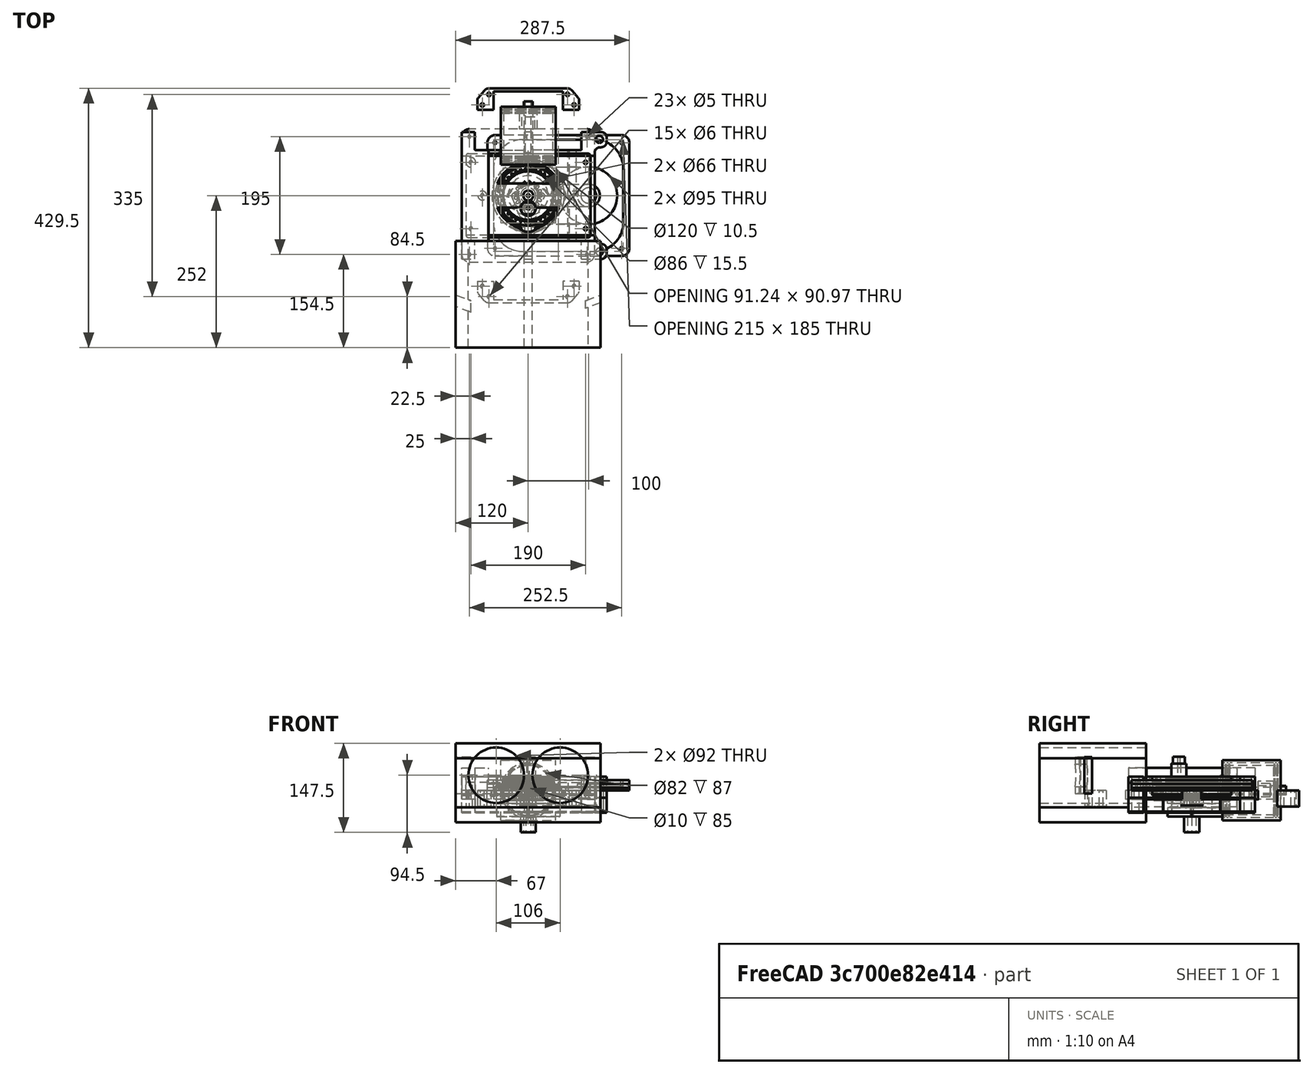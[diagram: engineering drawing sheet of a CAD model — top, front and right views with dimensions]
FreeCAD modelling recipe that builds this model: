
FCSTD DOCUMENT  (FreeCAD 1.0R38641 +678 (Git))
Label: assm4_XX_at_Tusi_rider
License: All rights reserved
objects: Sketcher::SketchObject×46, PartDesign::Body×30, PartDesign::Pad×28, PartDesign::CoordinateSystem×27, App::Link×25, PartDesign::Pocket×19, Mesh::Feature×12, PartDesign::FeatureBase×8, PartDesign::SubtractiveCylinder×5, App::DocumentObjectGroup×4, PartDesign::AdditiveCylinder×4, PartDesign::Boolean×2, Part::Extrusion×2, Part::FeaturePython×2, PartDesign::Hole×2, PartDesign::Fillet×2, App::FeaturePython×1, Spreadsheet::Sheet×1, Part::MultiFuse×1, PartDesign::Chamfer×1, +3 more types
note: 360 computed .brp shape members not serialized (recipe doc carries the construction recipe); baked Part::Feature solids carry a one-line shape summary decoded from their .brp

FEATURE [PartDesign::CoordinateSystem] LCS_Origin
  AttacherType = Attacher::AttachEngine3D
  AttachmentSupport = -> [X_Axis]
  MapMode = 2
FEATURE [App::DocumentObjectGroup] Constraints
FEATURE [App::FeaturePython] Variables  # WARN: FeaturePython — macro-defined, semantics opaque (R4)
  Crank_Angle = 360
  Type = App::PropertyContainer
FEATURE [App::DocumentObjectGroup] Configurations
FEATURE [Sketcher::SketchObject] Sketch002
  ArcFitTolerance = 0
  AttachmentSupport = -> [XY_Plane006]
  FullyConstrained = true
  MakeInternals = false
  MapMode = 5
  expr: Constraints[0] = <<Dim_table>>.crank_dia1
  expr: Constraints[20] = <<Dim_table>>.hex_size
  sketch-geometry (8):
    g0: Circle CenterX=0 CenterY=0 CenterZ=0 NormalX=0 NormalY=0 NormalZ=1 AngleXU=0 Radius=12.5
    g1: LineSegment StartX=4.04145 StartY=7 StartZ=0 EndX=-4.04145 EndY=7 EndZ=0
    g2: LineSegment StartX=-4.04145 StartY=7 StartZ=0 EndX=-8.0829 EndY=0 EndZ=0
    g3: LineSegment StartX=-8.0829 StartY=0 StartZ=0 EndX=-4.04145 EndY=-7 EndZ=0
    g4: LineSegment StartX=-4.04145 StartY=-7 StartZ=0 EndX=4.04145 EndY=-7 EndZ=0
    g5: LineSegment StartX=4.04145 StartY=-7 StartZ=0 EndX=8.0829 EndY=-9e-16 EndZ=0
    g6: LineSegment StartX=8.0829 StartY=-9e-16 StartZ=0 EndX=4.04145 EndY=7 EndZ=0
    g7: Circle [constr] CenterX=0 CenterY=0 CenterZ=0 NormalX=0 NormalY=0 NormalZ=1 AngleXU=0 Radius=8.0829
  constraints (18):
    c: Diameter(g0) = 25
    c: Coincident(g1,g2)
    c: Coincident(g2,g3)
    c: Coincident(g3,g4)
    c: Coincident(g4,g5)
    c: Coincident(g5,g6)
    c: Coincident(g6,g1)
    c: Equal(g1, g2-g6) x5
    c: PointOnObject(g1,g7)
    c: PointOnObject(g2,g7)
    c: PointOnObject(g3,g7)
    c: PointOnObject(g4,g7)
    c: PointOnObject(g5,g7)
    c: PointOnObject(g6,g7)
    c: Coincident(g7,g0)
    c: Horizontal(g1)
    c: DistanceY(g3,g1) = 14
    c: Coincident(g0,g-1)
FEATURE [PartDesign::Pad] Pad005
  Direction = (0,0,1)
  Length = 26
  Length2 = 10
  Profile = -> Sketch002
  ReferenceAxis = -> Sketch002 [N_Axis]
  Reversed = true
  Suppressed = false
  Type = 0
FEATURE [PartDesign::Body] Body005  label="Шейка коренная"
  AllowCompound = false
  Group = -> [Sketch002,Pad005]
  Origin = -> Origin006
  Placement = pos=(0,0,47) rot=(0,0,1;0rad)
  Tip = -> Pad005
FEATURE [PartDesign::FeatureBase] Clone004
  BaseFeature = -> Body005
  Suppressed = false
FEATURE [PartDesign::Body] Body054
  AllowCompound = false
  Group = -> [Clone004]
  Origin = -> Origin055
  Placement = pos=(0,0,-43.5) rot=(0,0,1;0rad)
  Tip = -> Clone004
FEATURE [Sketcher::SketchObject] Sketch003
  ArcFitTolerance = 0
  AttachmentSupport = -> [XY_Plane005]
  FullyConstrained = true
  MakeInternals = false
  MapMode = 5
  expr: Constraints[17] = <<Dim_table>>.fillet_r
  expr: Constraints[18] = <<Dim_table>>.fillet_r
  expr: Constraints[21] = <<Dim_table>>.inter_shaft_len - <<Dim_table>>.zazor
  expr: Constraints[23] = <<Dim_table>>.axle_hole_dia
  expr: Constraints[25] = 70
  expr: Constraints[26] = <<Dim_table>>.crank_dia2 * 1.5
  expr: Constraints[27] = <<Dim_table>>.crank_len
  sketch-geometry (14):
    g0: ArcOfCircle CenterX=0 CenterY=0 CenterZ=0 NormalX=0 NormalY=0 NormalZ=1 AngleXU=0 Radius=52.5 StartAngle=0.0396143 EndAngle=3.10198
    g1: ArcOfCircle CenterX=-1.2e-15 CenterY=-21.25 CenterZ=0 NormalX=0 NormalY=0 NormalZ=1 AngleXU=0 Radius=18.75 StartAngle=3.49066 EndAngle=5.93412
    g2: LineSegment [constr] StartX=-17.6192 StartY=-27.6629 StartZ=0 EndX=17.6192 EndY=-27.6629 EndZ=0
    g3: LineSegment StartX=-50.4604 StartY=0 StartZ=0 EndX=-29.0881 EndY=0 EndZ=0
    g4: LineSegment StartX=-27.2087 StartY=-1.31596 StartZ=0 EndX=-17.6192 EndY=-27.6629 EndZ=0
    g5: LineSegment StartX=17.6192 StartY=-27.6629 StartZ=0 EndX=27.2087 EndY=-1.31596 EndZ=0
    g6: LineSegment StartX=29.0881 StartY=-7e-16 StartZ=0 EndX=50.4604 EndY=-7e-16 EndZ=0
    g7: ArcOfCircle CenterX=-29.0881 CenterY=-2 CenterZ=0 NormalX=0 NormalY=0 NormalZ=1 AngleXU=0 Radius=2 StartAngle=0.349066 EndAngle=1.5708
    g8: ArcOfCircle CenterX=29.0881 CenterY=-2 CenterZ=0 NormalX=0 NormalY=0 NormalZ=1 AngleXU=0 Radius=2 StartAngle=1.5708 EndAngle=2.79253
    g9: ArcOfCircle CenterX=50.4604 CenterY=2 CenterZ=0 NormalX=0 NormalY=0 NormalZ=1 AngleXU=0 Radius=2 StartAngle=4.71239 EndAngle=6.3228
    g10: ArcOfCircle CenterX=-50.4604 CenterY=2 CenterZ=0 NormalX=0 NormalY=0 NormalZ=1 AngleXU=0 Radius=2 StartAngle=3.10198 EndAngle=4.71239
    g11: Circle [constr] CenterX=0 CenterY=0 CenterZ=0 NormalX=0 NormalY=0 NormalZ=1 AngleXU=0 Radius=49.75
    g12: Circle CenterX=0 CenterY=0 CenterZ=0 NormalX=0 NormalY=0 NormalZ=1 AngleXU=0 Radius=2.5
    g13: Circle [constr] CenterX=-1.2e-15 CenterY=-21.25 CenterZ=0 NormalX=0 NormalY=0 NormalZ=1 AngleXU=0 Radius=2.5
  constraints (31):
    c: Coincident(g2,g1)
    c: Coincident(g2,g1)
    c: Horizontal(g2)
    c: Horizontal(g3)
    c: Horizontal(g6)
    c: Tangent(g4,g1) = -1.5708
    c: Tangent(g5,g1) = -1.5708
    c: Tangent(g3,g7) = 1.5708
    c: Tangent(g4,g7) = 1.5708
    c: Tangent(g6,g8) = 1.5708
    c: Tangent(g5,g8) = 1.5708
    c: Tangent(g6,g9) = -1.5708
    c: Tangent(g0,g9) = -1.5708
    c: Tangent(g0,g10) = -1.5708
    c: Tangent(g3,g10) = -1.5708
    c: Symmetric(g7,g8,g-2)
    c: Symmetric(g10,g9,g-2)
    c: Radius(g10) = 2
    c: Radius(g7) = 2
    c: Coincident(g0,g-1)
    c: Coincident(g11,g0)
    c: Diameter(g11) = 99.5
    c: Coincident(g12,g11)
    c: Diameter(g12) = 5
    c: Diameter(g0) = 105
    c: Angle(g5) = 1.22173
    c: Diameter(g1) = 37.5
    c: DistanceY(g1,g12) = 21.25
    c: PointOnObject(g3,g-1)
    c: Coincident(g13,g1)
    c: Equal(g13,g12)
FEATURE [PartDesign::Pad] Pad004
  Direction = (0,0,1)
  Length = 15
  Length2 = 10
  Profile = -> Sketch003
  ReferenceAxis = -> Sketch003 [N_Axis]
  Suppressed = false
  Type = 0
FEATURE [PartDesign::Body] Body004  label="Щека"
  AllowCompound = false
  Group = -> [Sketch003,Pad004]
  Origin = -> Origin005
  Placement = pos=(0,0,12.5) rot=(0,0,1;0rad)
  Tip = -> Pad004
FEATURE [PartDesign::FeatureBase] Clone005
  BaseFeature = -> Body004
  Suppressed = false
FEATURE [PartDesign::Body] Body055
  AllowCompound = false
  Group = -> [Clone005]
  Origin = -> Origin056
  Placement = pos=(0,0,-43.5) rot=(0,0,1;0rad)
  Tip = -> Clone005
FEATURE [Sketcher::SketchObject] Sketch004
  ArcFitTolerance = 0
  AttachmentSupport = -> [XY_Plane004]
  FullyConstrained = true
  MakeInternals = false
  MapMode = 5
  expr: Constraints[0] = <<Dim_table>>.crank_dia2
  expr: Constraints[2] = <<Dim_table>>.crank_len
  expr: Constraints[4] = <<Dim_table>>.axle_hole_dia
  sketch-geometry (2):
    g0: Circle CenterX=0 CenterY=-21.25 CenterZ=0 NormalX=0 NormalY=0 NormalZ=1 AngleXU=0 Radius=12.5
    g1: Circle CenterX=0 CenterY=-21.25 CenterZ=0 NormalX=0 NormalY=0 NormalZ=1 AngleXU=0 Radius=2.5
  constraints (5):
    c: Diameter(g0) = 25
    c: PointOnObject(g0,g-2)
    c: DistanceY(g0,g-1) = 21.25
    c: Coincident(g1,g0)
    c: Diameter(g1) = 5
FEATURE [PartDesign::Pad] Pad003
  Direction = (0,0,1)
  Length = 79.5
  Length2 = 0
  Profile = -> Sketch004
  ReferenceAxis = -> Sketch004 [N_Axis]
  Suppressed = false
  Type = 0
FEATURE [Sketcher::SketchObject] Sketch005
  ArcFitTolerance = 0
  AttachmentSupport = -> [XY_Plane002]
  FullyConstrained = true
  MakeInternals = false
  MapMode = 5
  expr: Constraints[1] = <<Dim_table>>.crank_dia2 + <<Dim_table>>.zazor
  expr: Constraints[26] = 10
  expr: Constraints[27] = <<Dim_table>>.ecc_dia * 0.8
  expr: Constraints[28] = <<Dim_table>>.crank_dia2 * 2
  expr: Constraints[2] = <<Dim_table>>.ecc_dia + <<Dim_table>>.roller_dia
  expr: Constraints[3] = <<Dim_table>>.crank_len
  sketch-geometry (14):
    g0: Circle CenterX=0 CenterY=-21.25 CenterZ=0 NormalX=0 NormalY=0 NormalZ=1 AngleXU=0 Radius=41.5
    g1: Circle CenterX=0 CenterY=0 CenterZ=0 NormalX=0 NormalY=0 NormalZ=1 AngleXU=0 Radius=12.75
    g2: ArcOfCircle CenterX=0 CenterY=-21.25 CenterZ=0 NormalX=0 NormalY=0 NormalZ=1 AngleXU=0 Radius=32 StartAngle=3.32205 EndAngle=4.38515
    g3: ArcOfCircle CenterX=0 CenterY=-21.25 CenterZ=0 NormalX=0 NormalY=0 NormalZ=1 AngleXU=0 Radius=32 StartAngle=5.03963 EndAngle=6.10273
    g4: LineSegment StartX=-5 StartY=-27.5681 StartZ=0 EndX=-5 EndY=-47.7641 EndZ=0
    g5: LineSegment StartX=5 StartY=-27.5681 StartZ=0 EndX=5 EndY=-47.7641 EndZ=0
    g6: ArcOfCircle CenterX=0 CenterY=0 CenterZ=0 NormalX=0 NormalY=0 NormalZ=1 AngleXU=0 Radius=25 StartAngle=3.98424 EndAngle=4.39683
    g7: ArcOfCircle CenterX=0 CenterY=0 CenterZ=0 NormalX=0 NormalY=0 NormalZ=1 AngleXU=0 Radius=25 StartAngle=5.02794 EndAngle=5.44053
    g8: ArcOfCircle CenterX=-22.6265 CenterY=-25.3779 CenterZ=0 NormalX=0 NormalY=0 NormalZ=1 AngleXU=0 Radius=9 StartAngle=0.842651 EndAngle=3.32205
    g9: ArcOfCircle CenterX=22.6265 CenterY=-25.3779 CenterZ=0 NormalX=0 NormalY=0 NormalZ=1 AngleXU=0 Radius=9 StartAngle=6.10273 EndAngle=8.58213
    g10: ArcOfCircle CenterX=-9 CenterY=-47.7641 CenterZ=0 NormalX=0 NormalY=0 NormalZ=1 AngleXU=0 Radius=4 StartAngle=4.38515 EndAngle=6.28319
    g11: ArcOfCircle CenterX=9 CenterY=-47.7641 CenterZ=0 NormalX=0 NormalY=0 NormalZ=1 AngleXU=0 Radius=4 StartAngle=3.14159 EndAngle=5.03963
    g12: ArcOfCircle CenterX=-9 CenterY=-27.5681 CenterZ=0 NormalX=0 NormalY=0 NormalZ=1 AngleXU=0 Radius=4 StartAngle=0 EndAngle=1.25524
    g13: ArcOfCircle CenterX=9 CenterY=-27.5681 CenterZ=0 NormalX=0 NormalY=0 NormalZ=1 AngleXU=0 Radius=4 StartAngle=1.88635 EndAngle=3.14159
  constraints (32):
    c: PointOnObject(g0,g-2)
    c: Diameter(g1) = 25.5
    c: Diameter(g0) = 83
    c: Distance(g1,g0) = 21.25
    c: Coincident(g1,g-1)
    c: Coincident(g2,g0)
    c: Coincident(g3,g0)
    c: Equal(g2,g3)
    c: Vertical(g4)
    c: Coincident(g6,g1)
    c: Coincident(g7,g1)
    c: Tangent(g2,g8) = -1.5708
    c: Tangent(g6,g8) = 1.5708
    c: Tangent(g7,g9) = 1.5708
    c: Tangent(g3,g9) = -1.5708
    c: Tangent(g2,g10) = -1.5708
    c: Tangent(g4,g10) = 1.5708
    c: Tangent(g5,g11) = -1.5708
    c: Tangent(g3,g11) = -1.5708
    c: Tangent(g6,g12) = 1.5708
    c: Tangent(g4,g12) = 1.5708
    c: Tangent(g5,g13) = -1.5708
    c: Tangent(g7,g13) = 1.5708
    c: Symmetric(g12,g13,g-2)
    c: Symmetric(g10,g11,g-2)
    c: Symmetric(g8,g9,g-2)
    c: DistanceX(g4,g5) = 10
    c: Diameter(g2) = 64
    c: Diameter(g6) = 50
    c: Radius(g10) = 4
    c: Equal(g10,g12)
    c: Radius(g8) = 9
FEATURE [PartDesign::CoordinateSystem] Eccentr
  AttacherType = Attacher::AttachEngine3D
  AttachmentOffset = pos=(0,0,0) rot=(0,0,1;1.5708rad)
  AttachmentSupport = -> [Sketch005]
  MapMode = 11
  Placement = pos=(0,0,0) rot=(0,0,1;3.14159rad)
FEATURE [PartDesign::Pad] Pad001
  Direction = (0,0,1)
  Length = 16.5
  Length2 = 0
  Profile = -> Sketch005
  ReferenceAxis = -> Sketch005 [N_Axis]
  Reversed = true
  Suppressed = false
  Type = 0
  expr: Length = <<Dim_table>>.ecc_hei
FEATURE [Sketcher::SketchObject] Sketch007
  ArcFitTolerance = 0
  AttachmentSupport = -> [XY_Plane003]
  FullyConstrained = true
  MakeInternals = false
  MapMode = 5
  expr: Constraints[15] = <<Dim_table>>.ecc_dia * 1.3
  expr: Constraints[17] = <<Dim_table>>.ecc_dia * 0.8
  expr: Constraints[1] = <<Dim_table>>.ecc_dia + 2 * <<Dim_table>>.roller_dia
  sketch-geometry (15):
    g0: Circle CenterX=0 CenterY=0 CenterZ=0 NormalX=0 NormalY=0 NormalZ=1 AngleXU=0 Radius=43
    g1: ArcOfCircle CenterX=0 CenterY=0 CenterZ=0 NormalX=0 NormalY=0 NormalZ=1 AngleXU=0 Radius=52 StartAngle=1.86916 EndAngle=3.14159
    g2: ArcOfCircle CenterX=0 CenterY=0 CenterZ=0 NormalX=0 NormalY=0 NormalZ=1 AngleXU=0 Radius=52 StartAngle=0 EndAngle=1.27243
    g3: LineSegment StartX=-11.8314 StartY=53.6134 StartZ=0 EndX=-10 EndY=64 EndZ=0
    g4: LineSegment StartX=-10 StartY=64 StartZ=0 EndX=10 EndY=64 EndZ=0
    g5: LineSegment StartX=10 StartY=64 StartZ=0 EndX=11.8314 EndY=53.6134 EndZ=0
    g6: ArcOfCircle CenterX=-16.7555 CenterY=54.4817 CenterZ=0 NormalX=0 NormalY=0 NormalZ=1 AngleXU=0 Radius=5 StartAngle=5.01075 EndAngle=6.10865
    g7: ArcOfCircle CenterX=16.7555 CenterY=54.4817 CenterZ=0 NormalX=0 NormalY=0 NormalZ=1 AngleXU=0 Radius=5 StartAngle=3.31613 EndAngle=4.41403
    g8: ArcOfCircle CenterX=-2.7e-15 CenterY=2.94305e-05 CenterZ=0 NormalX=0 NormalY=0 NormalZ=1 AngleXU=0 Radius=52 StartAngle=3.14159 EndAngle=4.41403
    g9: ArcOfCircle CenterX=-16.7555 CenterY=-54.4817 CenterZ=0 NormalX=0 NormalY=0 NormalZ=1 AngleXU=0 Radius=5 StartAngle=0.174533 EndAngle=1.27243
    g10: LineSegment StartX=-11.8314 StartY=-53.6134 StartZ=0 EndX=-10 EndY=-64 EndZ=0
    g11: LineSegment StartX=-10 StartY=-64 StartZ=0 EndX=10 EndY=-64 EndZ=0
    g12: LineSegment StartX=10 StartY=-64 StartZ=0 EndX=11.8314 EndY=-53.6134 EndZ=0
    g13: ArcOfCircle CenterX=16.7555 CenterY=-54.4817 CenterZ=0 NormalX=0 NormalY=0 NormalZ=1 AngleXU=0 Radius=5 StartAngle=1.86916 EndAngle=2.96706
    g14: ArcOfCircle CenterX=-2.7e-15 CenterY=2.94305e-05 CenterZ=0 NormalX=0 NormalY=0 NormalZ=1 AngleXU=0 Radius=52 StartAngle=5.01075 EndAngle=6.28318
  constraints (36):
    c: Coincident(g0,g-1)
    c: Diameter(g0) = 86
    c: Coincident(g1,g0)
    c: Coincident(g2,g0)
    c: Equal(g1,g2)
    c: Coincident(g3,g4)
    c: Coincident(g4,g5)
    c: Tangent(g1,g6) = 1.5708
    c: Tangent(g3,g6) = -1.5708
    c: Tangent(g5,g7) = -1.5708
    c: Tangent(g2,g7) = 1.5708
    c: Symmetric(g6,g7,g-2)
    c: Symmetric(g3,g4,g-2)
    c: PointOnObject(g1,g-1)
    c: PointOnObject(g2,g-1)
    c: Diameter(g1) = 104
    c: Distance(g4,g4) = 20
    c: DistanceY(g0,g4) = 64
    c: Radius(g6) = 5
    c: Angle(g3,g-2) = 0.174533
    c: Equal(g8,g14)
    c: Coincident(g10,g11)
    c: Coincident(g11,g12)
    c: Tangent(g8,g9) = 1.5708
    c: Tangent(g10,g9) = 1.5708
    c: Tangent(g12,g13) = 1.5708
    c: Tangent(g14,g13) = 1.5708
    c: Equal(g8,g1)
    c: Equal(g13,g7)
    c: Symmetric(g9,g13,g-2)
    c: Symmetric(g11,g4,g-1)
    c: Symmetric(g10,g11,g-2)
    c: Parallel(g12,g3)
    c: Coincident(g8,g1)
    c: Coincident(g14,g2)
    c: Coincident(g8,g14)
FEATURE [PartDesign::Pad] Pad002
  Direction = (0,0,1)
  Length = 15.5
  Length2 = 10
  Midplane = true
  Profile = -> Sketch007
  ReferenceAxis = -> Sketch007 [N_Axis]
  Suppressed = false
  Type = 0
  expr: Length = <<Dim_table>>.ecc_hei - 1
FEATURE [PartDesign::CoordinateSystem] Shtok
  AttacherType = Attacher::AttachEngine3D
  AttachmentSupport = -> [Pad002]
  MapMode = 45
  Placement = pos=(-7.2e-15,2.69855e-05,-3e-16) rot=(0,0,1;0rad)
FEATURE [Sketcher::SketchObject] Main
  ArcFitTolerance = 0
  AttachmentSupport = -> [LCS_Origin]
  FullyConstrained = false
  MakeInternals = false
  MapMode = 5
  expr: Constraints[17] = <<Dim_table>>.piston_dia
  expr: Constraints[18] = <<Dim_table>>.piston_hei
  expr: Constraints[19] = <<Dim_table>>.ecc_dia
  expr: Constraints[1] = <<Variables>>.Crank_Angle
  expr: Constraints[26] = <<Dim_table>>.rod_len
  expr: Constraints[2] = <<Dim_table>>.crank_len
  expr: Constraints[48] = <<Dim_table>>.crank_len
  expr: Constraints[53] = <<Dim_table>>.crank_len
  expr: Constraints[5] = <<Dim_table>>.crank_dia1
  expr: Constraints[67] = <<Variables>>.Crank_Angle
  expr: Constraints[6] = <<Dim_table>>.crank_dia2
  sketch-geometry (33):
    g0: LineSegment StartX=0 StartY=0 StartZ=0 EndX=-2.74918e-11 EndY=21.25 EndZ=0
    g1: Circle [constr] CenterX=0 CenterY=0 CenterZ=0 NormalX=0 NormalY=0 NormalZ=1 AngleXU=0 Radius=12.5
    g2: Circle CenterX=-2.74918e-11 CenterY=21.25 CenterZ=0 NormalX=0 NormalY=0 NormalZ=1 AngleXU=0 Radius=12.5
    g3: LineSegment StartX=-36 StartY=221.5 StartZ=0 EndX=36 EndY=221.5 EndZ=0
    g4: LineSegment StartX=36 StartY=221.5 StartZ=0 EndX=36 EndY=182.5 EndZ=0
    g5: LineSegment StartX=36 StartY=182.5 StartZ=0 EndX=-36 EndY=182.5 EndZ=0
    g6: LineSegment StartX=-36 StartY=182.5 StartZ=0 EndX=-36 EndY=221.5 EndZ=0
    g7: LineSegment [constr] StartX=-36 StartY=182.5 StartZ=0 EndX=36 EndY=221.5 EndZ=0
    g8: Circle CenterX=6.3065e-12 CenterY=42.5 CenterZ=0 NormalX=0 NormalY=0 NormalZ=1 AngleXU=0 Radius=40
    g9: LineSegment StartX=120.841 StartY=-28.1981 StartZ=0 EndX=84.8405 EndY=-90.5519 EndZ=0
    g10: LineSegment StartX=84.8405 StartY=-90.5519 StartZ=0 EndX=118.616 EndY=-110.052 EndZ=0
    g11: LineSegment StartX=118.616 StartY=-110.052 StartZ=0 EndX=154.616 EndY=-47.6981 EndZ=0
    g12: LineSegment StartX=154.616 StartY=-47.6981 StartZ=0 EndX=120.841 EndY=-28.1981 EndZ=0
    g13: LineSegment StartX=6.3065e-12 StartY=182.5 StartZ=0 EndX=6.3065e-12 EndY=42.5 EndZ=0
    g14: LineSegment StartX=-36 StartY=-136.5 StartZ=0 EndX=36 EndY=-136.5 EndZ=0
    g15: LineSegment StartX=36 StartY=-136.5 StartZ=0 EndX=36 EndY=-97.5 EndZ=0
    g16: LineSegment StartX=36 StartY=-97.5 StartZ=0 EndX=-36 EndY=-97.5 EndZ=0
    g17: LineSegment StartX=-36 StartY=-97.5 StartZ=0 EndX=-36 EndY=-136.5 EndZ=0
    g18: LineSegment [constr] StartX=6.3065e-12 StartY=-97.5 StartZ=0 EndX=6.3065e-12 EndY=42.5 EndZ=0
    g19: LineSegment StartX=155.422 StartY=131.302 StartZ=0 EndX=191.422 EndY=68.9481 EndZ=0
    g20: LineSegment StartX=191.422 StartY=68.9481 StartZ=0 EndX=157.647 EndY=49.4481 EndZ=0
    g21: LineSegment StartX=157.647 StartY=49.4481 StartZ=0 EndX=121.647 EndY=111.802 EndZ=0
    g22: LineSegment StartX=121.647 StartY=111.802 StartZ=0 EndX=155.422 EndY=131.302 EndZ=0
    g23: LineSegment StartX=-2.74918e-11 StartY=21.25 StartZ=0 EndX=18.403 EndY=10.625 EndZ=0
    g24: LineSegment StartX=-2.74918e-11 StartY=21.25 StartZ=0 EndX=7.4e-15 EndY=-3.6e-15 EndZ=0
    g25: LineSegment StartX=-2.74918e-11 StartY=21.25 StartZ=0 EndX=6.3065e-12 EndY=42.5 EndZ=0
    g26: LineSegment [constr] StartX=-238.615 StartY=-137.765 StartZ=0 EndX=319.415 EndY=184.414 EndZ=0
    g27: LineSegment [constr] StartX=-222.3 StartY=128.345 StartZ=0 EndX=247.423 EndY=-142.85 EndZ=0
    g28: LineSegment StartX=-2.74918e-11 StartY=21.25 StartZ=0 EndX=-18.403 EndY=10.625 EndZ=0
    g29: Circle CenterX=-18.403 CenterY=10.625 CenterZ=0 NormalX=0 NormalY=0 NormalZ=1 AngleXU=0 Radius=40
    g30: Circle CenterX=18.403 CenterY=10.625 CenterZ=0 NormalX=0 NormalY=0 NormalZ=1 AngleXU=0 Radius=40
    g31: LineSegment StartX=18.403 StartY=10.625 StartZ=0 EndX=139.647 EndY=80.625 EndZ=0
    g32: LineSegment StartX=-18.403 StartY=10.625 StartZ=0 EndX=102.841 EndY=-59.375 EndZ=0
  constraints (87):
    c: Coincident(g0,g-1)
    c: Angle(g0,g-2) = 6.28319
    c: Distance(g0) = 21.25
    c: Coincident(g1,g0)
    c: Coincident(g2,g0)
    c: Diameter(g1) = 25
    c: Diameter(g2) = 25
    c: Coincident(g3,g4)
    c: Coincident(g4,g5)
    c: Coincident(g5,g6)
    c: Coincident(g6,g3)
    c: Horizontal(g3)
    c: Horizontal(g5)
    c: Vertical(g4)
    c: Vertical(g6)
    c: Coincident(g7,g5)
    c: Coincident(g7,g3)
    c: Distance(g3) = 72
    c: Distance(g4) = 39
    c: Diameter(g8) = 80
    c: Coincident(g9,g10)
    c: Coincident(g10,g11)
    c: Coincident(g11,g12)
    c: Coincident(g12,g9)
    c: Vertical(g13)
    c: Symmetric(g5,g4,g13)
    c: Distance(g13,g13) = 140
    c: Equal(g4,g12)
    c: Equal(g3,g11)
    c: Coincident(g14,g15)
    c: Coincident(g15,g16)
    c: Coincident(g16,g17)
    c: Coincident(g17,g14)
    c: Horizontal(g14)
    c: Horizontal(g16)
    c: Vertical(g15)
    c: Vertical(g17)
    c: Vertical(g18)
    c: Symmetric(g16,g15,g18)
    c: Equal(g16,g11)
    c: Equal(g15,g12)
    c: Coincident(g19,g20)
    c: Coincident(g20,g21)
    c: Coincident(g21,g22)
    c: Coincident(g22,g19)
    c: Equal(g22,g12)
    c: Equal(g21,g11)
    c: Coincident(g23,g0)
    c: Distance(g23,g23) = 21.25
    c: Coincident(g24,g0)
    c: Coincident(g25,g0)
    c: Equal(g25,g24)
    c: Angle(g23,g25) = 2.0944
    c: Distance(g24,g24) = 21.25
    c: PointOnObject(g24,g27)
    c: PointOnObject(g0,g27)
    c: PointOnObject(g0,g26)
    c: Parallel(g9,g11)
    c: Parallel(g12,g10)
    c: Angle(g9,g12) = 1.5708
    c: Angle(g21,g22) = 1.5708
    c: Parallel(g22,g20)
    c: Parallel(g19,g21)
    c: Equal(g13,g18)
    c: Angle(g-2,g26) = 2.0944
    c: Angle(g-2,g27) = 1.0472
    c: Coincident(g13,g25)
    c: Angle(g-2,g25) = 6.28319
    c: Coincident(g28,g0)
    c: Equal(g23,g28)
    c: Angle(g28,g23) = 2.0944
    c: Coincident(g8,g13)
    c: Equal(g8,g30)
    c: Equal(g30,g29)
    c: Coincident(g30,g23)
    c: Coincident(g29,g28)
    c: Coincident(g31,g23)
    c: Coincident(g32,g28)
    c: Symmetric(g9,g9,g32)
    c: Symmetric(g21,g20,g31)
    c: Angle(g21,g31) = 1.5708
    c: Angle(g9,g32) = 1.5708
    c: PointOnObject(g32,g27)
    c: PointOnObject(g31,g26)
    c: Coincident(g18,g8)
    c: Equal(g18,g32)
    c: Equal(g32,g31)
FEATURE [Sketcher::SketchObject] Sketch021
  ArcFitTolerance = 0
  AttachmentSupport = -> [XY_Plane062]
  FullyConstrained = false
  MakeInternals = false
  MapMode = 5
  sketch-geometry (30):
    g0: LineSegment [constr] StartX=-110 StartY=225 StartZ=0 EndX=110 EndY=225 EndZ=0
    g1: LineSegment [constr] StartX=110 StartY=225 StartZ=0 EndX=110 EndY=-225 EndZ=0
    g2: LineSegment [constr] StartX=110 StartY=-225 StartZ=0 EndX=-110 EndY=-225 EndZ=0
    g3: LineSegment [constr] StartX=-110 StartY=-225 StartZ=0 EndX=-110 EndY=225 EndZ=0
    g4: LineSegment [constr] StartX=-110 StartY=225 StartZ=0 EndX=-110 EndY=105 EndZ=0
    g5: LineSegment [constr] StartX=-110 StartY=105 StartZ=0 EndX=110 EndY=105 EndZ=0
    g6: LineSegment [constr] StartX=110 StartY=105 StartZ=0 EndX=110 EndY=225 EndZ=0
    g7: LineSegment [constr] StartX=-110 StartY=-225 StartZ=0 EndX=-110 EndY=-105 EndZ=0
    g8: LineSegment StartX=-110 StartY=-105 StartZ=0 EndX=110 EndY=-105 EndZ=0
    g9: LineSegment [constr] StartX=110 StartY=-105 StartZ=0 EndX=110 EndY=-225 EndZ=0
    g10: LineSegment [constr] StartX=-110 StartY=-105 StartZ=0 EndX=-110 EndY=105 EndZ=0
    g11: LineSegment StartX=110 StartY=105 StartZ=0 EndX=-110 EndY=105 EndZ=0
    g12: Circle CenterX=0 CenterY=0 CenterZ=0 NormalX=0 NormalY=0 NormalZ=1 AngleXU=0 Radius=33
    g13: LineSegment StartX=-110 StartY=105 StartZ=0 EndX=-110 EndY=0 EndZ=0
    g14: LineSegment [constr] StartX=110 StartY=-105 StartZ=0 EndX=110 EndY=105 EndZ=0
    g15: LineSegment StartX=110 StartY=105 StartZ=0 EndX=120.902 EndY=105 EndZ=0
    g16: LineSegment StartX=130 StartY=95.9016 StartZ=0 EndX=130 EndY=89.0984 EndZ=0
    g17: LineSegment StartX=120.902 StartY=80 StartZ=0 EndX=119.098 EndY=80 EndZ=0
    g18: ArcOfCircle CenterX=120.902 CenterY=95.9016 CenterZ=0 NormalX=0 NormalY=0 NormalZ=1 AngleXU=0 Radius=9.09838 StartAngle=0 EndAngle=1.5708
    g19: ArcOfCircle CenterX=120.902 CenterY=89.0984 CenterZ=0 NormalX=0 NormalY=0 NormalZ=1 AngleXU=0 Radius=9.09838 StartAngle=4.71239 EndAngle=6.28319
    g20: LineSegment StartX=110 StartY=70.9016 StartZ=0 EndX=110 EndY=0 EndZ=0
    g21: ArcOfCircle CenterX=119.098 CenterY=70.9016 CenterZ=0 NormalX=0 NormalY=0 NormalZ=1 AngleXU=0 Radius=9.09838 StartAngle=1.5708 EndAngle=3.14159
    g22: LineSegment StartX=110 StartY=-105 StartZ=0 EndX=120.902 EndY=-105 EndZ=0
    g23: LineSegment StartX=130 StartY=-95.9016 StartZ=0 EndX=130 EndY=-89.0984 EndZ=0
    g24: LineSegment StartX=120.902 StartY=-80 StartZ=0 EndX=119.098 EndY=-80 EndZ=0
    g25: ArcOfCircle CenterX=120.902 CenterY=-95.9016 CenterZ=0 NormalX=0 NormalY=0 NormalZ=1 AngleXU=0 Radius=9.09838 StartAngle=4.71239 EndAngle=6.28319
    g26: ArcOfCircle CenterX=120.902 CenterY=-89.0984 CenterZ=0 NormalX=0 NormalY=0 NormalZ=1 AngleXU=0 Radius=9.09838 StartAngle=0 EndAngle=1.5708
    g27: LineSegment StartX=110 StartY=-70.9016 StartZ=0 EndX=110 EndY=0 EndZ=0
    g28: ArcOfCircle CenterX=119.098 CenterY=-70.9016 CenterZ=0 NormalX=0 NormalY=0 NormalZ=1 AngleXU=0 Radius=9.09838 StartAngle=3.14159 EndAngle=4.71239
    g29: LineSegment StartX=-110 StartY=-105 StartZ=0 EndX=-110 EndY=0 EndZ=0
  constraints (61):
    c: Coincident(g0,g1)
    c: Coincident(g1,g2)
    c: Coincident(g2,g3)
    c: Coincident(g3,g0)
    c: Horizontal(g2)
    c: Vertical(g1)
    c: Symmetric(g0,g0,g-2)
    c: Symmetric(g0,g2,g-1)
    c: Coincident(g0,g4)
    c: PointOnObject(g4,g3)
    c: Coincident(g4,g5)
    c: PointOnObject(g5,g1)
    c: Horizontal(g5)
    c: Coincident(g6,g0)
    c: Coincident(g2,g7)
    c: PointOnObject(g7,g3)
    c: Horizontal(g8)
    c: Coincident(g9,g2)
    c: Equal(g9,g6)
    c: DistanceX(g2,g2) = 220
    c: DistanceY(g3,g3) = 450
    c: DistanceY(g9,g9) = 120
    c: Coincident(g10,g4)
    c: Coincident(g11,g10)
    c: Diameter(g12) = 66
    c: PointOnObject(g13,g-1)
    c: Vertical(g13)
    c: Vertical(g10)
    c: Vertical(g6)
    c: Coincident(g8,g9)
    c: Coincident(g8,g7)
    c: Coincident(g11,g5)
    c: Symmetric(g8,g11,g-1)
    c: Horizontal(g15)
    c: Horizontal(g17)
    c: Vertical(g16)
    c: Tangent(g15,g18) = 1.5708
    c: Tangent(g16,g18) = 1.5708
    c: Tangent(g16,g19) = 1.5708
    c: Tangent(g17,g19) = 1.5708
    c: Equal(g19,g18)
    c: Vertical(g20)
    c: Tangent(g17,g21) = -1.5708
    c: Tangent(g20,g21) = -1.5708
    c: Equal(g19,g21)
    c: Vertical(g14)
    c: Horizontal(g22)
    c: Horizontal(g24)
    c: Vertical(g23)
    c: Tangent(g22,g25) = -1.5708
    c: Tangent(g23,g25) = -1.5708
    c: Tangent(g23,g26) = -1.5708
    c: Tangent(g24,g26) = -1.5708
    c: Equal(g26,g25)
    c: Vertical(g27)
    c: Tangent(g24,g28) = 1.5708
    c: Tangent(g27,g28) = 1.5708
    c: Equal(g26,g28)
    c: Coincident(g13,g11)
    c: Coincident(g29,g8)
    c: Coincident(g29,g13)
FEATURE [Sketcher::SketchObject] Sketch022
  ArcFitTolerance = 0
  AttachmentSupport = -> [XY_Plane062]
  FullyConstrained = true
  MakeInternals = false
  MapMode = 5
  sketch-geometry (5):
    g0: LineSegment StartX=-110 StartY=-105 StartZ=0 EndX=-65.5 EndY=-105 EndZ=0
    g1: LineSegment StartX=-65.5 StartY=-105 StartZ=0 EndX=-65.5 EndY=105 EndZ=0
    g2: LineSegment StartX=-65.5 StartY=105 StartZ=0 EndX=-110 EndY=105 EndZ=0
    g3: LineSegment StartX=-110 StartY=105 StartZ=0 EndX=-110 EndY=-105 EndZ=0
    g4: LineSegment [constr] StartX=65.5 StartY=52.9337 StartZ=0 EndX=65.5 EndY=105 EndZ=0
  constraints (14):
    c: Coincident(g0,g1)
    c: Coincident(g1,g2)
    c: Coincident(g2,g3)
    c: Coincident(g3,g0)
    c: Horizontal(g0)
    c: Horizontal(g2)
    c: Vertical(g3)
    c: Vertical(g4)
    c: DistanceX(g1,g4) = 131
    c: Symmetric(g1,g4,g-2)
    c: DistanceY(g1,g1) = 210
    c: DistanceX(g0,g0) = 44.5
    c: Symmetric(g0,g1,g-1)
    c: Block(g4)
FEATURE [PartDesign::Pad] Pad012
  Direction = (0,0,1)
  Length = 35
  Length2 = 12.5
  Profile = -> Sketch021
  ReferenceAxis = -> Sketch021 [N_Axis]
  Reversed = true
  Suppressed = false
  Type = 4
FEATURE [PartDesign::Pad] Pad013
  BaseFeature = -> Pad012
  Direction = (0,0,1)
  Length = 37.5
  Length2 = -12.5
  Profile = -> Sketch022
  ReferenceAxis = -> Sketch022 [N_Axis]
  Suppressed = false
  Type = 4
FEATURE [Sketcher::SketchObject] Sketch_1
  ArcFitTolerance = 0
  FullyConstrained = false
  MakeInternals = false
  sketch-geometry (8):
    g0: Circle [constr] CenterX=0 CenterY=0 CenterZ=0 NormalX=0 NormalY=0 NormalZ=1 AngleXU=0 Radius=65.5
    g1: ArcOfCircle [constr] CenterX=0 CenterY=0 CenterZ=0 NormalX=0 NormalY=0 NormalZ=1 AngleXU=0 Radius=65.5 StartAngle=1.5708 EndAngle=4.71239
    g2: LineSegment StartX=145.598 StartY=65.5 StartZ=0 EndX=0 EndY=65.5 EndZ=0
    g3: LineSegment StartX=145.598 StartY=-65.5 StartZ=0 EndX=0 EndY=-65.5 EndZ=0
    g4: LineSegment StartX=145.598 StartY=65.5 StartZ=0 EndX=145.598 EndY=-65.5 EndZ=0
    g5: LineSegment StartX=-153.016 StartY=65.5 StartZ=0 EndX=0 EndY=65.5 EndZ=0
    g6: LineSegment StartX=-1.2e-14 StartY=-65.5 StartZ=0 EndX=-153.016 EndY=-65.5 EndZ=0
    g7: LineSegment StartX=-153.016 StartY=-65.5 StartZ=0 EndX=-153.016 EndY=65.5 EndZ=0
  constraints (18):
    c: Coincident(g0,g-1)
    c: Diameter(g0) = 131
    c: Coincident(g1,g0)
    c: PointOnObject(g1,g0)
    c: Horizontal(g2)
    c: Horizontal(g3)
    c: Tangent(g3,g1) = 1.5708
    c: Tangent(g1,g2) = -1.5708
    c: Coincident(g4,g2)
    c: Coincident(g4,g3)
    c: Vertical(g4)
    c: Coincident(g6,g7)
    c: Coincident(g7,g5)
    c: Horizontal(g5)
    c: Horizontal(g6)
    c: Vertical(g7)
    c: Coincident(g5,g2)
    c: Coincident(g6,g3)
FEATURE [PartDesign::Pocket] Pocket005
  BaseFeature = -> Pad013
  Direction = (0,0,-1)
  Length = 6.5
  Length2 = 13
  Profile = -> Sketch_1
  ReferenceAxis = -> Sketch_1 [N_Axis]
  Suppressed = false
  Type = 4
FEATURE [PartDesign::CoordinateSystem] Block_ribb
  AttacherType = Attacher::AttachEngine3D
  AttachmentSupport = -> [Pocket005]
  MapMode = 2
FEATURE [Sketcher::SketchObject] Sketch_2
  ArcFitTolerance = 0
  FullyConstrained = false
  MakeInternals = false
  sketch-geometry (44):
    g0: LineSegment StartX=-0.25 StartY=33.6074 StartZ=0 EndX=-0.25 EndY=47.5 EndZ=0
    g1: LineSegment StartX=-0.25 StartY=47.5 StartZ=0 EndX=126.736 EndY=47.5 EndZ=0
    g2: LineSegment StartX=126.736 StartY=47.5 StartZ=0 EndX=126.736 EndY=47 EndZ=0
    g3: LineSegment StartX=126.736 StartY=47 StartZ=0 EndX=0.25 EndY=47 EndZ=0
    g4: LineSegment StartX=0.25 StartY=47 StartZ=0 EndX=0.25 EndY=33.6074 EndZ=0
    g5: LineSegment StartX=0.25 StartY=33.6074 StartZ=0 EndX=-0.25 EndY=33.6074 EndZ=0
    g6: ArcOfCircle CenterX=86.75 CenterY=76.5 CenterZ=0 NormalX=0 NormalY=0 NormalZ=1 AngleXU=0 Radius=1.5 StartAngle=4.71239 EndAngle=6.28319
    g7: ArcOfCircle CenterX=8.25 CenterY=76.5 CenterZ=0 NormalX=0 NormalY=0 NormalZ=1 AngleXU=0 Radius=1.5 StartAngle=3.14159 EndAngle=4.71239
    g8: LineSegment StartX=86.75 StartY=75 StartZ=0 EndX=8.25 EndY=75 EndZ=0
    g9: LineSegment StartX=88.25 StartY=105 StartZ=0 EndX=6.75 EndY=105 EndZ=0
    g10: LineSegment StartX=6.75 StartY=105 StartZ=0 EndX=6.75 EndY=76.5 EndZ=0
    g11: LineSegment StartX=88.25 StartY=105 StartZ=0 EndX=88.25 EndY=76.5 EndZ=0
    g12: GeomPoint [constr] X=47.5 Y=105 Z=0
    g13: Circle CenterX=-118 CenterY=93 CenterZ=0 NormalX=0 NormalY=0 NormalZ=1 AngleXU=0 Radius=6
    g14: Circle CenterX=118 CenterY=93 CenterZ=0 NormalX=0 NormalY=0 NormalZ=1 AngleXU=0 Radius=6
    g15: LineSegment StartX=-0.067348 StartY=-33.6074 StartZ=0 EndX=-0.067348 EndY=-47.5 EndZ=0
    g16: LineSegment StartX=-0.067348 StartY=-47.5 StartZ=0 EndX=126.736 EndY=-47.5 EndZ=0
    g17: LineSegment StartX=126.736 StartY=-47.5 StartZ=0 EndX=126.736 EndY=-47 EndZ=0
    g18: LineSegment StartX=126.736 StartY=-47 StartZ=0 EndX=0.25 EndY=-47 EndZ=0
    g19: LineSegment StartX=0.25 StartY=-47 StartZ=0 EndX=0.25 EndY=-33.6074 EndZ=0
    g20: LineSegment StartX=0.25 StartY=-33.6074 StartZ=0 EndX=-0.067348 EndY=-33.6074 EndZ=0
    g21: ArcOfCircle CenterX=-86.75 CenterY=76.5 CenterZ=0 NormalX=0 NormalY=0 NormalZ=1 AngleXU=0 Radius=1.5 StartAngle=3.14159 EndAngle=4.71239
    g22: ArcOfCircle CenterX=-8.25 CenterY=76.5 CenterZ=0 NormalX=0 NormalY=0 NormalZ=1 AngleXU=0 Radius=1.5 StartAngle=4.71239 EndAngle=6.28319
    g23: LineSegment StartX=-86.75 StartY=75 StartZ=0 EndX=-8.25 EndY=75 EndZ=0
    g24: LineSegment StartX=-88.25 StartY=105 StartZ=0 EndX=-6.75 EndY=105 EndZ=0
    g25: LineSegment StartX=-6.75 StartY=105 StartZ=0 EndX=-6.75 EndY=76.5 EndZ=0
    g26: LineSegment StartX=-88.25 StartY=105 StartZ=0 EndX=-88.25 EndY=76.5 EndZ=0
    g27: GeomPoint [constr] X=-47.5 Y=105 Z=0
    g28: ArcOfCircle CenterX=86.75 CenterY=-76.5 CenterZ=0 NormalX=0 NormalY=0 NormalZ=1 AngleXU=0 Radius=1.5 StartAngle=0 EndAngle=1.5708
    g29: ArcOfCircle CenterX=8.25 CenterY=-76.5 CenterZ=0 NormalX=0 NormalY=0 NormalZ=1 AngleXU=0 Radius=1.5 StartAngle=1.5708 EndAngle=3.14159
    g30: LineSegment StartX=86.75 StartY=-75 StartZ=0 EndX=8.25 EndY=-75 EndZ=0
    g31: LineSegment StartX=88.25 StartY=-105 StartZ=0 EndX=6.75 EndY=-105 EndZ=0
    g32: LineSegment StartX=6.75 StartY=-105 StartZ=0 EndX=6.75 EndY=-76.5 EndZ=0
    g33: LineSegment StartX=88.25 StartY=-105 StartZ=0 EndX=88.25 EndY=-76.5 EndZ=0
    g34: GeomPoint [constr] X=47.5 Y=-105 Z=0
    g35: Circle CenterX=-118 CenterY=-93 CenterZ=0 NormalX=0 NormalY=0 NormalZ=1 AngleXU=0 Radius=6
    g36: Circle CenterX=118 CenterY=-93 CenterZ=0 NormalX=0 NormalY=0 NormalZ=1 AngleXU=0 Radius=6
    g37: ArcOfCircle CenterX=-86.75 CenterY=-76.5 CenterZ=0 NormalX=0 NormalY=0 NormalZ=1 AngleXU=0 Radius=1.5 StartAngle=1.5708 EndAngle=3.14159
    g38: ArcOfCircle CenterX=-8.25 CenterY=-76.5 CenterZ=0 NormalX=0 NormalY=0 NormalZ=1 AngleXU=0 Radius=1.5 StartAngle=0 EndAngle=1.5708
    g39: LineSegment StartX=-86.75 StartY=-75 StartZ=0 EndX=-8.25 EndY=-75 EndZ=0
    g40: LineSegment StartX=-88.25 StartY=-105 StartZ=0 EndX=-6.75 EndY=-105 EndZ=0
    g41: LineSegment StartX=-6.75 StartY=-105 StartZ=0 EndX=-6.75 EndY=-76.5 EndZ=0
    g42: LineSegment StartX=-88.25 StartY=-105 StartZ=0 EndX=-88.25 EndY=-76.5 EndZ=0
    g43: GeomPoint [constr] X=-47.5 Y=-105 Z=0
  constraints (95):
    c: Vertical(g0)
    c: Coincident(g0,g1)
    c: Horizontal(g1)
    c: Coincident(g1,g2)
    c: Coincident(g2,g3)
    c: Horizontal(g3)
    c: Coincident(g3,g4)
    c: Vertical(g4)
    c: Coincident(g4,g5)
    c: Coincident(g5,g0)
    c: Vertical(g2)
    c: DistanceY(g2,g2) = 0.5
    c: DistanceX(g5,g5) = 0.5
    c: Tangent(g6,g8) = 1.5708
    c: Tangent(g8,g7) = 1.5708
    c: Equal(g6,g7)
    c: Horizontal(g8)
    c: Horizontal(g9)
    c: Vertical(g11)
    c: Vertical(g10)
    c: Tangent(g6,g11) = 1.5708
    c: Tangent(g7,g10) = -1.5708
    c: Coincident(g11,g9)
    c: Coincident(g9,g10)
    c: Symmetric(g9,g9,g12)
    c: Radius(g7) = 1.5
    c: Distance(g7,g9) = 30
    c: Diameter(g13) = 12
    c: Symmetric(g0,g4,g-2)
    c: DistanceY(g-1,g13) = 93
    c: DistanceX(g13,g-1) = 118
    c: DistanceY(g-1,g9) = 105
    c: DistanceX(g9,g9) = 81.5
    c: DistanceX(g-1,g9) = 6.75
    c: Diameter(g14) = 12
    c: Vertical(g15)
    c: Coincident(g15,g16)
    c: Horizontal(g16)
    c: Coincident(g16,g17)
    c: Coincident(g17,g18)
    c: Horizontal(g18)
    c: Coincident(g18,g19)
    c: Vertical(g19)
    c: Coincident(g19,g20)
    c: Coincident(g20,g15)
    c: Vertical(g17)
    c: Tangent(g21,g23) = -1.5708
    c: Tangent(g23,g22) = -1.5708
    c: Equal(g21,g22)
    c: Horizontal(g23)
    c: Horizontal(g24)
    c: Vertical(g26)
    c: Vertical(g25)
    c: Tangent(g21,g26) = -1.5708
    c: Tangent(g22,g25) = 1.5708
    c: Coincident(g26,g24)
    c: Coincident(g24,g25)
    c: Symmetric(g24,g24,g27)
    c: Radius(g22) = 1.5
    c: Distance(g22,g24) = 30
    c: Tangent(g28,g30) = -1.5708
    c: Tangent(g30,g29) = -1.5708
    c: Equal(g28,g29)
    c: Horizontal(g30)
    c: Horizontal(g31)
    c: Vertical(g33)
    c: Vertical(g32)
    c: Tangent(g28,g33) = -1.5708
    c: Tangent(g29,g32) = 1.5708
    c: Coincident(g33,g31)
    c: Coincident(g31,g32)
    c: Symmetric(g31,g31,g34)
    c: Radius(g29) = 1.5
    c: Distance(g29,g31) = 30
    c: Diameter(g35) = 12
    c: Diameter(g36) = 12
    c: Tangent(g37,g39) = 1.5708
    c: Tangent(g39,g38) = 1.5708
    c: Equal(g37,g38)
    c: Horizontal(g39)
    c: Horizontal(g40)
    c: Vertical(g42)
    c: Vertical(g41)
    c: Tangent(g37,g42) = 1.5708
    c: Tangent(g38,g41) = -1.5708
    c: Coincident(g42,g40)
    c: Coincident(g40,g41)
    c: Symmetric(g40,g40,g43)
    c: Radius(g38) = 1.5
    c: Distance(g38,g40) = 30
    c: Symmetric(g19,g4,g-1)
    c: Horizontal(g20)
    c: Symmetric(g17,g2,g-1)
    c: DistanceY(g17,g17) = 0.5
    c: DistanceY(g16,g1) = 95
FEATURE [PartDesign::Pocket] Pocket006
  BaseFeature = -> Pocket005
  Direction = (0,0,-1)
  Length = 50
  Length2 = 50
  Profile = -> Sketch_2
  ReferenceAxis = -> Sketch_2 [N_Axis]
  Suppressed = false
  Type = 4
FEATURE [Sketcher::SketchObject] Sketch028
  ArcFitTolerance = 0
  FullyConstrained = true
  MakeInternals = false
  MapMode = 5
  Placement = pos=(0,-75,0) rot=(1,0,0;1.5708rad)
  sketch-geometry (1):
    g0: Circle CenterX=74 CenterY=-21.75 CenterZ=0 NormalX=0 NormalY=0 NormalZ=1 AngleXU=0 Radius=6
  constraints (3):
    c: Diameter(g0) = 12
    c: DistanceY(g0,g-1) = 21.75
    c: DistanceX(g-1,g0) = 74
FEATURE [PartDesign::Pocket] Pocket011
  BaseFeature = -> Pocket006
  Direction = (0,1,-2e-16)
  Length = 5
  Length2 = 5
  Profile = -> Sketch028
  ReferenceAxis = -> Sketch028 [N_Axis]
  Suppressed = false
  Type = 1
FEATURE [PartDesign::Body] Body061  label="перегородка"
  AllowCompound = false
  Group = -> [Sketch022,Sketch021,Pad012,Pad013,Sketch_1,Pocket005,Block_ribb,Sketch_2,Pocket006,Sketch028,Pocket011]
  Origin = -> Origin062
  Tip = -> Pocket011
FEATURE [PartDesign::Pad] Pad017
  Direction = (0,0,1)
  Length = 37
  Length2 = 22.5
  Profile = -> Sketch021
  ReferenceAxis = -> Sketch021 [N_Axis]
  Reversed = true
  Suppressed = false
  Type = 4
FEATURE [PartDesign::Pocket] Pocket017
  BaseFeature = -> Pad017
  Direction = (0,0,-1)
  Length = 8.5
  Length2 = 13
  Profile = -> Sketch_1
  ReferenceAxis = -> Sketch_1 [N_Axis]
  Suppressed = false
  Type = 4
FEATURE [PartDesign::CoordinateSystem] Block_ribb001
  AttacherType = Attacher::AttachEngine3D
  AttachmentSupport = -> [Pocket017]
  MapMode = 2
FEATURE [PartDesign::Pocket] Pocket018
  BaseFeature = -> Pocket017
  Direction = (0,0,-1)
  Length = 50
  Length2 = 50
  Profile = -> Sketch_2
  ReferenceAxis = -> Sketch_2 [N_Axis]
  Suppressed = false
  Type = 4
FEATURE [PartDesign::Pocket] Pocket019
  BaseFeature = -> Pocket018
  Direction = (0,1,-2e-16)
  Length = 5
  Length2 = 5
  Profile = -> Sketch028
  ReferenceAxis = -> Sketch028 [N_Axis]
  Suppressed = false
  Type = 1
FEATURE [Sketcher::SketchObject] Sketch034
  ArcFitTolerance = 0
  AttachmentSupport = -> [XY_Plane062]
  FullyConstrained = false
  MakeInternals = false
  MapMode = 5
  sketch-geometry (4):
    g0: LineSegment StartX=-154.224 StartY=65.5 StartZ=0 EndX=161.628 EndY=65.5 EndZ=0
    g1: LineSegment StartX=161.628 StartY=65.5 StartZ=0 EndX=161.628 EndY=-65.5 EndZ=0
    g2: LineSegment StartX=161.628 StartY=-65.5 StartZ=0 EndX=-154.224 EndY=-65.5 EndZ=0
    g3: LineSegment StartX=-154.224 StartY=-65.5 StartZ=0 EndX=-154.224 EndY=65.5 EndZ=0
  constraints (9):
    c: Coincident(g0,g1)
    c: Coincident(g1,g2)
    c: Coincident(g2,g3)
    c: Coincident(g3,g0)
    c: Horizontal(g0)
    c: Horizontal(g2)
    c: Vertical(g3)
    c: Symmetric(g1,g0,g-1)
    c: DistanceY(g1,g1) = 131
FEATURE [PartDesign::Pocket] Pocket020
  BaseFeature = -> Pocket019
  Direction = (0,0,-1)
  Length = 25
  Length2 = -10.5
  Profile = -> Sketch034
  ReferenceAxis = -> Sketch034 [N_Axis]
  Reversed = true
  Suppressed = false
  Type = 4
FEATURE [PartDesign::Body] Body063  label="Перегородка_передняя"
  AllowCompound = false
  Group = -> [Pad017,Pocket017,Block_ribb001,Pocket018,Pocket019,Sketch034,Pocket020]
  Origin = -> Origin064
  Tip = -> Pocket020
FEATURE [PartDesign::CoordinateSystem] Block_ribb002
  AttacherType = Attacher::AttachEngine3D
  MapMode = 2
FEATURE [PartDesign::Pad] Pad018
  Direction = (0,0,1)
  Length = 12.5
  Length2 = 12.5
  Profile = -> Sketch021
  ReferenceAxis = -> Sketch021 [N_Axis]
  Reversed = true
  Suppressed = false
  Type = 4
FEATURE [Sketcher::SketchObject] Sketch035
  ArcFitTolerance = 0
  FullyConstrained = false
  MakeInternals = false
  MapMode = 5
  sketch-geometry (9):
    g0: LineSegment [constr] StartX=-110 StartY=-105 StartZ=0 EndX=-65.5 EndY=-105 EndZ=0
    g1: LineSegment [constr] StartX=-65.5 StartY=-105 StartZ=0 EndX=-65.5 EndY=105 EndZ=0
    g2: LineSegment [constr] StartX=-65.5 StartY=105 StartZ=0 EndX=-110 EndY=105 EndZ=0
    g3: LineSegment [constr] StartX=-110 StartY=105 StartZ=0 EndX=-110 EndY=-105 EndZ=0
    g4: LineSegment [constr] StartX=65.5 StartY=52.7372 StartZ=0 EndX=65.5 EndY=105 EndZ=0
    g5: LineSegment StartX=-110 StartY=-105 StartZ=0 EndX=65.5 EndY=-105 EndZ=0
    g6: LineSegment StartX=65.5 StartY=-105 StartZ=0 EndX=65.5 EndY=105 EndZ=0
    g7: LineSegment StartX=65.5 StartY=105 StartZ=0 EndX=-110 EndY=105 EndZ=0
    g8: LineSegment StartX=-110 StartY=105 StartZ=0 EndX=-110 EndY=-105 EndZ=0
  constraints (23):
    c: Coincident(g0,g1)
    c: Coincident(g1,g2)
    c: Coincident(g2,g3)
    c: Coincident(g3,g0)
    c: Horizontal(g0)
    c: Horizontal(g2)
    c: Vertical(g3)
    c: Vertical(g4)
    c: DistanceX(g1,g4) = 131
    c: Symmetric(g1,g4,g-2)
    c: DistanceY(g1,g1) = 210
    c: DistanceX(g0,g0) = 44.5
    c: Symmetric(g0,g1,g-1)
    c: Coincident(g5,g6)
    c: Coincident(g6,g7)
    c: Coincident(g7,g8)
    c: Coincident(g8,g5)
    c: Horizontal(g5)
    c: Horizontal(g7)
    c: Vertical(g6)
    c: Vertical(g8)
    c: Coincident(g5,g0)
    c: Coincident(g6,g4)
FEATURE [Sketcher::SketchObject] Sketch_004
  ArcFitTolerance = 0
  FullyConstrained = false
  MakeInternals = false
  sketch-geometry (32):
    g0: ArcOfCircle CenterX=86.75 CenterY=76.5 CenterZ=0 NormalX=0 NormalY=0 NormalZ=1 AngleXU=0 Radius=1.5 StartAngle=4.71239 EndAngle=6.28319
    g1: ArcOfCircle CenterX=8.25 CenterY=76.5 CenterZ=0 NormalX=0 NormalY=0 NormalZ=1 AngleXU=0 Radius=1.5 StartAngle=3.14159 EndAngle=4.71239
    g2: LineSegment StartX=86.75 StartY=75 StartZ=0 EndX=8.25 EndY=75 EndZ=0
    g3: LineSegment StartX=88.25 StartY=105 StartZ=0 EndX=6.75 EndY=105 EndZ=0
    g4: LineSegment StartX=6.75 StartY=105 StartZ=0 EndX=6.75 EndY=76.5 EndZ=0
    g5: LineSegment StartX=88.25 StartY=105 StartZ=0 EndX=88.25 EndY=76.5 EndZ=0
    g6: GeomPoint [constr] X=47.5 Y=105 Z=0
    g7: Circle CenterX=-118 CenterY=93 CenterZ=0 NormalX=0 NormalY=0 NormalZ=1 AngleXU=0 Radius=6
    g8: Circle CenterX=118 CenterY=93 CenterZ=0 NormalX=0 NormalY=0 NormalZ=1 AngleXU=0 Radius=6
    g9: ArcOfCircle CenterX=-86.75 CenterY=76.5 CenterZ=0 NormalX=0 NormalY=0 NormalZ=1 AngleXU=0 Radius=1.5 StartAngle=3.14159 EndAngle=4.71239
    g10: ArcOfCircle CenterX=-8.25 CenterY=76.5 CenterZ=0 NormalX=0 NormalY=0 NormalZ=1 AngleXU=0 Radius=1.5 StartAngle=4.71239 EndAngle=6.28319
    g11: LineSegment StartX=-86.75 StartY=75 StartZ=0 EndX=-8.25 EndY=75 EndZ=0
    g12: LineSegment StartX=-88.25 StartY=105 StartZ=0 EndX=-6.75 EndY=105 EndZ=0
    g13: LineSegment StartX=-6.75 StartY=105 StartZ=0 EndX=-6.75 EndY=76.5 EndZ=0
    g14: LineSegment StartX=-88.25 StartY=105 StartZ=0 EndX=-88.25 EndY=76.5 EndZ=0
    g15: GeomPoint [constr] X=-47.5 Y=105 Z=0
    g16: ArcOfCircle CenterX=86.75 CenterY=-76.5 CenterZ=0 NormalX=0 NormalY=0 NormalZ=1 AngleXU=0 Radius=1.5 StartAngle=0 EndAngle=1.5708
    g17: ArcOfCircle CenterX=8.25 CenterY=-76.5 CenterZ=0 NormalX=0 NormalY=0 NormalZ=1 AngleXU=0 Radius=1.5 StartAngle=1.5708 EndAngle=3.14159
    g18: LineSegment StartX=86.75 StartY=-75 StartZ=0 EndX=8.25 EndY=-75 EndZ=0
    g19: LineSegment StartX=88.25 StartY=-105 StartZ=0 EndX=6.75 EndY=-105 EndZ=0
    g20: LineSegment StartX=6.75 StartY=-105 StartZ=0 EndX=6.75 EndY=-76.5 EndZ=0
    g21: LineSegment StartX=88.25 StartY=-105 StartZ=0 EndX=88.25 EndY=-76.5 EndZ=0
    g22: GeomPoint [constr] X=47.5 Y=-105 Z=0
    g23: Circle CenterX=-118 CenterY=-93 CenterZ=0 NormalX=0 NormalY=0 NormalZ=1 AngleXU=0 Radius=6
    g24: Circle CenterX=118 CenterY=-93 CenterZ=0 NormalX=0 NormalY=0 NormalZ=1 AngleXU=0 Radius=6
    g25: ArcOfCircle CenterX=-86.75 CenterY=-76.5 CenterZ=0 NormalX=0 NormalY=0 NormalZ=1 AngleXU=0 Radius=1.5 StartAngle=1.5708 EndAngle=3.14159
    g26: ArcOfCircle CenterX=-8.25 CenterY=-76.5 CenterZ=0 NormalX=0 NormalY=0 NormalZ=1 AngleXU=0 Radius=1.5 StartAngle=0 EndAngle=1.5708
    g27: LineSegment StartX=-86.75 StartY=-75 StartZ=0 EndX=-8.25 EndY=-75 EndZ=0
    g28: LineSegment StartX=-88.25 StartY=-105 StartZ=0 EndX=-6.75 EndY=-105 EndZ=0
    g29: LineSegment StartX=-6.75 StartY=-105 StartZ=0 EndX=-6.75 EndY=-76.5 EndZ=0
    g30: LineSegment StartX=-88.25 StartY=-105 StartZ=0 EndX=-88.25 EndY=-76.5 EndZ=0
    g31: GeomPoint [constr] X=-47.5 Y=-105 Z=0
  constraints (65):
    c: Tangent(g0,g2) = 1.5708
    c: Tangent(g2,g1) = 1.5708
    c: Equal(g0,g1)
    c: Horizontal(g2)
    c: Horizontal(g3)
    c: Vertical(g5)
    c: Vertical(g4)
    c: Tangent(g0,g5) = 1.5708
    c: Tangent(g1,g4) = -1.5708
    c: Coincident(g5,g3)
    c: Coincident(g3,g4)
    c: Symmetric(g3,g3,g6)
    c: Radius(g1) = 1.5
    c: Distance(g1,g3) = 30
    c: Diameter(g7) = 12
    c: DistanceY(g-1,g7) = 93
    c: DistanceX(g7,g-1) = 118
    c: DistanceY(g-1,g3) = 105
    c: DistanceX(g3,g3) = 81.5
    c: DistanceX(g-1,g3) = 6.75
    c: Diameter(g8) = 12
    c: Tangent(g9,g11) = -1.5708
    c: Tangent(g11,g10) = -1.5708
    c: Equal(g9,g10)
    c: Horizontal(g11)
    c: Horizontal(g12)
    c: Vertical(g14)
    c: Vertical(g13)
    c: Tangent(g9,g14) = -1.5708
    c: Tangent(g10,g13) = 1.5708
    c: Coincident(g14,g12)
    c: Coincident(g12,g13)
    c: Symmetric(g12,g12,g15)
    c: Radius(g10) = 1.5
    c: Distance(g10,g12) = 30
    c: Tangent(g16,g18) = -1.5708
    c: Tangent(g18,g17) = -1.5708
    c: Equal(g16,g17)
    c: Horizontal(g18)
    c: Horizontal(g19)
    c: Vertical(g21)
    c: Vertical(g20)
    c: Tangent(g16,g21) = -1.5708
    c: Tangent(g17,g20) = 1.5708
    c: Coincident(g21,g19)
    c: Coincident(g19,g20)
    c: Symmetric(g19,g19,g22)
    c: Radius(g17) = 1.5
    c: Distance(g17,g19) = 30
    c: Diameter(g23) = 12
    c: Diameter(g24) = 12
    c: Tangent(g25,g27) = 1.5708
    c: Tangent(g27,g26) = 1.5708
    c: Equal(g25,g26)
    c: Horizontal(g27)
    c: Horizontal(g28)
    c: Vertical(g30)
    c: Vertical(g29)
    c: Tangent(g25,g30) = 1.5708
    c: Tangent(g26,g29) = -1.5708
    c: Coincident(g30,g28)
    c: Coincident(g28,g29)
    c: Symmetric(g28,g28,g31)
    c: Radius(g26) = 1.5
    c: Distance(g26,g28) = 30
FEATURE [PartDesign::Pocket] Pocket021
  BaseFeature = -> Pad018
  Direction = (0,0,-1)
  Length = 20
  Length2 = 20
  Profile = -> Sketch_004
  ReferenceAxis = -> Sketch_004 [N_Axis]
  Suppressed = false
  Type = 4
FEATURE [PartDesign::Pocket] Pocket022
  BaseFeature = -> Pocket021
  Direction = (0,0,-1)
  Length = 20
  Length2 = 20
  Profile = -> Sketch035
  ReferenceAxis = -> Sketch035 [N_Axis]
  Suppressed = false
  Type = 4
FEATURE [PartDesign::Body] Body064  label="перегородка_ползуна"
  AllowCompound = false
  Group = -> [Sketch035,Pad018,Block_ribb002,Sketch_004,Pocket021,Pocket022]
  Origin = -> Origin065
  Tip = -> Pocket022
FEATURE [Sketcher::SketchObject] Sketch038
  ArcFitTolerance = 0
  FullyConstrained = true
  MakeInternals = false
  MapMode = 5
  sketch-geometry (26):
    g0: LineSegment [constr] StartX=-103 StartY=-65 StartZ=0 EndX=103 EndY=-65 EndZ=0
    g1: LineSegment StartX=103 StartY=-65 StartZ=0 EndX=103 EndY=65 EndZ=0
    g2: LineSegment [constr] StartX=103 StartY=65 StartZ=0 EndX=-103 EndY=65 EndZ=0
    g3: LineSegment StartX=-103 StartY=65 StartZ=0 EndX=-103 EndY=-65 EndZ=0
    g4: ArcOfCircle CenterX=0 CenterY=40 CenterZ=0 NormalX=0 NormalY=0 NormalZ=1 AngleXU=0 Radius=20.25 StartAngle=1.05267 EndAngle=2.08892
    g5: ArcOfCircle CenterX=0 CenterY=0 CenterZ=0 NormalX=0 NormalY=0 NormalZ=1 AngleXU=0 Radius=55 StartAngle=2.08892 EndAngle=4.19427
    g6: ArcOfCircle CenterX=0 CenterY=0 CenterZ=0 NormalX=0 NormalY=0 NormalZ=1 AngleXU=0 Radius=55 StartAngle=5.23051 EndAngle=7.33586
    g7: ArcOfCircle CenterX=0 CenterY=-40 CenterZ=0 NormalX=0 NormalY=0 NormalZ=1 AngleXU=0 Radius=20.25 StartAngle=4.19427 EndAngle=5.23051
    g8: LineSegment StartX=-27.2388 StartY=47.7813 StartZ=0 EndX=-10.0288 EndY=57.5922 EndZ=0
    g9: LineSegment StartX=10.0288 StartY=57.5922 StartZ=0 EndX=27.2388 EndY=47.7813 EndZ=0
    g10: LineSegment StartX=-27.2388 StartY=-47.7812 StartZ=0 EndX=-10.0288 EndY=-57.5922 EndZ=0
    g11: LineSegment StartX=10.0288 StartY=-57.5922 StartZ=0 EndX=27.2388 EndY=-47.7812 EndZ=0
    g12: LineSegment StartX=-99 StartY=69.5 StartZ=0 EndX=99 EndY=69.5 EndZ=0
    g13: LineSegment StartX=-103 StartY=65 StartZ=0 EndX=-103 EndY=65.5 EndZ=0
    g14: LineSegment StartX=103 StartY=65.5 StartZ=0 EndX=103 EndY=65 EndZ=0
    g15: ArcOfCircle CenterX=-99 CenterY=65.5 CenterZ=0 NormalX=0 NormalY=0 NormalZ=1 AngleXU=0 Radius=4 StartAngle=1.5708 EndAngle=3.14159
    g16: ArcOfCircle CenterX=99 CenterY=65.5 CenterZ=0 NormalX=0 NormalY=0 NormalZ=1 AngleXU=0 Radius=4 StartAngle=4e-16 EndAngle=1.5708
    g17: ArcOfCircle CenterX=-99 CenterY=-65.5 CenterZ=0 NormalX=0 NormalY=0 NormalZ=1 AngleXU=0 Radius=4 StartAngle=3.14159 EndAngle=4.71239
    g18: LineSegment StartX=-103 StartY=-65 StartZ=0 EndX=-103 EndY=-65.5 EndZ=0
    g19: LineSegment StartX=-99 StartY=-69.5 StartZ=0 EndX=99 EndY=-69.5 EndZ=0
    g20: ArcOfCircle CenterX=99 CenterY=-65.5 CenterZ=0 NormalX=0 NormalY=0 NormalZ=1 AngleXU=0 Radius=4 StartAngle=4.71239 EndAngle=6.28319
    g21: LineSegment StartX=103 StartY=-65.5 StartZ=0 EndX=103 EndY=-65 EndZ=0
    g22: Circle CenterX=-95 CenterY=55 CenterZ=0 NormalX=0 NormalY=0 NormalZ=1 AngleXU=0 Radius=3
    g23: Circle CenterX=95 CenterY=55 CenterZ=0 NormalX=0 NormalY=0 NormalZ=1 AngleXU=0 Radius=3
    g24: Circle CenterX=-95 CenterY=-55 CenterZ=0 NormalX=0 NormalY=0 NormalZ=1 AngleXU=0 Radius=3
    g25: Circle CenterX=95 CenterY=-55 CenterZ=0 NormalX=0 NormalY=0 NormalZ=1 AngleXU=0 Radius=3
  constraints (58):
    c: Coincident(g0,g1)
    c: Coincident(g1,g2)
    c: Coincident(g2,g3)
    c: Coincident(g3,g0)
    c: Horizontal(g0)
    c: Vertical(g1)
    c: Symmetric(g2,g1,g-2)
    c: Symmetric(g2,g0,g-1)
    c: DistanceX(g2,g2) = 206
    c: PointOnObject(g4,g-2)
    c: Diameter(g4) = 40.5
    c: Equal(g4,g7)
    c: Symmetric(g4,g7,g-1)
    c: Equal(g5,g6)
    c: Tangent(g5,g10) = -1.5708
    c: Tangent(g5,g8) = 1.5708
    c: Tangent(g4,g8) = 1.5708
    c: Tangent(g4,g9) = 1.5708
    c: Tangent(g7,g11) = -1.5708
    c: Tangent(g7,g10) = -1.5708
    c: Tangent(g6,g9) = 1.5708
    c: Tangent(g6,g11) = -1.5708
    c: Distance(g-1,g4) = 40
    c: DistanceY(g1,g1) = 130
    c: Radius(g6) = 55
    c: Coincident(g5,g-1)
    c: Coincident(g6,g5)
    c: Coincident(g13,g3)
    c: Coincident(g14,g1)
    c: Tangent(g13,g15) = 1.5708
    c: Tangent(g12,g15) = 1.5708
    c: Tangent(g12,g16) = 1.5708
    c: Tangent(g14,g16) = 1.5708
    c: Vertical(g13)
    c: Vertical(g14)
    c: Symmetric(g15,g16,g-2)
    c: DistanceY(g1,g12) = 4.5
    c: Radius(g16) = 4
    c: Tangent(g18,g17) = -1.5708
    c: Tangent(g19,g17) = -1.5708
    c: Tangent(g19,g20) = -1.5708
    c: Vertical(g18)
    c: Symmetric(g17,g20,g-2)
    c: Symmetric(g17,g15,g-1)
    c: Coincident(g18,g3)
    c: Coincident(g21,g1)
    c: Vertical(g21)
    c: Equal(g21,g18)
    c: Coincident(g20,g21)
    c: Equal(g22,g23)
    c: Equal(g23,g25)
    c: Equal(g25,g24)
    c: Diameter(g23) = 6
    c: Symmetric(g22,g23,g-2)
    c: Symmetric(g24,g25,g-2)
    c: Symmetric(g24,g22,g-1)
    c: DistanceY(g24,g22) = 110
    c: DistanceX(g24,g25) = 190
FEATURE [PartDesign::Pad] Pad020
  Direction = (0,0,1)
  Length = 22.5
  Length2 = 5.5
  Midplane = true
  Profile = -> Sketch038
  ReferenceAxis = -> Sketch038 [N_Axis]
  Suppressed = false
  Type = 4
FEATURE [PartDesign::CoordinateSystem] Shtok003
  AttacherType = Attacher::AttachEngine3D
  AttachmentSupport = -> [Sketch038]
  MapMode = 2
FEATURE [PartDesign::CoordinateSystem] Piston001
  AttacherType = Attacher::AttachEngine3D
  AttachmentSupport = -> [XZ_Plane071]
  MapMode = 2
  Placement = pos=(0,0,0) rot=(1,0,0;1.5708rad)
FEATURE [Sketcher::SketchObject] Sketch041
  ArcFitTolerance = 0
  AttachmentSupport = -> [XY_Plane069]
  FullyConstrained = true
  MakeInternals = false
  MapMode = 5
  sketch-geometry (6):
    g0: Circle [constr] CenterX=0 CenterY=85 CenterZ=0 NormalX=0 NormalY=0 NormalZ=1 AngleXU=0 Radius=11.5
    g1: LineSegment StartX=-45.5 StartY=147 StartZ=0 EndX=45.5 EndY=147 EndZ=0
    g2: LineSegment StartX=-45.5 StartY=147 StartZ=0 EndX=-45.5 EndY=51 EndZ=0
    g3: LineSegment StartX=0 StartY=51 StartZ=0 EndX=-45.5 EndY=51 EndZ=0
    g4: LineSegment StartX=45.5 StartY=147 StartZ=0 EndX=45.5 EndY=51 EndZ=0
    g5: LineSegment StartX=0 StartY=51 StartZ=0 EndX=45.5 EndY=51 EndZ=0
  constraints (15):
    c: Coincident(g2,g1)
    c: Vertical(g2)
    c: Symmetric(g1,g1,g-2)
    c: DistanceX(g1,g1) = 91
    c: PointOnObject(g3,g-2)
    c: Vertical(g4)
    c: Block(g0)
    c: Coincident(g1,g4)
    c: DistanceY(g0,g1) = 62
    c: DistanceY(g3,g0) = 34
    c: Horizontal(g3)
    c: Coincident(g2,g3)
    c: Coincident(g5,g3)
    c: Coincident(g5,g4)
    c: Horizontal(g5)
FEATURE [PartDesign::Pad] Pad021
  Direction = (0,0,1)
  Length = 100
  Length2 = 10
  Midplane = true
  Profile = -> Sketch041
  ReferenceAxis = -> Sketch041 [N_Axis]
  Suppressed = false
  Type = 0
FEATURE [PartDesign::Body] Body070  label="Поршень003"
  AllowCompound = false
  Group = -> [Sketch041,Pad021]
  Origin = -> Origin071
  Tip = -> Pad021
FEATURE [Sketcher::SketchObject] Sketch042
  ArcFitTolerance = 0
  AttachmentSupport = -> [XZ_Plane071]
  FullyConstrained = false
  MakeInternals = false
  MapMode = 5
  Placement = pos=(0,0,0) rot=(1,0,0;1.5708rad)
  sketch-geometry (2):
    g0: GeomPoint [constr] X=-87.5 Y=-1.47e-14 Z=0
    g1: Circle CenterX=0 CenterY=0 CenterZ=0 NormalX=0 NormalY=0 NormalZ=1 AngleXU=0 Radius=45.5
  constraints (2):
    c: Coincident(g1,g-1)
    c: Diameter(g1) = 91
FEATURE [PartDesign::Pad] Pad022
  Direction = (0,-1,2e-16)
  Length = 200
  Length2 = 10
  Placement = pos=(0,0,0) rot=(1,0,0;1.5708rad)
  Profile = -> Sketch042
  ReferenceAxis = -> Sketch042 [N_Axis]
  Reversed = true
  Suppressed = false
  Type = 0
FEATURE [PartDesign::Boolean] Boolean004
  BaseFeature = -> Pad022
  Group = -> [Body070]
  Suppressed = false
  Type = 2
  UsePlacement = false
FEATURE [Sketcher::SketchObject] Sketch043
  ArcFitTolerance = 0
  FullyConstrained = true
  MakeInternals = false
  MapMode = 5
  Placement = pos=(0,0,0) rot=(1,0,0;1.5708rad)
  sketch-geometry (2):
    g0: Circle CenterX=0 CenterY=0 CenterZ=0 NormalX=0 NormalY=0 NormalZ=1 AngleXU=0 Radius=41
    g1: Circle CenterX=0 CenterY=0 CenterZ=0 NormalX=0 NormalY=0 NormalZ=1 AngleXU=0 Radius=15
  constraints (4):
    c: Coincident(g0,g-1)
    c: Diameter(g0) = 82
    c: Coincident(g1,g0)
    c: Diameter(g1) = 30
FEATURE [PartDesign::Pocket] Pocket025
  BaseFeature = -> Boolean004
  Direction = (0,1,-2e-16)
  Length = 138
  Length2 = 5
  Profile = -> Sketch043
  ReferenceAxis = -> Sketch043 [N_Axis]
  Suppressed = false
  Type = 0
FEATURE [Sketcher::SketchObject] Sketch044
  ArcFitTolerance = 0
  AttachmentSupport = -> [XZ_Plane071]
  FullyConstrained = false
  MakeInternals = false
  MapMode = 5
  Placement = pos=(0,0,0) rot=(1,0,0;1.5708rad)
  sketch-geometry (3):
    g0: GeomPoint [constr] X=-87.5 Y=-1.47e-14 Z=0
    g1: Circle CenterX=0 CenterY=0 CenterZ=0 NormalX=0 NormalY=0 NormalZ=1 AngleXU=0 Radius=43
    g2: Circle CenterX=0 CenterY=0 CenterZ=0 NormalX=0 NormalY=0 NormalZ=1 AngleXU=0 Radius=47.5
  constraints (4):
    c: Coincident(g1,g-1)
    c: Coincident(g2,g1)
    c: Diameter(g1) = 86
    c: Diameter(g2) = 95
FEATURE [PartDesign::Pocket] Pocket026  label="Pocket002-ring002"
  BaseFeature = -> Pocket025
  Direction = (0,1,-2e-16)
  Length = 143
  Length2 = -141
  Profile = -> Sketch044
  ReferenceAxis = -> Sketch044 [N_Axis]
  Suppressed = false
  Type = 4
FEATURE [PartDesign::Pocket] Pocket027  label="Pocket003-ring003"
  BaseFeature = -> Pocket026
  Direction = (0,1,-2e-16)
  Length = 138
  Length2 = -136
  Profile = -> Sketch044
  ReferenceAxis = -> Sketch044 [N_Axis]
  Suppressed = false
  Type = 4
FEATURE [PartDesign::Pocket] Pocket028  label="Pocket004-komp-ring001"
  BaseFeature = -> Pocket027
  Direction = (0,1,-2e-16)
  Length = 55
  Length2 = -58
  Profile = -> Sketch044
  ReferenceAxis = -> Sketch044 [N_Axis]
  Suppressed = false
  Type = 4
FEATURE [Sketcher::SketchObject] Sketch045
  ArcFitTolerance = 0
  AttachmentSupport = -> [XY_Plane072]
  FullyConstrained = true
  MakeInternals = false
  MapMode = 5
  sketch-geometry (11):
    g0: LineSegment [constr] StartX=-120 StartY=252 StartZ=0 EndX=120 EndY=252 EndZ=0
    g1: LineSegment [constr] StartX=120 StartY=252 StartZ=0 EndX=120 EndY=-252 EndZ=0
    g2: LineSegment StartX=120 StartY=-252 StartZ=0 EndX=-120 EndY=-252 EndZ=0
    g3: LineSegment [constr] StartX=-120 StartY=-252 StartZ=0 EndX=-120 EndY=252 EndZ=0
    g4: LineSegment [constr] StartX=-120 StartY=252 StartZ=0 EndX=-120 EndY=75.5 EndZ=0
    g5: LineSegment [constr] StartX=-120 StartY=75.5 StartZ=0 EndX=120 EndY=75.5 EndZ=0
    g6: LineSegment [constr] StartX=120 StartY=75.5 StartZ=0 EndX=120 EndY=252 EndZ=0
    g7: LineSegment StartX=-120 StartY=-252 StartZ=0 EndX=-120 EndY=-75.5 EndZ=0
    g8: LineSegment StartX=-120 StartY=-75.5 StartZ=0 EndX=120 EndY=-75.5 EndZ=0
    g9: LineSegment [constr] StartX=120 StartY=-75.5 StartZ=0 EndX=120 EndY=-252 EndZ=0
    g10: LineSegment StartX=120 StartY=-75.5 StartZ=0 EndX=120 EndY=-252 EndZ=0
  constraints (28):
    c: Coincident(g0,g1)
    c: Coincident(g1,g2)
    c: Coincident(g2,g3)
    c: Coincident(g3,g0)
    c: Horizontal(g2)
    c: Vertical(g1)
    c: Symmetric(g0,g0,g-2)
    c: Symmetric(g0,g2,g-1)
    c: Coincident(g0,g4)
    c: PointOnObject(g4,g3)
    c: Coincident(g4,g5)
    c: PointOnObject(g5,g1)
    c: Horizontal(g5)
    c: Coincident(g5,g6)
    c: Coincident(g6,g0)
    c: Coincident(g2,g7)
    c: PointOnObject(g7,g3)
    c: Coincident(g7,g8)
    c: PointOnObject(g8,g1)
    c: Horizontal(g8)
    c: Coincident(g8,g9)
    c: Coincident(g9,g2)
    c: Equal(g9,g6)
    c: DistanceX(g2,g2) = 240
    c: Coincident(g10,g8)
    c: Coincident(g10,g2)
    c: DistanceY(g2,g-1) = 252
    c: DistanceY(g7,g7) = 176.5
FEATURE [PartDesign::Pad] Pad024
  Direction = (0,0,1)
  Length = 28
  Length2 = 78
  Midplane = true
  Profile = -> Sketch045
  ReferenceAxis = -> Sketch045 [N_Axis]
  Suppressed = false
  Type = 4
FEATURE [PartDesign::Body] Body073
  AllowCompound = false
  Group = -> [Sketch045,Pad024]
  Origin = -> Origin074
  Placement = pos=(0,0,25) rot=(0,0,1;0rad)
  Tip = -> Pad024
FEATURE [PartDesign::CoordinateSystem] Cylynder001
  AttacherType = Attacher::AttachEngine3D
  AttachmentSupport = -> [Body073]
  MapMode = 2
  Placement = pos=(0,0,25) rot=(0,0,1;0rad)
FEATURE [Sketcher::SketchObject] Sketch046
  ArcFitTolerance = 0
  AttachmentSupport = -> [XZ_Plane072]
  FullyConstrained = false
  MakeInternals = false
  MapMode = 5
  Placement = pos=(0,0,0) rot=(1,0,0;1.5708rad)
  sketch-geometry (12):
    g0: ArcOfCircle [constr] CenterX=-53 CenterY=1.3e-15 CenterZ=0 NormalX=0 NormalY=0 NormalZ=1 AngleXU=0 Radius=46 StartAngle=1.5708 EndAngle=4.71239
    g1: ArcOfCircle [constr] CenterX=0 CenterY=0 CenterZ=0 NormalX=0 NormalY=0 NormalZ=1 AngleXU=0 Radius=46 StartAngle=4.71239 EndAngle=7.85398
    g2: LineSegment [constr] StartX=-53 StartY=-46 StartZ=0 EndX=-7.1e-15 EndY=-46 EndZ=0
    g3: LineSegment [constr] StartX=1.41e-14 StartY=46 StartZ=0 EndX=-53 EndY=46 EndZ=0
    g4: LineSegment StartX=-222.305 StartY=100 StartZ=0 EndX=222.305 EndY=100 EndZ=0
    g5: LineSegment StartX=222.305 StartY=100 StartZ=0 EndX=222.305 EndY=-100 EndZ=0
    g6: LineSegment StartX=222.305 StartY=-100 StartZ=0 EndX=-222.305 EndY=-100 EndZ=0
    g7: LineSegment StartX=-222.305 StartY=-100 StartZ=0 EndX=-222.305 EndY=100 EndZ=0
    g8: Circle CenterX=-53 CenterY=1.3e-15 CenterZ=0 NormalX=0 NormalY=0 NormalZ=1 AngleXU=0 Radius=46
    g9: Circle [constr] CenterX=0 CenterY=0 CenterZ=0 NormalX=0 NormalY=0 NormalZ=1 AngleXU=0 Radius=46
    g10: Circle CenterX=53 CenterY=0 CenterZ=0 NormalX=0 NormalY=0 NormalZ=1 AngleXU=0 Radius=46
    g11: LineSegment [constr] StartX=1.41e-14 StartY=46 StartZ=0 EndX=53 EndY=46 EndZ=0
  constraints (28):
    c: Tangent(g0,g2) = -1.5708
    c: Tangent(g2,g1) = -1.5708
    c: Tangent(g1,g3) = -1.5708
    c: Tangent(g3,g0) = -1.5708
    c: Equal(g0,g1)
    c: Horizontal(g2)
    c: DistanceY(g0,g0) = 92
    c: Coincident(g4,g5)
    c: Coincident(g5,g6)
    c: Coincident(g6,g7)
    c: Coincident(g7,g4)
    c: Horizontal(g6)
    c: Vertical(g7)
    c: DistanceY(g5,g5) = 200
    c: Symmetric(g5,g4,g-1)
    c: Symmetric(g4,g4,g-2)
    c: Coincident(g8,g0)
    c: Coincident(g9,g1)
    c: Equal(g8,g0)
    c: Equal(g9,g1)
    c: Coincident(g9,g-1)
    c: PointOnObject(g10,g-1)
    c: Equal(g9,g10)
    c: Coincident(g11,g1)
    c: PointOnObject(g11,g10)
    c: Horizontal(g11)
    c: Equal(g3,g11)
    c: DistanceX(g8,g10) = 106
FEATURE [PartDesign::Pad] Pad023
  Direction = (0,-1,2e-16)
  Length = 300
  Length2 = 10
  Placement = pos=(0,0,0) rot=(1,0,0;1.5708rad)
  Profile = -> Sketch046
  ReferenceAxis = -> Sketch046 [N_Axis]
  Suppressed = false
  Type = 0
FEATURE [PartDesign::Boolean] Boolean005
  BaseFeature = -> Pad023
  Group = -> [Body073]
  Suppressed = false
  Type = 2
  UsePlacement = false
FEATURE [Sketcher::SketchObject] Sketch047
  ArcFitTolerance = 0
  AttachmentSupport = -> [XY_Plane071]
  FullyConstrained = true
  MakeInternals = false
  MapMode = 5
  sketch-geometry (2):
    g0: Circle CenterX=-137 CenterY=-90 CenterZ=0 NormalX=0 NormalY=0 NormalZ=1 AngleXU=0 Radius=30.5
    g1: Circle CenterX=137 CenterY=-90 CenterZ=0 NormalX=0 NormalY=0 NormalZ=1 AngleXU=0 Radius=30.5
  constraints (5):
    c: Diameter(g0) = 61
    c: Symmetric(g0,g1,g-2)
    c: DistanceY(g0,g-1) = 90
    c: DistanceX(g0,g1) = 274
    c: Equal(g1,g0)
FEATURE [Sketcher::SketchObject] Sketch048
  ArcFitTolerance = 0
  AttachmentSupport = -> [XY_Plane071]
  FullyConstrained = false
  MakeInternals = false
  MapMode = 5
  sketch-geometry (17):
    g0: LineSegment [constr] StartX=72.5228 StartY=-25.9373 StartZ=0 EndX=72.5228 EndY=-109 EndZ=0
    g1: LineSegment [constr] StartX=72.5228 StartY=-109 StartZ=0 EndX=-72.5228 EndY=-109 EndZ=0
    g2: LineSegment [constr] StartX=-72.5228 StartY=-109 StartZ=0 EndX=-72.5228 EndY=-25.9373 EndZ=0
    g3: LineSegment StartX=-72.5228 StartY=-25.9373 StartZ=0 EndX=-160.839 EndY=-25.9373 EndZ=0
    g4: LineSegment StartX=-160.839 StartY=-25.9373 StartZ=0 EndX=-160.839 EndY=-150.037 EndZ=0
    g5: LineSegment StartX=-160.839 StartY=-150.037 StartZ=0 EndX=-95 EndY=-174 EndZ=0
    g6: LineSegment StartX=-95 StartY=-174 StartZ=0 EndX=-95 EndY=-193.155 EndZ=0
    g7: LineSegment StartX=-95 StartY=-193.155 StartZ=0 EndX=-179.18 EndY=-162.516 EndZ=0
    g8: LineSegment StartX=-179.18 StartY=-162.516 StartZ=0 EndX=-179.18 EndY=-8.0171 EndZ=0
    g9: LineSegment StartX=-179.18 StartY=-8.0171 StartZ=0 EndX=179.18 EndY=-8.0171 EndZ=0
    g10: LineSegment StartX=179.18 StartY=-8.0171 StartZ=0 EndX=179.18 EndY=-156.131 EndZ=0
    g11: LineSegment StartX=179.18 StartY=-156.131 StartZ=0 EndX=95 EndY=-186.77 EndZ=0
    g12: LineSegment StartX=95 StartY=-186.77 StartZ=0 EndX=95 EndY=-174 EndZ=0
    g13: LineSegment StartX=95 StartY=-174 StartZ=0 EndX=160.839 EndY=-150.037 EndZ=0
    g14: LineSegment StartX=160.839 StartY=-150.037 StartZ=0 EndX=160.839 EndY=-25.9373 EndZ=0
    g15: LineSegment StartX=160.839 StartY=-25.9373 StartZ=0 EndX=72.5228 EndY=-25.9373 EndZ=0
    g16: LineSegment StartX=-72.5228 StartY=-25.9373 StartZ=0 EndX=72.5228 EndY=-25.9373 EndZ=0
  constraints (43):
    c: Coincident(g0,g1)
    c: Coincident(g1,g2)
    c: Vertical(g0)
    c: Vertical(g2)
    c: DistanceY(g0,g-1) = 109
    c: Symmetric(g1,g0,g-2)
    c: Coincident(g2,g3)
    c: Horizontal(g3)
    c: Coincident(g3,g4)
    c: Vertical(g4)
    c: Coincident(g4,g5)
    c: Coincident(g5,g6)
    c: Vertical(g6)
    c: Coincident(g6,g7)
    c: Coincident(g7,g8)
    c: Vertical(g8)
    c: Coincident(g8,g9)
    c: Coincident(g9,g10)
    c: Vertical(g10)
    c: Coincident(g10,g11)
    c: Coincident(g11,g12)
    c: Vertical(g12)
    c: Coincident(g12,g13)
    c: Coincident(g13,g14)
    c: Vertical(g14)
    c: Coincident(g14,g15)
    c: Coincident(g15,g0)
    c: Horizontal(g15)
    c: Symmetric(g8,g9,g-2)
    c: Equal(g3,g15)
    c: Parallel(g5,g7)
    c: Parallel(g13,g11)
    c: Distance(g12,g11) = 12
    c: Angle(g5) = -0.349066
    c: Angle(g13) = 0.349066
    c: Symmetric(g5,g12,g-2)
    c: DistanceX(g5,g12) = 190
    c: DistanceY(g5,g-1) = 174
    c: Block(g9)
    c: Distance(g5,g7) = 18
    c: Coincident(g16,g3)
    c: Coincident(g16,g15)
    c: Horizontal(g16)
FEATURE [PartDesign::Pocket] Pocket029
  BaseFeature = -> Boolean005
  Direction = (0,0,-1)
  Length = 60
  Length2 = 5
  Midplane = true
  Profile = -> Sketch048
  ReferenceAxis = -> Sketch048 [N_Axis]
  Suppressed = false
  Type = 0
FEATURE [Sketcher::SketchObject] Sketch049
  ArcFitTolerance = 0
  FullyConstrained = true
  MakeInternals = false
  MapMode = 5
  Placement = pos=(0,0,0) rot=(1,0,0;1.5708rad)
  sketch-geometry (1):
    g0: Circle CenterX=0 CenterY=0 CenterZ=0 NormalX=0 NormalY=0 NormalZ=1 AngleXU=0 Radius=30
  constraints (2):
    c: Coincident(g0,g-1)
    c: Diameter(g0) = 60
FEATURE [PartDesign::Pocket] Pocket030  label="Pocket023-conrod-polzun001"
  BaseFeature = -> Pocket028
  Direction = (0,1,-2e-16)
  Length = 110
  Length2 = 5
  Profile = -> Sketch049
  ReferenceAxis = -> Sketch049 [N_Axis]
  Suppressed = false
  Type = 0
FEATURE [PartDesign::Pocket] Pocket031  label="Pocket002-ring3"
  BaseFeature = -> Pocket030
  Direction = (0,1,-2e-16)
  Length = 63
  Length2 = -61
  Profile = -> Sketch044
  ReferenceAxis = -> Sketch044 [N_Axis]
  Suppressed = false
  Type = 4
FEATURE [Sketcher::SketchObject] Sketch050
  ArcFitTolerance = 0
  AttachmentSupport = -> [YZ_Plane072]
  FullyConstrained = false
  MakeInternals = false
  MapMode = 5
  Placement = pos=(0,0,0) rot=(0.57735,0.57735,0.57735;2.0944rad)
  sketch-geometry (4):
    g0: LineSegment StartX=-184.527 StartY=91.8627 StartZ=0 EndX=-217.963 EndY=0 EndZ=0
    g1: LineSegment StartX=-217.963 StartY=0 StartZ=0 EndX=-202 EndY=0 EndZ=0
    g2: LineSegment StartX=-202 StartY=0 StartZ=0 EndX=-168.565 EndY=91.8627 EndZ=0
    g3: LineSegment StartX=-168.565 StartY=91.8627 StartZ=0 EndX=-184.527 EndY=91.8627 EndZ=0
  constraints (11):
    c: Coincident(g0,g1)
    c: Horizontal(g1)
    c: Coincident(g1,g2)
    c: Coincident(g2,g3)
    c: Coincident(g3,g0)
    c: Horizontal(g3)
    c: Equal(g1,g3)
    c: Angle(g2) = 1.22173
    c: Distance(g1,g0) = 15
    c: PointOnObject(g1,g-1)
    c: DistanceX(g1,g-1) = 202
FEATURE [PartDesign::Body] Body072  label="Цилиндр"
  AllowCompound = false
  Group = -> [Sketch046,Pad023,Boolean005,Cylynder001,Sketch047,Sketch048,Pocket029,Sketch050]
  Origin = -> Origin073
  Placement = pos=(0,0,25) rot=(0,0,1;0rad)
  Tip = -> Pocket029
FEATURE [PartDesign::CoordinateSystem] Pin
  AttacherType = Attacher::AttachEngine3D
  AttachmentSupport = -> [XY_Plane001]
  MapMode = 5
FEATURE [Sketcher::SketchObject] Sketch052
  ArcFitTolerance = 0
  FullyConstrained = true
  MakeInternals = false
  MapMode = 5
  Placement = pos=(0,0,0) rot=(1,0,0;1.5708rad)
  sketch-geometry (1):
    g0: Circle CenterX=0 CenterY=0 CenterZ=0 NormalX=0 NormalY=0 NormalZ=1 AngleXU=0 Radius=11
  constraints (2):
    c: Coincident(g0,g-1)
    c: Diameter(g0) = 22
FEATURE [PartDesign::Pocket] Pocket032
  BaseFeature = -> Pocket031
  Direction = (0,1,-2e-16)
  Length = 130
  Length2 = 5
  Profile = -> Sketch052
  ReferenceAxis = -> Sketch052 [N_Axis]
  Suppressed = false
  Type = 4
FEATURE [PartDesign::Body] Body071  label="Поршень_2T_92mm"
  AllowCompound = false
  Group = -> [Sketch042,Pad022,Boolean004,Sketch043,Pocket025,Sketch044,Pocket026,Pocket027,Pocket028,Piston001,Sketch049,Pocket030,Pocket031,Sketch052,Pocket032]
  Origin = -> Origin072
  Tip = -> Pocket032
FEATURE [Sketcher::SketchObject] Sketch053
  ArcFitTolerance = 0
  AttachmentOffset = pos=(0,0,-66) rot=(0,0,1;0rad)
  AttachmentSupport = -> [XZ_Plane001]
  FullyConstrained = true
  MakeInternals = false
  MapMode = 5
  Placement = pos=(0,66,-1.47e-14) rot=(1,0,0;1.5708rad)
  sketch-geometry (2):
    g0: Circle CenterX=0 CenterY=0 CenterZ=0 NormalX=0 NormalY=0 NormalZ=1 AngleXU=0 Radius=7.5
    g1: Circle CenterX=0 CenterY=0 CenterZ=0 NormalX=0 NormalY=0 NormalZ=1 AngleXU=0 Radius=5
  constraints (4):
    c: Coincident(g0,g-1)
    c: Coincident(g1,g0)
    c: Diameter(g0) = 15
    c: Diameter(g1) = 10
FEATURE [PartDesign::Pad] Pad
  Direction = (0,-1,2e-16)
  Length = 90
  Length2 = 1
  Placement = pos=(0,0,0) rot=(1,0,0;1.5708rad)
  Profile = -> Sketch053
  ReferenceAxis = -> Sketch053 [N_Axis]
  Reversed = true
  Suppressed = false
  Type = 0
FEATURE [Sketcher::SketchObject] Sketch055
  ArcFitTolerance = 0
  AttachmentOffset = pos=(0,0,-66) rot=(0,0,1;0rad)
  AttachmentSupport = -> [XZ_Plane001]
  FullyConstrained = true
  MakeInternals = false
  MapMode = 5
  Placement = pos=(0,66,-1.47e-14) rot=(1,0,0;1.5708rad)
  sketch-geometry (2):
    g0: Circle CenterX=0 CenterY=0 CenterZ=0 NormalX=0 NormalY=0 NormalZ=1 AngleXU=0 Radius=5
    g1: Circle CenterX=0 CenterY=0 CenterZ=0 NormalX=0 NormalY=0 NormalZ=1 AngleXU=0 Radius=2
  constraints (4):
    c: Diameter(g0) = 10
    c: Coincident(g1,g0)
    c: Coincident(g0,g-1)
    c: Diameter(g1) = 4
FEATURE [PartDesign::Pad] Pad026
  BaseFeature = -> Pad
  Direction = (0,-1,2e-16)
  Length = 5
  Length2 = 17
  Placement = pos=(0,0,0) rot=(1,0,0;1.5708rad)
  Profile = -> Sketch055
  ReferenceAxis = -> Sketch055 [N_Axis]
  Reversed = true
  Suppressed = false
  Type = 4
FEATURE [Sketcher::SketchObject] Sketch058
  ArcFitTolerance = 0
  AttachmentSupport = -> [XY_Plane077]
  FullyConstrained = false
  MakeInternals = false
  MapMode = 5
  sketch-geometry (32):
    g0: LineSegment [constr] StartX=-103 StartY=-65 StartZ=0 EndX=103 EndY=-65 EndZ=0
    g1: LineSegment [constr] StartX=103 StartY=-65 StartZ=0 EndX=103 EndY=65 EndZ=0
    g2: LineSegment [constr] StartX=103 StartY=65 StartZ=0 EndX=-103 EndY=65 EndZ=0
    g3: LineSegment [constr] StartX=-103 StartY=65 StartZ=0 EndX=-103 EndY=-65 EndZ=0
    g4: LineSegment [constr] StartX=-99 StartY=69.5 StartZ=0 EndX=99 EndY=69.5 EndZ=0
    g5: LineSegment [constr] StartX=-103 StartY=65 StartZ=0 EndX=-103 EndY=65.5 EndZ=0
    g6: LineSegment [constr] StartX=103 StartY=65.5 StartZ=0 EndX=103 EndY=65 EndZ=0
    g7: ArcOfCircle [constr] CenterX=-99 CenterY=65.5 CenterZ=0 NormalX=0 NormalY=0 NormalZ=1 AngleXU=0 Radius=4 StartAngle=1.5708 EndAngle=3.14159
    g8: ArcOfCircle [constr] CenterX=99 CenterY=65.5 CenterZ=0 NormalX=0 NormalY=0 NormalZ=1 AngleXU=0 Radius=4 StartAngle=-9e-16 EndAngle=1.5708
    g9: ArcOfCircle [constr] CenterX=-99 CenterY=-65.5 CenterZ=0 NormalX=0 NormalY=0 NormalZ=1 AngleXU=0 Radius=4 StartAngle=3.14159 EndAngle=4.71239
    g10: LineSegment [constr] StartX=-103 StartY=-65 StartZ=0 EndX=-103 EndY=-65.5 EndZ=0
    g11: LineSegment [constr] StartX=-99 StartY=-69.5 StartZ=0 EndX=99 EndY=-69.5 EndZ=0
    g12: ArcOfCircle [constr] CenterX=99 CenterY=-65.5 CenterZ=0 NormalX=0 NormalY=0 NormalZ=1 AngleXU=0 Radius=4 StartAngle=4.71239 EndAngle=6.28319
    g13: LineSegment [constr] StartX=103 StartY=-65.5 StartZ=0 EndX=103 EndY=-65 EndZ=0
    g14: Circle CenterX=-95 CenterY=55 CenterZ=0 NormalX=0 NormalY=0 NormalZ=1 AngleXU=0 Radius=3
    g15: Circle [constr] CenterX=95 CenterY=55 CenterZ=0 NormalX=0 NormalY=0 NormalZ=1 AngleXU=0 Radius=3
    g16: Circle [constr] CenterX=-95 CenterY=-55 CenterZ=0 NormalX=0 NormalY=0 NormalZ=1 AngleXU=0 Radius=3
    g17: Circle [constr] CenterX=95 CenterY=-55 CenterZ=0 NormalX=0 NormalY=0 NormalZ=1 AngleXU=0 Radius=3
    g18: Circle [constr] CenterX=0 CenterY=0 CenterZ=0 NormalX=0 NormalY=0 NormalZ=1 AngleXU=0 Radius=32.25
    g19: LineSegment [constr] StartX=-103 StartY=-65 StartZ=0 EndX=-91.9993 EndY=-65 EndZ=0
    g20: LineSegment [constr] StartX=-91.9993 StartY=-65 StartZ=0 EndX=-91.9993 EndY=-49.9993 EndZ=0
    g21: LineSegment [constr] StartX=-91.9993 StartY=-49.9993 StartZ=0 EndX=-103 EndY=-49.9993 EndZ=0
    g22: LineSegment [constr] StartX=-103 StartY=-49.9993 StartZ=0 EndX=-103 EndY=-65 EndZ=0
    g23: LineSegment [constr] StartX=103 StartY=-65 StartZ=0 EndX=91.9993 EndY=-65 EndZ=0
    g24: LineSegment [constr] StartX=91.9993 StartY=-65 StartZ=0 EndX=91.9993 EndY=-49.9993 EndZ=0
    g25: LineSegment [constr] StartX=91.9993 StartY=-49.9993 StartZ=0 EndX=103 EndY=-49.9993 EndZ=0
    g26: LineSegment [constr] StartX=103 StartY=-49.9993 StartZ=0 EndX=103 EndY=-65 EndZ=0
    g27: LineSegment [constr] StartX=103 StartY=65 StartZ=0 EndX=91.9993 EndY=65 EndZ=0
    g28: LineSegment [constr] StartX=91.9993 StartY=65 StartZ=0 EndX=91.9993 EndY=49.9993 EndZ=0
    g29: LineSegment [constr] StartX=91.9993 StartY=49.9993 StartZ=0 EndX=103 EndY=49.9993 EndZ=0
    g30: LineSegment [constr] StartX=103 StartY=49.9993 StartZ=0 EndX=103 EndY=65 EndZ=0
    g31: Circle CenterX=-95 CenterY=55 CenterZ=0 NormalX=0 NormalY=0 NormalZ=1 AngleXU=0 Radius=8
  constraints (75):
    c: Coincident(g0,g1)
    c: Coincident(g1,g2)
    c: Coincident(g2,g3)
    c: Coincident(g3,g0)
    c: Horizontal(g0)
    c: Vertical(g1)
    c: Symmetric(g2,g1,g-2)
    c: Symmetric(g2,g0,g-1)
    c: DistanceX(g2,g2) = 206
    c: DistanceY(g1,g1) = 130
    c: Coincident(g5,g3)
    c: Coincident(g6,g1)
    c: Tangent(g5,g7) = 1.5708
    c: Tangent(g4,g7) = 1.5708
    c: Tangent(g4,g8) = 1.5708
    c: Tangent(g6,g8) = 1.5708
    c: Vertical(g5)
    c: Vertical(g6)
    c: Symmetric(g7,g8,g-2)
    c: DistanceY(g1,g4) = 4.5
    c: Radius(g8) = 4
    c: Tangent(g10,g9) = -1.5708
    c: Tangent(g11,g9) = -1.5708
    c: Tangent(g11,g12) = -1.5708
    c: Vertical(g10)
    c: Symmetric(g9,g12,g-2)
    c: Symmetric(g9,g7,g-1)
    c: Coincident(g10,g3)
    c: Coincident(g13,g1)
    c: Vertical(g13)
    c: Equal(g13,g10)
    c: Coincident(g12,g13)
    c: Equal(g14,g15)
    c: Equal(g15,g17)
    c: Equal(g17,g16)
    c: Diameter(g15) = 6
    c: Symmetric(g14,g15,g-2)
    c: Symmetric(g16,g17,g-2)
    c: Symmetric(g16,g14,g-1)
    c: DistanceY(g16,g14) = 110
    c: DistanceX(g16,g17) = 190
    c: Coincident(g18,g-1)
    c: Diameter(g18) = 64.5
    c: Coincident(g19,g20)
    c: Coincident(g20,g21)
    c: Coincident(g21,g22)
    c: Coincident(g22,g19)
    c: Horizontal(g19)
    c: Horizontal(g21)
    c: Vertical(g20)
    c: Vertical(g22)
    c: Coincident(g19,g0)
    c: Coincident(g23,g24)
    c: Coincident(g24,g25)
    c: Coincident(g25,g26)
    c: Coincident(g26,g23)
    c: Horizontal(g23)
    c: Horizontal(g25)
    c: Vertical(g24)
    c: Vertical(g26)
    c: Coincident(g23,g0)
    c: Coincident(g27,g28)
    c: Coincident(g28,g29)
    c: Coincident(g29,g30)
    c: Coincident(g30,g27)
    c: Horizontal(g27)
    c: Horizontal(g29)
    c: Vertical(g28)
    c: Vertical(g30)
    c: Coincident(g27,g1)
    c: Equal(g25,g29)
    c: Equal(g28,g24)
    c: Equal(g24,g20)
    c: Coincident(g31,g14)
    c: Tangent(g31,g3)
FEATURE [PartDesign::Pad] Pad029
  Direction = (0,0,1)
  Length = 25
  Length2 = 28.5
  Midplane = true
  Profile = -> Sketch058
  ReferenceAxis = -> Sketch058 [N_Axis]
  Suppressed = false
  Type = 4
FEATURE [PartDesign::CoordinateSystem] Shtok005
  AttacherType = Attacher::AttachEngine3D
  AttachmentSupport = -> [Sketch058]
  MapMode = 2
FEATURE [PartDesign::Body] Body077  label="проставка_корпуса"
  AllowCompound = false
  Group = -> [Sketch058,Pad029,Shtok005]
  Origin = -> Origin078
  Tip = -> Pad029
FEATURE [Sketcher::SketchObject] Sketch060
  ArcFitTolerance = 0
  FullyConstrained = true
  MakeInternals = false
  Placement = pos=(0,0,0) rot=(1,0,0;3.14159rad)
  expr: Constraints[11] = <<Dim_table>>.crank_dia1 + <<Dim_table>>.zazor
  expr: Constraints[14] = <<Dim_table>>.crank_dia2
  expr: Constraints[15] = <<Dim_table>>.inter_shaft_len / 2
  expr: Constraints[6] = <<Dim_table>>.inter_shaft_len
  expr: Constraints[7] = <<Dim_table>>.crank_dia1 * 1.5
  sketch-geometry (7):
    g0: ArcOfCircle CenterX=0 CenterY=0 CenterZ=0 NormalX=0 NormalY=0 NormalZ=1 AngleXU=0 Radius=18.75 StartAngle=1.5708 EndAngle=4.71239
    g1: ArcOfCircle CenterX=100 CenterY=-1.6e-15 CenterZ=0 NormalX=0 NormalY=0 NormalZ=1 AngleXU=0 Radius=18.75 StartAngle=4.71239 EndAngle=7.85398
    g2: LineSegment StartX=-3.4e-15 StartY=-18.75 StartZ=0 EndX=100 EndY=-18.75 EndZ=0
    g3: LineSegment StartX=100 StartY=18.75 StartZ=0 EndX=1.42e-14 EndY=18.75 EndZ=0
    g4: Circle CenterX=0 CenterY=0 CenterZ=0 NormalX=0 NormalY=0 NormalZ=1 AngleXU=0 Radius=12.75
    g5: Circle CenterX=100 CenterY=-1.6e-15 CenterZ=0 NormalX=0 NormalY=0 NormalZ=1 AngleXU=0 Radius=12.75
    g6: Circle CenterX=50 CenterY=0 CenterZ=0 NormalX=0 NormalY=0 NormalZ=1 AngleXU=0 Radius=12.5
  constraints (16):
    c: Tangent(g0,g2) = -1.5708
    c: Tangent(g2,g1) = -1.5708
    c: Tangent(g1,g3) = -1.5708
    c: Tangent(g3,g0) = -1.5708
    c: Equal(g0,g1)
    c: Horizontal(g2)
    c: DistanceX(g0,g1) = 100
    c: Diameter(g0) = 37.5
    c: Coincident(g4,g0)
    c: Coincident(g5,g1)
    c: Equal(g4,g5)
    c: Diameter(g4) = 25.5
    c: Coincident(g0,g-1)
    c: PointOnObject(g6,g-1)
    c: Diameter(g6) = 25
    c: DistanceX(g0,g6) = 50
FEATURE [Sketcher::SketchObject] Sketch061
  ArcFitTolerance = 0
  AttachmentSupport = -> [Pad020]
  FullyConstrained = false
  MakeInternals = false
  MapMode = 5
  Placement = pos=(0,0,22.5) rot=(0,0,1;0rad)
  sketch-geometry (5):
    g0: Circle CenterX=0 CenterY=0 CenterZ=0 NormalX=0 NormalY=0 NormalZ=1 AngleXU=0 Radius=8.25
    g1: LineSegment StartX=-79.3827 StartY=20 StartZ=0 EndX=79.3827 EndY=20 EndZ=0
    g2: LineSegment StartX=79.3827 StartY=20 StartZ=0 EndX=79.3827 EndY=-20 EndZ=0
    g3: LineSegment StartX=79.3827 StartY=-20 StartZ=0 EndX=-79.3827 EndY=-20 EndZ=0
    g4: LineSegment StartX=-79.3827 StartY=-20 StartZ=0 EndX=-79.3827 EndY=20 EndZ=0
  constraints (12):
    c: Coincident(g0,g-1)
    c: Diameter(g0) = 16.5
    c: Coincident(g1,g2)
    c: Coincident(g2,g3)
    c: Coincident(g3,g4)
    c: Coincident(g4,g1)
    c: Horizontal(g1)
    c: Horizontal(g3)
    c: Vertical(g2)
    c: Vertical(g4)
    c: Symmetric(g3,g1,g0)
    c: DistanceY(g2,g2) = 40
FEATURE [PartDesign::Pad] Pad032
  BaseFeature = -> Pad020
  Direction = (0,0,1)
  Length = 16
  Length2 = 10
  Profile = -> Sketch061
  ReferenceAxis = -> Sketch061 [N_Axis]
  Reversed = true
  Suppressed = false
  Type = 0
FEATURE [PartDesign::Body] Body066  label="направляющая_орто_ползуна"
  AllowCompound = false
  Group = -> [Sketch038,Pad020,Shtok003,Sketch061,Pad032]
  Origin = -> Origin067
  Tip = -> Pad032
FEATURE [Spreadsheet::Sheet] Spreadsheet  label="Dim_table"
  cells = A1(crank_dia1)=25; B1='crank_dia1; A2(crank_dia2)=25; B2='crank_dia2; A3(crank_dia3)=16; B3='crank_dia3; A4(crank_len)==85 / 4; B4='crank_len; A5(crank_gear_ecc)=10; B5='crank_gear_ecc; A6(ecc_dia)=80; B6='ecc_dia; A7(ecc_hei)=16.5; B7='ecc_hei; A8(inter_shaft_len)=100; B8='inter_shaft_len; A9(piston_dia)=72; B9='piston_dia; A10(piston_hei)=39; B10='piston_hei; A11(piston_pin_dia)=12; B11='piston_pin_dia; A12(rod_len)=140; B12='rod_len; A13(zazor)=0.5; B13='zazor; A14(delta)=0.05; B14='delta; A15(hex_size)=14; B15='hex_size; A16(fillet_r)=2; B16='fillet_r; A17(axle_hole_dia)=5; B17='axle_hole_dia; A18(roller_dia)=3; B18='roller_dia
FEATURE [Sketcher::SketchObject] Sketch064
  ArcFitTolerance = 0
  FullyConstrained = true
  MakeInternals = false
  Placement = pos=(0,0,0) rot=(1,0,0;3.14159rad)
  expr: Constraints[1] = <<Dim_table>>.inter_shaft_len * 1.2
  sketch-geometry (1):
    g0: Circle CenterX=0 CenterY=0 CenterZ=0 NormalX=0 NormalY=0 NormalZ=1 AngleXU=0 Radius=60
  constraints (2):
    c: Coincident(g0,g-1)
    c: Diameter(g0) = 120
FEATURE [Sketcher::SketchObject] Sketch066
  ArcFitTolerance = 0
  FullyConstrained = false
  MakeInternals = false
  MapMode = 5
  sketch-geometry (40):
    g0: Circle CenterX=-65 CenterY=167.5 CenterZ=0 NormalX=0 NormalY=0 NormalZ=1 AngleXU=0 Radius=3
    g1: Circle CenterX=-76 CenterY=150 CenterZ=0 NormalX=0 NormalY=0 NormalZ=1 AngleXU=0 Radius=3
    g2: ArcOfCircle CenterX=-80 CenterY=159.195 CenterZ=0 NormalX=0 NormalY=0 NormalZ=1 AngleXU=0 Radius=4 StartAngle=2.43396 EndAngle=3.14159
    g3: ArcOfCircle CenterX=-65 CenterY=167.5 CenterZ=0 NormalX=0 NormalY=0 NormalZ=1 AngleXU=0 Radius=10 StartAngle=1.5708 EndAngle=2.43396
    g4: LineSegment StartX=-65 StartY=177.5 StartZ=0 EndX=65 EndY=177.5 EndZ=0
    g5: LineSegment StartX=-57.25 StartY=172.5 StartZ=0 EndX=57.25 EndY=172.5 EndZ=0
    g6: Circle CenterX=-76 CenterY=0 CenterZ=0 NormalX=0 NormalY=0 NormalZ=1 AngleXU=0 Radius=3
    g7: LineSegment StartX=-84 StartY=141.772 StartZ=0 EndX=-57.25 EndY=141.772 EndZ=0
    g8: LineSegment StartX=-57.25 StartY=141.772 StartZ=0 EndX=-57.25 EndY=172.5 EndZ=0
    g9: Circle CenterX=-76 CenterY=0 CenterZ=0 NormalX=0 NormalY=0 NormalZ=1 AngleXU=0 Radius=7.35704
    g10: LineSegment StartX=-72.599 StartY=174 StartZ=0 EndX=-83.0396 EndY=161.795 EndZ=0
    g11: LineSegment StartX=-84 StartY=141.772 StartZ=0 EndX=-84 EndY=159.195 EndZ=0
    g12: Circle CenterX=65 CenterY=167.5 CenterZ=0 NormalX=0 NormalY=0 NormalZ=1 AngleXU=0 Radius=3
    g13: Circle CenterX=76 CenterY=150 CenterZ=0 NormalX=0 NormalY=0 NormalZ=1 AngleXU=0 Radius=3
    g14: ArcOfCircle CenterX=80 CenterY=159.195 CenterZ=0 NormalX=0 NormalY=0 NormalZ=1 AngleXU=0 Radius=4 StartAngle=-1.634e-13 EndAngle=0.707637
    g15: ArcOfCircle CenterX=65 CenterY=167.5 CenterZ=0 NormalX=0 NormalY=0 NormalZ=1 AngleXU=0 Radius=10 StartAngle=0.707637 EndAngle=1.5708
    g16: LineSegment StartX=84 StartY=141.772 StartZ=0 EndX=57.25 EndY=141.772 EndZ=0
    g17: LineSegment StartX=57.25 StartY=141.772 StartZ=0 EndX=57.25 EndY=172.5 EndZ=0
    g18: LineSegment StartX=72.599 StartY=174 StartZ=0 EndX=83.0396 EndY=161.795 EndZ=0
    g19: LineSegment StartX=84 StartY=141.772 StartZ=0 EndX=84 EndY=159.195 EndZ=0
    g20: Circle CenterX=76 CenterY=0 CenterZ=0 NormalX=0 NormalY=0 NormalZ=1 AngleXU=0 Radius=3
    g21: Circle CenterX=76 CenterY=0 CenterZ=0 NormalX=0 NormalY=0 NormalZ=1 AngleXU=0 Radius=7.35704
    g22: Circle CenterX=-65 CenterY=-167.5 CenterZ=0 NormalX=0 NormalY=0 NormalZ=1 AngleXU=0 Radius=3
    g23: Circle CenterX=-76 CenterY=-150 CenterZ=0 NormalX=0 NormalY=0 NormalZ=1 AngleXU=0 Radius=3
    g24: ArcOfCircle CenterX=-80 CenterY=-159.195 CenterZ=0 NormalX=0 NormalY=0 NormalZ=1 AngleXU=0 Radius=4 StartAngle=3.14159 EndAngle=3.84923
    g25: ArcOfCircle CenterX=-65 CenterY=-167.5 CenterZ=0 NormalX=0 NormalY=0 NormalZ=1 AngleXU=0 Radius=10 StartAngle=3.84923 EndAngle=4.71239
    g26: LineSegment StartX=-65 StartY=-177.5 StartZ=0 EndX=65 EndY=-177.5 EndZ=0
    g27: LineSegment StartX=-57.25 StartY=-172.5 StartZ=0 EndX=57.25 EndY=-172.5 EndZ=0
    g28: LineSegment StartX=-84 StartY=-141.772 StartZ=0 EndX=-57.25 EndY=-141.772 EndZ=0
    g29: LineSegment StartX=-57.25 StartY=-141.772 StartZ=0 EndX=-57.25 EndY=-172.5 EndZ=0
    g30: LineSegment StartX=-72.599 StartY=-174 StartZ=0 EndX=-83.0396 EndY=-161.795 EndZ=0
    g31: LineSegment StartX=-84 StartY=-141.772 StartZ=0 EndX=-84 EndY=-159.195 EndZ=0
    g32: Circle CenterX=65 CenterY=-167.5 CenterZ=0 NormalX=0 NormalY=0 NormalZ=1 AngleXU=0 Radius=3
    g33: Circle CenterX=76 CenterY=-150 CenterZ=0 NormalX=0 NormalY=0 NormalZ=1 AngleXU=0 Radius=3
    g34: ArcOfCircle CenterX=80 CenterY=-159.195 CenterZ=0 NormalX=0 NormalY=0 NormalZ=1 AngleXU=0 Radius=4 StartAngle=5.57555 EndAngle=6.28319
    g35: ArcOfCircle CenterX=65 CenterY=-167.5 CenterZ=0 NormalX=0 NormalY=0 NormalZ=1 AngleXU=0 Radius=10 StartAngle=4.71239 EndAngle=5.57555
    g36: LineSegment StartX=84 StartY=-141.772 StartZ=0 EndX=57.25 EndY=-141.772 EndZ=0
    g37: LineSegment StartX=57.25 StartY=-141.772 StartZ=0 EndX=57.25 EndY=-172.5 EndZ=0
    g38: LineSegment StartX=72.599 StartY=-174 StartZ=0 EndX=83.0396 EndY=-161.795 EndZ=0
    g39: LineSegment StartX=84 StartY=-141.772 StartZ=0 EndX=84 EndY=-159.195 EndZ=0
  constraints (44):
    c: Coincident(g0,g-6)
    c: Coincident(g1,g-7)
    c: Equal(g-7,g1)
    c: Equal(g-6,g0)
    c: Coincident(g2,g-10)
    c: Coincident(g2,g-11)
    c: Coincident(g3,g-5)
    c: Coincident(g4,g3)
    c: Coincident(g5,g-9)
    c: Coincident(g6,g-12)
    c: Equal(g-12,g6)
    c: Horizontal(g7)
    c: Coincident(g8,g7)
    c: Coincident(g8,g5)
    c: Coincident(g9,g6)
    c: Coincident(g5,g-9)
    c: Coincident(g4,g-3)
    c: Tangent(g3,g-4) = -1.5708
    c: Coincident(g10,g3)
    c: Tangent(g2,g10) = -1.5708
    c: Coincident(g11,g7)
    c: Tangent(g11,g2) = 1.5708
    c: PointOnObject(g7,g-8)
    c: Horizontal(g16)
    c: Coincident(g17,g16)
    c: Coincident(g18,g15)
    c: Tangent(g14,g18) = 1.5708
    c: Coincident(g19,g16)
    c: Tangent(g19,g14) = -1.5708
    c: Coincident(g21,g20)
    c: Coincident(g26,g25)
    c: Horizontal(g28)
    c: Coincident(g29,g28)
    c: Coincident(g29,g27)
    c: Coincident(g30,g25)
    c: Tangent(g24,g30) = 1.5708
    c: Coincident(g31,g28)
    c: Tangent(g31,g24) = -1.5708
    c: Horizontal(g36)
    c: Coincident(g37,g36)
    c: Coincident(g38,g35)
    c: Tangent(g34,g38) = -1.5708
    c: Coincident(g39,g36)
    c: Tangent(g39,g34) = 1.5708
FEATURE [Part::Extrusion] Extrude  label="проставка ползуна_001"
  Base = -> Sketch066
  Dir = (0,0,1)
  DirMode = 2
  FaceMakerClass = Part::FaceMakerBullseye
  FaceMakerMode = 3
  LengthFwd = 26.75
  LengthRev = 0
  Reversed = true
  Solid = true
  Symmetric = false
FEATURE [Sketcher::SketchObject] Sketch067
  ArcFitTolerance = 0
  AttachmentSupport = -> [XY_Plane085]
  FullyConstrained = true
  MakeInternals = false
  MapMode = 5
  expr: Constraints[14] = <<Dim_table>>.inter_shaft_len * 2.15
  expr: Constraints[15] = <<Dim_table>>.ecc_dia * 1.2
  expr: Constraints[16] = <<Dim_table>>.inter_shaft_len * 1.85
  expr: Constraints[22] = <<Dim_table>>.inter_shaft_len / 2
  expr: Constraints[37] = <<Dim_table>>.inter_shaft_len * 2.35
  expr: Constraints[38] = <<Dim_table>>.crank_dia2
  expr: Constraints[39] = <<Dim_table>>.inter_shaft_len * 2
  expr: Constraints[45] = <<Dim_table>>.inter_shaft_len / 2
  expr: Constraints[53] = <<Dim_table>>.axle_hole_dia
  expr: Constraints[56] = <<Dim_table>>.inter_shaft_len
  expr: Constraints[58] = <<Dim_table>>.crank_dia2 + <<Dim_table>>.zazor
  sketch-geometry (27):
    g0: LineSegment [constr] StartX=-9.5 StartY=-92.5 StartZ=0 EndX=109.5 EndY=-92.5 EndZ=0
    g1: LineSegment [constr] StartX=157.5 StartY=-44.5 StartZ=0 EndX=157.5 EndY=44.5 EndZ=0
    g2: LineSegment [constr] StartX=109.5 StartY=92.5 StartZ=0 EndX=-9.5 EndY=92.5 EndZ=0
    g3: LineSegment [constr] StartX=-57.5 StartY=44.5 StartZ=0 EndX=-57.5 EndY=-44.5 EndZ=0
    g4: ArcOfCircle [constr] CenterX=-9.5 CenterY=44.5 CenterZ=0 NormalX=0 NormalY=0 NormalZ=1 AngleXU=0 Radius=48 StartAngle=1.5708 EndAngle=3.14159
    g5: ArcOfCircle [constr] CenterX=109.5 CenterY=44.5 CenterZ=0 NormalX=0 NormalY=0 NormalZ=1 AngleXU=0 Radius=48 StartAngle=0 EndAngle=1.5708
    g6: ArcOfCircle [constr] CenterX=-9.5 CenterY=-44.5 CenterZ=0 NormalX=0 NormalY=0 NormalZ=1 AngleXU=0 Radius=48 StartAngle=3.14159 EndAngle=4.71239
    g7: ArcOfCircle [constr] CenterX=109.5 CenterY=-44.5 CenterZ=0 NormalX=0 NormalY=0 NormalZ=1 AngleXU=0 Radius=48 StartAngle=4.71239 EndAngle=6.28319
    g8: LineSegment [constr] StartX=-57.5 StartY=-44.5 StartZ=0 EndX=157.5 EndY=44.5 EndZ=0
    g9: GeomPoint [constr] X=50 Y=0 Z=0
    g10: ArcOfCircle CenterX=-55 CenterY=87.5 CenterZ=0 NormalX=0 NormalY=0 NormalZ=1 AngleXU=0 Radius=12.5 StartAngle=1.5708 EndAngle=3.14159
    g11: LineSegment StartX=155 StartY=100 StartZ=0 EndX=-55 EndY=100 EndZ=0
    g12: ArcOfCircle CenterX=155 CenterY=87.5 CenterZ=0 NormalX=0 NormalY=0 NormalZ=1 AngleXU=0 Radius=12.5 StartAngle=7.02e-14 EndAngle=1.5708
    g13: LineSegment StartX=167.5 StartY=-87.5 StartZ=0 EndX=167.5 EndY=87.5 EndZ=0
    g14: ArcOfCircle CenterX=155 CenterY=-87.5 CenterZ=0 NormalX=0 NormalY=0 NormalZ=1 AngleXU=0 Radius=12.5 StartAngle=4.71239 EndAngle=6.28319
    g15: LineSegment StartX=-55 StartY=-100 StartZ=0 EndX=155 EndY=-100 EndZ=0
    g16: ArcOfCircle CenterX=-55 CenterY=-87.5 CenterZ=0 NormalX=0 NormalY=0 NormalZ=1 AngleXU=0 Radius=12.5 StartAngle=3.14159 EndAngle=4.71239
    g17: LineSegment StartX=-67.5 StartY=87.5 StartZ=0 EndX=-67.5 EndY=-87.5 EndZ=0
    g18: LineSegment [constr] StartX=-55 StartY=100 StartZ=0 EndX=155 EndY=-100 EndZ=0
    g19: GeomPoint [constr] X=50 Y=0 Z=0
    g20: Circle CenterX=-55 CenterY=87.5 CenterZ=0 NormalX=0 NormalY=0 NormalZ=1 AngleXU=0 Radius=2.5
    g21: Circle CenterX=155 CenterY=87.5 CenterZ=0 NormalX=0 NormalY=0 NormalZ=1 AngleXU=0 Radius=2.5
    g22: Circle CenterX=-55 CenterY=-87.5 CenterZ=0 NormalX=0 NormalY=0 NormalZ=1 AngleXU=0 Radius=2.5
    g23: Circle CenterX=155 CenterY=-87.5 CenterZ=0 NormalX=0 NormalY=0 NormalZ=1 AngleXU=0 Radius=2.5
    g24: Circle CenterX=0 CenterY=0 CenterZ=0 NormalX=0 NormalY=0 NormalZ=1 AngleXU=0 Radius=12.75
    g25: Circle CenterX=100 CenterY=0 CenterZ=0 NormalX=0 NormalY=0 NormalZ=1 AngleXU=0 Radius=12.75
    g26: Circle CenterX=50 CenterY=0 CenterZ=0 NormalX=0 NormalY=0 NormalZ=1 AngleXU=0 Radius=12.75
  constraints (61):
    c: Horizontal(g0)
    c: Horizontal(g2)
    c: Vertical(g1)
    c: Vertical(g3)
    c: Tangent(g2,g4) = -1.5708
    c: Tangent(g3,g4) = -1.5708
    c: Tangent(g2,g5) = -1.5708
    c: Tangent(g1,g5) = -1.5708
    c: Tangent(g3,g6) = -1.5708
    c: Tangent(g0,g6) = -1.5708
    c: Tangent(g0,g7) = -1.5708
    c: Tangent(g1,g7) = -1.5708
    c: Equal(g4,g5)
    c: Equal(g5,g7)
    c: DistanceX(g3,g1) = 215
    c: Diameter(g4) = 96
    c: DistanceY(g0,g2) = 185
    c: Symmetric(g2,g0,g-1)
    c: Coincident(g8,g3)
    c: Coincident(g8,g1)
    c: PointOnObject(g9,g-1)
    c: PointOnObject(g9,g8)
    c: DistanceX(g-1,g9) = 50
    c: Horizontal(g15)
    c: Horizontal(g11)
    c: Vertical(g13)
    c: Vertical(g17)
    c: Tangent(g11,g10) = -1.5708
    c: Tangent(g17,g10) = -1.5708
    c: Tangent(g11,g12) = -1.5708
    c: Tangent(g13,g12) = -1.5708
    c: Tangent(g17,g16) = -1.5708
    c: Tangent(g15,g16) = -1.5708
    c: Tangent(g15,g14) = -1.5708
    c: Tangent(g13,g14) = -1.5708
    c: Equal(g10,g12)
    c: Equal(g12,g14)
    c: DistanceX(g17,g13) = 235
    c: Diameter(g10) = 25
    c: DistanceY(g15,g11) = 200
    c: Symmetric(g10,g16,g-1)
    c: Coincident(g18,g10)
    c: Coincident(g18,g14)
    c: PointOnObject(g19,g-1)
    c: PointOnObject(g19,g18)
    c: DistanceX(g-1,g19) = 50
    c: Coincident(g20,g10)
    c: Coincident(g21,g12)
    c: Coincident(g22,g16)
    c: Coincident(g23,g14)
    c: Equal(g22,g23)
    c: Equal(g23,g21)
    c: Equal(g21,g20)
    c: Diameter(g20) = 5
    c: Coincident(g24,g-1)
    c: PointOnObject(g25,g-1)
    c: DistanceX(g24,g25) = 100
    c: Equal(g25,g24)
    c: Diameter(g24) = 25.5
    c: Coincident(g26,g9)
    c: Equal(g24,g26)
FEATURE [PartDesign::CoordinateSystem] LCS_Origin006
  AttacherType = Attacher::AttachEngine3D
  AttachmentSupport = -> [X_Axis083]
  MapMode = 2
FEATURE [PartDesign::Pad] Pad036
  Direction = (0,0,1)
  Length = 4
  Length2 = 10
  Profile = -> Sketch067
  ReferenceAxis = -> Sketch067 [N_Axis]
  Suppressed = false
  Type = 0
FEATURE [Part::FeaturePython] InvoluteGear006  label="crank_gear_01-1"  # WARN: FeaturePython — macro-defined, semantics opaque (R4)
  AttacherType = Attacher::AttachEngine3D
  addendum_diameter = 47.5
  angular_backlash = 0
  axle_hole = true
  axle_holesize = 25.5
  backlash = 0
  clearance = 0.25
  double_helix = false
  head = 0
  head_fillet = 0
  height = 10
  helix_angle = 0
  module = 2.5
  num_teeth = 17
  numpoints = 20
  offset_hole = true
  offset_holeoffset = 20
  offset_holesize = 1
  pitch_diameter = 42.5
  pressure_angle = 20
  properties_from_tool = false
  reversed_backlash = false
  root_diameter = 36.25
  root_fillet = 0
  shift = 0
  simple = false
  transverse_pitch = 7.85398
  traverse_module = 2.5
  undercut = false
  version = 1.3.0
  expr: angular_backlash = backlash / pitch_diameter * 360 ° / pi
  expr: axle_holesize = <<Dim_table>>.crank_dia2 + <<Dim_table>>.zazor
FEATURE [Part::FeaturePython] InternalInvoluteGear001  label="crank_int_gear_01-1"  # WARN: FeaturePython — macro-defined, semantics opaque (R4)
  AttacherType = Attacher::AttachEngine3D
  addendum_diameter = 82
  angular_backlash = 0
  backlash = 0
  clearance = 0.25
  double_helix = false
  head = -0.4
  head_fillet = 0
  height = 10
  helix_angle = 0
  module = 2.5
  num_teeth = 34
  numpoints = 20
  outside_diameter = 100
  pitch_diameter = 85
  pressure_angle = 20
  properties_from_tool = false
  reversed_backlash = false
  root_diameter = 91.25
  root_fillet = 0
  shift = 0
  simple = false
  thickness = 7.5
  transverse_pitch = 7.85398
  version = 1.3.0
  expr: angular_backlash = backlash / pitch_diameter * 360 ° / pi
FEATURE [PartDesign::FeatureBase] BaseFeature
  BaseFeature = -> InvoluteGear006
  Suppressed = false
FEATURE [PartDesign::FeatureBase] BaseFeature001
  BaseFeature = -> InternalInvoluteGear001
  Suppressed = false
FEATURE [PartDesign::CoordinateSystem] Local_CS004
  AttacherType = Attacher::AttachEngine3D
  AttachmentSupport = -> [BaseFeature001]
  MapMode = 2
FEATURE [PartDesign::Body] Body088  label="crank_int_gear_01"
  AllowCompound = false
  BaseFeature = -> InternalInvoluteGear001
  Group = -> [BaseFeature001,Local_CS004]
  Origin = -> Origin091
  Tip = -> BaseFeature001
FEATURE [PartDesign::CoordinateSystem] Local_CS005
  AttacherType = Attacher::AttachEngine3D
  AttachmentOffset = pos=(0,0,0) rot=(0,0,1;0.279253rad)
  AttachmentSupport = -> [BaseFeature]
  MapMode = 2
  Placement = pos=(0,0,0) rot=(0,0,1;0.279253rad)
FEATURE [PartDesign::CoordinateSystem] LCS_6  label="crank"
  AttacherType = Attacher::AttachEngine3D
  AttachmentOffset = pos=(0,0,-21.25) rot=(0,0,1;0rad)
  AttachmentSupport = -> [Main]
  MapMode = 7
  Placement = pos=(7.4e-15,2.49e-14,4.7e-15) rot=(0,0.707107,0.707107;3.14159rad)
  expr: .AttachmentOffset.Base.z = -<<Dim_table>>.crank_len
FEATURE [PartDesign::CoordinateSystem] crank2_axle  label="ecc"
  AttacherType = Attacher::AttachEngine3D
  AttachmentSupport = -> [Main]
  MapMode = 7
  Placement = pos=(-2.74918e-11,21.25,0) rot=(1,0,0;1.5708rad)
  expr: .Placement.Base.x = <<Dim_table>>.inter_shaft_len
FEATURE [PartDesign::CoordinateSystem] Shtok_rama  label="shtok1"
  AttacherType = Attacher::AttachEngine3D
  AttachmentOffset = pos=(0,0,-140) rot=(0,0,1;0rad)
  AttachmentSupport = -> [Main]
  MapMode = 7
  Placement = pos=(6.3065e-12,42.5,3.11e-14) rot=(0,0.707107,0.707107;3.14159rad)
  expr: .AttachmentOffset.Base.z = -<<Dim_table>>.rod_len
FEATURE [App::Link] _____________________________  label="Колевал (секция)001"
  AttachedBy = #Crank_shaft
  AttachedTo = Parent Assembly#LCS_Origin
  AttachmentOffset = pos=(0,0,-36.25) rot=(0,0,1;-7.85398rad)
  LinkPlacement = pos=(0,0,-7.75) rot=(0,0,1;3.14159rad)
  LinkedObject = -> Body057
  Placement = pos=(0,0,-7.75) rot=(0,0,1;3.14159rad)
  SolverId = Asm4EE
  expr: .AttachmentOffset.Rotation.Angle = -<<Variables>>.Crank_Angle - 90
  expr: Placement = LCS_Origin.Placement * AttachmentOffset * Crank_shaft.Placement ^ -1
FEATURE [Sketcher::SketchObject] Sketch070
  ArcFitTolerance = 0
  AttachmentSupport = -> [Pad003]
  FullyConstrained = true
  MakeInternals = false
  MapMode = 11
  Placement = pos=(0,-21.25,79.5) rot=(0,0,1;1.5708rad)
  expr: Constraints[12] = <<Dim_table>>.crank_dia2
  expr: Constraints[13] = <<Dim_table>>.axle_hole_dia
  expr: Constraints[14] = 0
  expr: Constraints[3] = <<Dim_table>>.crank_dia2 * 0.8
  sketch-geometry (5):
    g0: ArcOfCircle CenterX=0 CenterY=0 CenterZ=0 NormalX=0 NormalY=0 NormalZ=1 AngleXU=0 Radius=12.5 StartAngle=0.643501 EndAngle=2.49809
    g1: ArcOfCircle CenterX=0 CenterY=0 CenterZ=0 NormalX=0 NormalY=0 NormalZ=1 AngleXU=0 Radius=12.5 StartAngle=3.78509 EndAngle=5.63968
    g2: LineSegment StartX=10 StartY=7.5 StartZ=0 EndX=10 EndY=-7.5 EndZ=0
    g3: LineSegment StartX=-10 StartY=7.5 StartZ=0 EndX=-10 EndY=-7.5 EndZ=0
    g4: Circle CenterX=0 CenterY=0 CenterZ=0 NormalX=0 NormalY=0 NormalZ=1 AngleXU=0 Radius=2.5
  constraints (15):
    c: Coincident(g2,g0)
    c: Coincident(g2,g1)
    c: Vertical(g2)
    c: DistanceX(g0,g0) = 20
    c: Coincident(g3,g0)
    c: Coincident(g3,g1)
    c: Vertical(g3)
    c: Equal(g3,g2)
    c: Equal(g1,g0)
    c: Coincident(g1,g0)
    c: Coincident(g4,g0)
    c: PointOnObject(g0,g-2)
    c: Diameter(g0) = 25
    c: Diameter(g4) = 5
    c: DistanceY(g-1,g0) = 0
FEATURE [PartDesign::Pad] Pad038
  BaseFeature = -> Pad003
  Direction = (0,0,1)
  Length = 12
  Length2 = 10
  Profile = -> Sketch070
  ReferenceAxis = -> Sketch070 [N_Axis]
  Suppressed = false
  TaperAngle = -2
  Type = 0
FEATURE [PartDesign::Body] Body003  label="Шейка_шатунная"
  AllowCompound = false
  Group = -> [Sketch004,Pad003,Sketch070,Pad038]
  Origin = -> Origin004
  Placement = pos=(0,0,-25) rot=(0,0,1;0rad)
  Tip = -> Pad038
FEATURE [PartDesign::FeatureBase] Clone002
  BaseFeature = -> Body003
  Suppressed = false
FEATURE [PartDesign::Body] Body052
  AllowCompound = false
  Group = -> [Clone002]
  Origin = -> Origin053
  Placement = pos=(0,0,-35.5) rot=(0,0,1;0rad)
  Tip = -> Clone002
FEATURE [Part::MultiFuse] Fusion  label="Колевал (секция) Сбор"
  Placement = pos=(0,0,-65.5) rot=(0,0,1;0rad)
  Shapes = -> [Body052,Body054,Body055]
FEATURE [PartDesign::FeatureBase] Clone007
  BaseFeature = -> Fusion
  Suppressed = false
FEATURE [PartDesign::CoordinateSystem] Crank_shaft
  AttacherType = Attacher::AttachEngine3D
  AttachmentSupport = -> [Clone007]
  MapMode = 11
  Placement = pos=(0,0,-28.5) rot=(0,0,1;1.5708rad)
FEATURE [Sketcher::SketchObject] Sketch071
  ArcFitTolerance = 0
  FullyConstrained = true
  MakeInternals = false
  MapMode = 5
  expr: Constraints[0] = <<Dim_table>>.crank_dia2
  expr: Constraints[3] = <<Dim_table>>.axle_hole_dia
  sketch-geometry (2):
    g0: Circle CenterX=0 CenterY=0 CenterZ=0 NormalX=0 NormalY=0 NormalZ=1 AngleXU=0 Radius=12.5
    g1: Circle CenterX=0 CenterY=0 CenterZ=0 NormalX=0 NormalY=0 NormalZ=1 AngleXU=0 Radius=2.5
  constraints (4):
    c: Diameter(g0) = 25
    c: Coincident(g0,g-1)
    c: Coincident(g1,g0)
    c: Diameter(g1) = 5
FEATURE [PartDesign::Pad] Pad039
  Direction = (0,0,1)
  Length = 26
  Length2 = 10
  Profile = -> Sketch071
  ReferenceAxis = -> Sketch071 [N_Axis]
  Suppressed = false
  Type = 0
FEATURE [Sketcher::SketchObject] Sketch072
  ArcFitTolerance = 0
  AttachmentSupport = -> [XY_Plane094]
  FullyConstrained = true
  MakeInternals = false
  MapMode = 5
  expr: Constraints[17] = <<Dim_table>>.fillet_r
  expr: Constraints[18] = <<Dim_table>>.fillet_r
  expr: Constraints[23] = <<Dim_table>>.axle_hole_dia
  expr: Constraints[24] = 70
  expr: Constraints[25] = <<Dim_table>>.crank_dia2 * 1.5
  expr: Constraints[26] = <<Dim_table>>.crank_len
  sketch-geometry (14):
    g0: ArcOfCircle CenterX=0 CenterY=0 CenterZ=0 NormalX=0 NormalY=0 NormalZ=1 AngleXU=0 Radius=52.5 StartAngle=0.0396143 EndAngle=3.10198
    g1: ArcOfCircle CenterX=3e-16 CenterY=-21.25 CenterZ=0 NormalX=0 NormalY=0 NormalZ=1 AngleXU=0 Radius=18.75 StartAngle=3.49066 EndAngle=5.93412
    g2: LineSegment [constr] StartX=-17.6192 StartY=-27.6629 StartZ=0 EndX=17.6192 EndY=-27.6629 EndZ=0
    g3: LineSegment StartX=-50.4604 StartY=0 StartZ=0 EndX=-29.0881 EndY=0 EndZ=0
    g4: LineSegment StartX=-27.2087 StartY=-1.31596 StartZ=0 EndX=-17.6192 EndY=-27.6629 EndZ=0
    g5: LineSegment StartX=17.6192 StartY=-27.6629 StartZ=0 EndX=27.2087 EndY=-1.31596 EndZ=0
    g6: LineSegment StartX=29.0881 StartY=2.9e-15 StartZ=0 EndX=50.4604 EndY=2.9e-15 EndZ=0
    g7: ArcOfCircle CenterX=-29.0881 CenterY=-2 CenterZ=0 NormalX=0 NormalY=0 NormalZ=1 AngleXU=0 Radius=2 StartAngle=0.349066 EndAngle=1.5708
    g8: ArcOfCircle CenterX=29.0881 CenterY=-2 CenterZ=0 NormalX=0 NormalY=0 NormalZ=1 AngleXU=0 Radius=2 StartAngle=1.5708 EndAngle=2.79253
    g9: ArcOfCircle CenterX=50.4604 CenterY=2 CenterZ=0 NormalX=0 NormalY=0 NormalZ=1 AngleXU=0 Radius=2 StartAngle=4.71239 EndAngle=6.3228
    g10: ArcOfCircle CenterX=-50.4604 CenterY=2 CenterZ=0 NormalX=0 NormalY=0 NormalZ=1 AngleXU=0 Radius=2 StartAngle=3.10198 EndAngle=4.71239
    g11: Circle [constr] CenterX=0 CenterY=0 CenterZ=0 NormalX=0 NormalY=0 NormalZ=1 AngleXU=0 Radius=52.5
    g12: Circle CenterX=0 CenterY=0 CenterZ=0 NormalX=0 NormalY=0 NormalZ=1 AngleXU=0 Radius=2.5
    g13: Circle CenterX=3e-16 CenterY=-21.25 CenterZ=0 NormalX=0 NormalY=0 NormalZ=1 AngleXU=0 Radius=2.5
  constraints (31):
    c: Coincident(g2,g1)
    c: Coincident(g2,g1)
    c: Horizontal(g2)
    c: Horizontal(g3)
    c: Horizontal(g6)
    c: Tangent(g4,g1) = -1.5708
    c: Tangent(g5,g1) = -1.5708
    c: Tangent(g3,g7) = 1.5708
    c: Tangent(g4,g7) = 1.5708
    c: Tangent(g6,g8) = 1.5708
    c: Tangent(g5,g8) = 1.5708
    c: Tangent(g6,g9) = -1.5708
    c: Tangent(g0,g9) = -1.5708
    c: Tangent(g0,g10) = -1.5708
    c: Tangent(g3,g10) = -1.5708
    c: Symmetric(g7,g8,g-2)
    c: Symmetric(g10,g9,g-2)
    c: Radius(g10) = 2
    c: Radius(g7) = 2
    c: Coincident(g0,g-1)
    c: Coincident(g11,g0)
    c: Diameter(g11) = 105
    c: Coincident(g12,g11)
    c: Diameter(g12) = 5
    c: Angle(g5) = 1.22173
    c: Diameter(g1) = 37.5
    c: DistanceY(g1,g12) = 21.25
    c: PointOnObject(g3,g-1)
    c: Coincident(g13,g1)
    c: Equal(g13,g12)
    c: Equal(g0,g11)
FEATURE [PartDesign::Pad] Pad040
  BaseFeature = -> Pad039
  Direction = (0,0,1)
  Length = 15
  Length2 = 10
  Profile = -> Sketch072
  ReferenceAxis = -> Sketch072 [N_Axis]
  Reversed = true
  Suppressed = false
  Type = 0
FEATURE [PartDesign::Chamfer] Chamfer001
  Angle = 45
  Base = -> Pad040 [Edge14]
  BaseFeature = -> Pad040
  ChamferType = 0
  FlipDirection = false
  Size = 1.5
  Size2 = 1
  SupportTransform = false
  Suppressed = false
  UseAllEdges = false
FEATURE [PartDesign::Body] Body090  label="Шейка_и_щека_задняя"
  AllowCompound = false
  Group = -> [Sketch071,Pad039,Sketch072,Pad040,Chamfer001]
  Origin = -> Origin093
  Placement = pos=(0,0,-6.5) rot=(0,0,1;0rad)
  Tip = -> Chamfer001
FEATURE [Part::Cut] Cut  label="Шейка_и_щека_задняя001"
  Base = -> Body090
  Tool = -> Fusion
FEATURE [PartDesign::FeatureBase] Clone
  BaseFeature = -> Cut
  Suppressed = false
FEATURE [PartDesign::CoordinateSystem] LCS_2
  AttacherType = Attacher::AttachEngine3D
  AttachmentSupport = -> [Cut]
  MapMode = 11
  Placement = pos=(0,0,-21.5) rot=(0,0,1;1.5708rad)
FEATURE [App::Link] ____________________________________cl  label="Шейка_и_щека_задняя_cl001"
  AttachedBy = #LCS_2
  AttachedTo = Parent Assembly#LCS_Origin
  AttachmentOffset = pos=(0,0,36.25) rot=(0,0,1;-7.85398rad)
  LinkPlacement = pos=(0,0,57.75) rot=(0,0,1;3.14159rad)
  LinkedObject = -> Body091
  Placement = pos=(0,0,57.75) rot=(0,0,1;3.14159rad)
  SolverId = Asm4EE
  expr: .AttachmentOffset.Rotation.Angle = -<<Variables>>.Crank_Angle - 90
  expr: Placement = LCS_Origin.Placement * AttachmentOffset * LCS_2.Placement ^ -1
FEATURE [Sketcher::SketchObject] Sketch073
  ArcFitTolerance = 0
  AttachmentSupport = -> [XY_Plane085]
  FullyConstrained = true
  MakeInternals = false
  MapMode = 5
  expr: Constraints[6] = <<Dim_table>>.crank_dia2 + <<Dim_table>>.zazor
  expr: Constraints[7] = <<Dim_table>>.crank_dia2 * 1.5
  expr: Constraints[8] = <<Dim_table>>.inter_shaft_len
  sketch-geometry (4):
    g0: Circle CenterX=0 CenterY=0 CenterZ=0 NormalX=0 NormalY=0 NormalZ=1 AngleXU=0 Radius=12.75
    g1: Circle CenterX=0 CenterY=0 CenterZ=0 NormalX=0 NormalY=0 NormalZ=1 AngleXU=0 Radius=18.75
    g2: Circle CenterX=100 CenterY=0 CenterZ=0 NormalX=0 NormalY=0 NormalZ=1 AngleXU=0 Radius=12.75
    g3: Circle CenterX=100 CenterY=0 CenterZ=0 NormalX=0 NormalY=0 NormalZ=1 AngleXU=0 Radius=18.75
  constraints (9):
    c: Coincident(g0,g-1)
    c: Coincident(g1,g0)
    c: PointOnObject(g2,g-1)
    c: Coincident(g3,g2)
    c: Equal(g0,g2)
    c: Equal(g1,g3)
    c: Diameter(g0) = 25.5
    c: Diameter(g1) = 37.5
    c: DistanceX(g-1,g2) = 100
FEATURE [PartDesign::Pad] Pad041
  BaseFeature = -> Pad036
  Direction = (0,0,1)
  Length = 10
  Length2 = 10
  Profile = -> Sketch073
  ReferenceAxis = -> Sketch073 [N_Axis]
  Suppressed = false
  Type = 0
FEATURE [PartDesign::Body] ___________________________  label="корпус_верхний"
  AllowCompound = false
  Group = -> [LCS_Origin006,Sketch067,Pad036,Sketch073,Pad041]
  Origin = -> Origin084
  Tip = -> Pad041
FEATURE [Sketcher::SketchObject] Sketch074
  ArcFitTolerance = 0
  AttachmentSupport = -> [XY_Plane076]
  FullyConstrained = true
  MakeInternals = false
  MapMode = 5
  expr: Constraints[14] = <<Dim_table>>.ecc_dia * 1.2
  expr: Constraints[33] = <<Dim_table>>.crank_dia2
  expr: Constraints[34] = <<Dim_table>>.inter_shaft_len * 2.2
  expr: Constraints[46] = <<Dim_table>>.axle_hole_dia
  expr: Constraints[48] = 32
  expr: Constraints[53] = <<Dim_table>>.inter_shaft_len * 1.8
  sketch-geometry (25):
    g0: LineSegment [constr] StartX=-42 StartY=-90 StartZ=0 EndX=42 EndY=-90 EndZ=0
    g1: LineSegment [constr] StartX=90 StartY=-42 StartZ=0 EndX=90 EndY=42 EndZ=0
    g2: LineSegment [constr] StartX=42 StartY=90 StartZ=0 EndX=-42 EndY=90 EndZ=0
    g3: LineSegment [constr] StartX=-90 StartY=42 StartZ=0 EndX=-90 EndY=-42 EndZ=0
    g4: ArcOfCircle [constr] CenterX=-42 CenterY=42 CenterZ=0 NormalX=0 NormalY=0 NormalZ=1 AngleXU=0 Radius=48 StartAngle=1.5708 EndAngle=3.14159
    g5: ArcOfCircle [constr] CenterX=42 CenterY=42 CenterZ=0 NormalX=0 NormalY=0 NormalZ=1 AngleXU=0 Radius=48 StartAngle=1e-16 EndAngle=1.5708
    g6: ArcOfCircle [constr] CenterX=-42 CenterY=-42 CenterZ=0 NormalX=0 NormalY=0 NormalZ=1 AngleXU=0 Radius=48 StartAngle=3.14159 EndAngle=4.71239
    g7: ArcOfCircle [constr] CenterX=42 CenterY=-42 CenterZ=0 NormalX=0 NormalY=0 NormalZ=1 AngleXU=0 Radius=48 StartAngle=4.71239 EndAngle=6.28319
    g8: LineSegment [constr] StartX=-90 StartY=-42 StartZ=0 EndX=90 EndY=42 EndZ=0
    g9: GeomPoint [constr] X=0 Y=0 Z=0
    g10: ArcOfCircle CenterX=-97.5 CenterY=97.5 CenterZ=0 NormalX=0 NormalY=0 NormalZ=1 AngleXU=0 Radius=12.5 StartAngle=1.5708 EndAngle=3.14159
    g11: LineSegment StartX=97.5 StartY=110 StartZ=0 EndX=-97.5 EndY=110 EndZ=0
    g12: ArcOfCircle CenterX=97.5 CenterY=97.5 CenterZ=0 NormalX=0 NormalY=0 NormalZ=1 AngleXU=0 Radius=12.5 StartAngle=4.16e-13 EndAngle=1.5708
    g13: LineSegment StartX=110 StartY=-97.5 StartZ=0 EndX=110 EndY=97.5 EndZ=0
    g14: ArcOfCircle CenterX=97.5 CenterY=-97.5 CenterZ=0 NormalX=0 NormalY=0 NormalZ=1 AngleXU=0 Radius=12.5 StartAngle=4.71239 EndAngle=6.28319
    g15: LineSegment StartX=-97.5 StartY=-110 StartZ=0 EndX=97.5 EndY=-110 EndZ=0
    g16: ArcOfCircle CenterX=-97.5 CenterY=-97.5 CenterZ=0 NormalX=0 NormalY=0 NormalZ=1 AngleXU=0 Radius=12.5 StartAngle=3.14159 EndAngle=4.71239
    g17: LineSegment StartX=-110 StartY=97.5 StartZ=0 EndX=-110 EndY=-97.5 EndZ=0
    g18: LineSegment [constr] StartX=-97.5 StartY=110 StartZ=0 EndX=97.5 EndY=-110 EndZ=0
    g19: GeomPoint [constr] X=0 Y=0 Z=0
    g20: Circle CenterX=-97.5 CenterY=97.5 CenterZ=0 NormalX=0 NormalY=0 NormalZ=1 AngleXU=0 Radius=2.5
    g21: Circle CenterX=97.5 CenterY=97.5 CenterZ=0 NormalX=0 NormalY=0 NormalZ=1 AngleXU=0 Radius=2.5
    g22: Circle CenterX=-97.5 CenterY=-97.5 CenterZ=0 NormalX=0 NormalY=0 NormalZ=1 AngleXU=0 Radius=2.5
    g23: Circle CenterX=97.5 CenterY=-97.5 CenterZ=0 NormalX=0 NormalY=0 NormalZ=1 AngleXU=0 Radius=2.5
    g24: Circle CenterX=0 CenterY=0 CenterZ=0 NormalX=0 NormalY=0 NormalZ=1 AngleXU=0 Radius=16
  constraints (54):
    c: Horizontal(g0)
    c: Horizontal(g2)
    c: Vertical(g1)
    c: Vertical(g3)
    c: Tangent(g2,g4) = -1.5708
    c: Tangent(g3,g4) = -1.5708
    c: Tangent(g2,g5) = -1.5708
    c: Tangent(g1,g5) = -1.5708
    c: Tangent(g3,g6) = -1.5708
    c: Tangent(g0,g6) = -1.5708
    c: Tangent(g0,g7) = -1.5708
    c: Tangent(g1,g7) = -1.5708
    c: Equal(g4,g5)
    c: Equal(g5,g7)
    c: Diameter(g4) = 96
    c: Symmetric(g2,g0,g-1)
    c: Coincident(g8,g3)
    c: Coincident(g8,g1)
    c: PointOnObject(g9,g8)
    c: Horizontal(g15)
    c: Horizontal(g11)
    c: Vertical(g13)
    c: Vertical(g17)
    c: Tangent(g11,g10) = -1.5708
    c: Tangent(g17,g10) = -1.5708
    c: Tangent(g11,g12) = -1.5708
    c: Tangent(g13,g12) = -1.5708
    c: Tangent(g17,g16) = -1.5708
    c: Tangent(g15,g16) = -1.5708
    c: Tangent(g15,g14) = -1.5708
    c: Tangent(g13,g14) = -1.5708
    c: Equal(g10,g12)
    c: Equal(g12,g14)
    c: Diameter(g10) = 25
    c: DistanceY(g15,g11) = 220
    c: Symmetric(g10,g16,g-1)
    c: Coincident(g18,g10)
    c: Coincident(g18,g14)
    c: PointOnObject(g19,g18)
    c: Coincident(g20,g10)
    c: Coincident(g21,g12)
    c: Coincident(g22,g16)
    c: Coincident(g23,g14)
    c: Equal(g22,g23)
    c: Equal(g23,g21)
    c: Equal(g21,g20)
    c: Diameter(g20) = 5
    c: Coincident(g24,g9)
    c: Diameter(g24) = 32
    c: Coincident(g9,g19)
    c: Coincident(g-1,g9)
    c: Equal(g11,g13)
    c: Equal(g2,g1)
    c: DistanceX(g3,g1) = 180
FEATURE [PartDesign::CoordinateSystem] Shtok004
  AttacherType = Attacher::AttachEngine3D
  AttachmentSupport = -> [Sketch074]
  MapMode = 2
FEATURE [PartDesign::Pad] Pad042
  Direction = (0,0,1)
  Length = 15
  Length2 = 10
  Profile = -> Sketch074
  ReferenceAxis = -> Sketch074 [N_Axis]
  Reversed = true
  Suppressed = false
  Type = 0
FEATURE [PartDesign::Pad] Pad043
  BaseFeature = -> Pad042
  Direction = (0,-1e-16,-1)
  Length = 25
  Length2 = 10
  Profile = -> Sketch060
  ReferenceAxis = -> Sketch060 [N_Axis]
  Suppressed = false
  Type = 0
FEATURE [PartDesign::Pocket] Pocket036
  BaseFeature = -> Pad043
  Direction = (0,1e-16,1)
  Length = 10.5
  Length2 = 5
  Profile = -> Sketch064
  ReferenceAxis = -> Sketch064 [N_Axis]
  Reversed = true
  Suppressed = false
  Type = 0
FEATURE [PartDesign::Body] Body076  label="корпус_нижний"
  AllowCompound = false
  Group = -> [Shtok004,Sketch060,Sketch064,Sketch074,Pad042,Pad043,Pocket036]
  Origin = -> Origin077
  Tip = -> Pocket036
FEATURE [App::Link] _________________________  label="корпус_нижний001"
  AttachedBy = #Shtok004
  AttachedTo = Parent Assembly#LCS_Origin
  AttachmentOffset = pos=(0,0,-5.25) rot=(0,0,1;0rad)
  LinkPlacement = pos=(0,0,-5.25) rot=(0,0,1;0rad)
  LinkedObject = -> Body076
  Placement = pos=(0,0,-5.25) rot=(0,0,1;0rad)
  SolverId = Asm4EE
  expr: Placement = LCS_Origin.Placement * AttachmentOffset * Shtok004.Placement ^ -1
FEATURE [App::Link] ___________________________002  label="корпус_верхний001"
  AttachedBy = #LCS_Origin006
  AttachedTo = Parent Assembly#LCS_Origin
  AttachmentOffset = pos=(0,0,22) rot=(0,0,1;0rad)
  LinkPlacement = pos=(0,0,22) rot=(0,0,1;0rad)
  LinkedObject = -> ___________________________
  Placement = pos=(0,0,22) rot=(0,0,1;0rad)
  SolverId = Asm4EE
  expr: Placement = LCS_Origin.Placement * AttachmentOffset * LCS_Origin006.Placement ^ -1
FEATURE [Sketcher::SketchObject] Sketch075
  ArcFitTolerance = 0
  AttachmentSupport = -> [XY_Plane096]
  FullyConstrained = true
  MakeInternals = false
  MapMode = 5
  expr: Constraints[14] = <<Dim_table>>.inter_shaft_len * 2.15
  expr: Constraints[15] = <<Dim_table>>.ecc_dia * 1.2
  expr: Constraints[16] = <<Dim_table>>.inter_shaft_len * 1.85
  expr: Constraints[22] = <<Dim_table>>.inter_shaft_len / 2
  expr: Constraints[37] = <<Dim_table>>.inter_shaft_len * 2.35
  expr: Constraints[38] = <<Dim_table>>.crank_dia2
  expr: Constraints[39] = <<Dim_table>>.inter_shaft_len * 2
  expr: Constraints[45] = <<Dim_table>>.inter_shaft_len / 2
  expr: Constraints[53] = <<Dim_table>>.axle_hole_dia
  expr: Constraints[56] = <<Dim_table>>.inter_shaft_len
  expr: Constraints[58] = <<Dim_table>>.inter_shaft_len * 0.95
  sketch-geometry (26):
    g0: LineSegment [constr] StartX=-9.5 StartY=-92.5 StartZ=0 EndX=109.5 EndY=-92.5 EndZ=0
    g1: LineSegment [constr] StartX=157.5 StartY=-44.5 StartZ=0 EndX=157.5 EndY=44.5 EndZ=0
    g2: LineSegment [constr] StartX=109.5 StartY=92.5 StartZ=0 EndX=-9.5 EndY=92.5 EndZ=0
    g3: LineSegment [constr] StartX=-57.5 StartY=44.5 StartZ=0 EndX=-57.5 EndY=-44.5 EndZ=0
    g4: ArcOfCircle [constr] CenterX=-9.5 CenterY=44.5 CenterZ=0 NormalX=0 NormalY=0 NormalZ=1 AngleXU=0 Radius=48 StartAngle=1.5708 EndAngle=3.14159
    g5: ArcOfCircle [constr] CenterX=109.5 CenterY=44.5 CenterZ=0 NormalX=0 NormalY=0 NormalZ=1 AngleXU=0 Radius=48 StartAngle=0 EndAngle=1.5708
    g6: ArcOfCircle [constr] CenterX=-9.5 CenterY=-44.5 CenterZ=0 NormalX=0 NormalY=0 NormalZ=1 AngleXU=0 Radius=48 StartAngle=3.14159 EndAngle=4.71239
    g7: ArcOfCircle [constr] CenterX=109.5 CenterY=-44.5 CenterZ=0 NormalX=0 NormalY=0 NormalZ=1 AngleXU=0 Radius=48 StartAngle=4.71239 EndAngle=6.28319
    g8: LineSegment [constr] StartX=-57.5 StartY=-44.5 StartZ=0 EndX=157.5 EndY=44.5 EndZ=0
    g9: GeomPoint [constr] X=50 Y=0 Z=0
    g10: ArcOfCircle CenterX=-55 CenterY=87.5 CenterZ=0 NormalX=0 NormalY=0 NormalZ=1 AngleXU=0 Radius=12.5 StartAngle=1.5708 EndAngle=3.14159
    g11: LineSegment StartX=155 StartY=100 StartZ=0 EndX=-55 EndY=100 EndZ=0
    g12: ArcOfCircle CenterX=155 CenterY=87.5 CenterZ=0 NormalX=0 NormalY=0 NormalZ=1 AngleXU=0 Radius=12.5 StartAngle=7.01e-14 EndAngle=1.5708
    g13: LineSegment StartX=167.5 StartY=-87.5 StartZ=0 EndX=167.5 EndY=87.5 EndZ=0
    g14: ArcOfCircle CenterX=155 CenterY=-87.5 CenterZ=0 NormalX=0 NormalY=0 NormalZ=1 AngleXU=0 Radius=12.5 StartAngle=4.71239 EndAngle=6.28319
    g15: LineSegment StartX=-55 StartY=-100 StartZ=0 EndX=155 EndY=-100 EndZ=0
    g16: ArcOfCircle CenterX=-55 CenterY=-87.5 CenterZ=0 NormalX=0 NormalY=0 NormalZ=1 AngleXU=0 Radius=12.5 StartAngle=3.14159 EndAngle=4.71239
    g17: LineSegment StartX=-67.5 StartY=87.5 StartZ=0 EndX=-67.5 EndY=-87.5 EndZ=0
    g18: LineSegment [constr] StartX=-55 StartY=100 StartZ=0 EndX=155 EndY=-100 EndZ=0
    g19: GeomPoint [constr] X=50 Y=0 Z=0
    g20: Circle CenterX=-55 CenterY=87.5 CenterZ=0 NormalX=0 NormalY=0 NormalZ=1 AngleXU=0 Radius=2.5
    g21: Circle CenterX=155 CenterY=87.5 CenterZ=0 NormalX=0 NormalY=0 NormalZ=1 AngleXU=0 Radius=2.5
    g22: Circle CenterX=-55 CenterY=-87.5 CenterZ=0 NormalX=0 NormalY=0 NormalZ=1 AngleXU=0 Radius=2.5
    g23: Circle CenterX=155 CenterY=-87.5 CenterZ=0 NormalX=0 NormalY=0 NormalZ=1 AngleXU=0 Radius=2.5
    g24: Circle CenterX=0 CenterY=0 CenterZ=0 NormalX=0 NormalY=0 NormalZ=1 AngleXU=0 Radius=47.5
    g25: Circle CenterX=100 CenterY=0 CenterZ=0 NormalX=0 NormalY=0 NormalZ=1 AngleXU=0 Radius=47.5
  constraints (59):
    c: Horizontal(g0)
    c: Horizontal(g2)
    c: Vertical(g1)
    c: Vertical(g3)
    c: Tangent(g2,g4) = -1.5708
    c: Tangent(g3,g4) = -1.5708
    c: Tangent(g2,g5) = -1.5708
    c: Tangent(g1,g5) = -1.5708
    c: Tangent(g3,g6) = -1.5708
    c: Tangent(g0,g6) = -1.5708
    c: Tangent(g0,g7) = -1.5708
    c: Tangent(g1,g7) = -1.5708
    c: Equal(g4,g5)
    c: Equal(g5,g7)
    c: DistanceX(g3,g1) = 215
    c: Diameter(g4) = 96
    c: DistanceY(g0,g2) = 185
    c: Symmetric(g2,g0,g-1)
    c: Coincident(g8,g3)
    c: Coincident(g8,g1)
    c: PointOnObject(g9,g-1)
    c: PointOnObject(g9,g8)
    c: DistanceX(g-1,g9) = 50
    c: Horizontal(g15)
    c: Horizontal(g11)
    c: Vertical(g13)
    c: Vertical(g17)
    c: Tangent(g11,g10) = -1.5708
    c: Tangent(g17,g10) = -1.5708
    c: Tangent(g11,g12) = -1.5708
    c: Tangent(g13,g12) = -1.5708
    c: Tangent(g17,g16) = -1.5708
    c: Tangent(g15,g16) = -1.5708
    c: Tangent(g15,g14) = -1.5708
    c: Tangent(g13,g14) = -1.5708
    c: Equal(g10,g12)
    c: Equal(g12,g14)
    c: DistanceX(g17,g13) = 235
    c: Diameter(g10) = 25
    c: DistanceY(g15,g11) = 200
    c: Symmetric(g10,g16,g-1)
    c: Coincident(g18,g10)
    c: Coincident(g18,g14)
    c: PointOnObject(g19,g-1)
    c: PointOnObject(g19,g18)
    c: DistanceX(g-1,g19) = 50
    c: Coincident(g20,g10)
    c: Coincident(g21,g12)
    c: Coincident(g22,g16)
    c: Coincident(g23,g14)
    c: Equal(g22,g23)
    c: Equal(g23,g21)
    c: Equal(g21,g20)
    c: Diameter(g20) = 5
    c: Coincident(g24,g-1)
    c: PointOnObject(g25,g-1)
    c: DistanceX(g24,g25) = 100
    c: Equal(g25,g24)
    c: Diameter(g24) = 95
FEATURE [Sketcher::SketchObject] Sketch076
  ArcFitTolerance = 0
  AttachmentSupport = -> [XY_Plane096]
  FullyConstrained = true
  MakeInternals = false
  MapMode = 5
  expr: Constraints[14] = <<Dim_table>>.inter_shaft_len * 2.15
  expr: Constraints[15] = <<Dim_table>>.ecc_dia * 1.2
  expr: Constraints[16] = <<Dim_table>>.inter_shaft_len * 1.85
  expr: Constraints[22] = <<Dim_table>>.inter_shaft_len / 2
  expr: Constraints[37] = <<Dim_table>>.inter_shaft_len * 2.35
  expr: Constraints[38] = <<Dim_table>>.crank_dia2
  expr: Constraints[39] = <<Dim_table>>.inter_shaft_len * 2
  expr: Constraints[45] = <<Dim_table>>.inter_shaft_len / 2
  expr: Constraints[53] = <<Dim_table>>.axle_hole_dia
  sketch-geometry (24):
    g0: LineSegment StartX=-9.5 StartY=-92.5 StartZ=0 EndX=109.5 EndY=-92.5 EndZ=0
    g1: LineSegment StartX=157.5 StartY=-44.5 StartZ=0 EndX=157.5 EndY=44.5 EndZ=0
    g2: LineSegment StartX=109.5 StartY=92.5 StartZ=0 EndX=-9.5 EndY=92.5 EndZ=0
    g3: LineSegment StartX=-57.5 StartY=44.5 StartZ=0 EndX=-57.5 EndY=-44.5 EndZ=0
    g4: ArcOfCircle CenterX=-9.5 CenterY=44.5 CenterZ=0 NormalX=0 NormalY=0 NormalZ=1 AngleXU=0 Radius=48 StartAngle=1.5708 EndAngle=3.14159
    g5: ArcOfCircle CenterX=109.5 CenterY=44.5 CenterZ=0 NormalX=0 NormalY=0 NormalZ=1 AngleXU=0 Radius=48 StartAngle=0 EndAngle=1.5708
    g6: ArcOfCircle CenterX=-9.5 CenterY=-44.5 CenterZ=0 NormalX=0 NormalY=0 NormalZ=1 AngleXU=0 Radius=48 StartAngle=3.14159 EndAngle=4.71239
    g7: ArcOfCircle CenterX=109.5 CenterY=-44.5 CenterZ=0 NormalX=0 NormalY=0 NormalZ=1 AngleXU=0 Radius=48 StartAngle=4.71239 EndAngle=6.28319
    g8: LineSegment [constr] StartX=-57.5 StartY=-44.5 StartZ=0 EndX=157.5 EndY=44.5 EndZ=0
    g9: GeomPoint [constr] X=50 Y=0 Z=0
    g10: ArcOfCircle CenterX=-55 CenterY=87.5 CenterZ=0 NormalX=0 NormalY=0 NormalZ=1 AngleXU=0 Radius=12.5 StartAngle=1.5708 EndAngle=3.14159
    g11: LineSegment StartX=155 StartY=100 StartZ=0 EndX=-55 EndY=100 EndZ=0
    g12: ArcOfCircle CenterX=155 CenterY=87.5 CenterZ=0 NormalX=0 NormalY=0 NormalZ=1 AngleXU=0 Radius=12.5 StartAngle=7e-14 EndAngle=1.5708
    g13: LineSegment StartX=167.5 StartY=-87.5 StartZ=0 EndX=167.5 EndY=87.5 EndZ=0
    g14: ArcOfCircle CenterX=155 CenterY=-87.5 CenterZ=0 NormalX=0 NormalY=0 NormalZ=1 AngleXU=0 Radius=12.5 StartAngle=4.71239 EndAngle=6.28319
    g15: LineSegment StartX=-55 StartY=-100 StartZ=0 EndX=155 EndY=-100 EndZ=0
    g16: ArcOfCircle CenterX=-55 CenterY=-87.5 CenterZ=0 NormalX=0 NormalY=0 NormalZ=1 AngleXU=0 Radius=12.5 StartAngle=3.14159 EndAngle=4.71239
    g17: LineSegment StartX=-67.5 StartY=87.5 StartZ=0 EndX=-67.5 EndY=-87.5 EndZ=0
    g18: LineSegment [constr] StartX=-55 StartY=100 StartZ=0 EndX=155 EndY=-100 EndZ=0
    g19: GeomPoint [constr] X=50 Y=0 Z=0
    g20: Circle CenterX=-55 CenterY=87.5 CenterZ=0 NormalX=0 NormalY=0 NormalZ=1 AngleXU=0 Radius=2.5
    g21: Circle CenterX=155 CenterY=87.5 CenterZ=0 NormalX=0 NormalY=0 NormalZ=1 AngleXU=0 Radius=2.5
    g22: Circle CenterX=-55 CenterY=-87.5 CenterZ=0 NormalX=0 NormalY=0 NormalZ=1 AngleXU=0 Radius=2.5
    g23: Circle CenterX=155 CenterY=-87.5 CenterZ=0 NormalX=0 NormalY=0 NormalZ=1 AngleXU=0 Radius=2.5
  constraints (54):
    c: Horizontal(g0)
    c: Horizontal(g2)
    c: Vertical(g1)
    c: Vertical(g3)
    c: Tangent(g2,g4) = -1.5708
    c: Tangent(g3,g4) = -1.5708
    c: Tangent(g2,g5) = -1.5708
    c: Tangent(g1,g5) = -1.5708
    c: Tangent(g3,g6) = -1.5708
    c: Tangent(g0,g6) = -1.5708
    c: Tangent(g0,g7) = -1.5708
    c: Tangent(g1,g7) = -1.5708
    c: Equal(g4,g5)
    c: Equal(g5,g7)
    c: DistanceX(g3,g1) = 215
    c: Diameter(g4) = 96
    c: DistanceY(g0,g2) = 185
    c: Symmetric(g2,g0,g-1)
    c: Coincident(g8,g3)
    c: Coincident(g8,g1)
    c: PointOnObject(g9,g-1)
    c: PointOnObject(g9,g8)
    c: DistanceX(g-1,g9) = 50
    c: Horizontal(g15)
    c: Horizontal(g11)
    c: Vertical(g13)
    c: Vertical(g17)
    c: Tangent(g11,g10) = -1.5708
    c: Tangent(g17,g10) = -1.5708
    c: Tangent(g11,g12) = -1.5708
    c: Tangent(g13,g12) = -1.5708
    c: Tangent(g17,g16) = -1.5708
    c: Tangent(g15,g16) = -1.5708
    c: Tangent(g15,g14) = -1.5708
    c: Tangent(g13,g14) = -1.5708
    c: Equal(g10,g12)
    c: Equal(g12,g14)
    c: DistanceX(g17,g13) = 235
    c: Diameter(g10) = 25
    c: DistanceY(g15,g11) = 200
    c: Symmetric(g10,g16,g-1)
    c: Coincident(g18,g10)
    c: Coincident(g18,g14)
    c: PointOnObject(g19,g-1)
    c: PointOnObject(g19,g18)
    c: DistanceX(g-1,g19) = 50
    c: Coincident(g20,g10)
    c: Coincident(g21,g12)
    c: Coincident(g22,g16)
    c: Coincident(g23,g14)
    c: Equal(g22,g23)
    c: Equal(g23,g21)
    c: Equal(g21,g20)
    c: Diameter(g20) = 5
FEATURE [PartDesign::CoordinateSystem] LCS_Origin007
  AttacherType = Attacher::AttachEngine3D
  AttachmentSupport = -> [X_Axis094]
  MapMode = 2
FEATURE [PartDesign::Pad] Pad044
  Direction = (0,0,1)
  Length = 6
  Length2 = 10
  Profile = -> Sketch075
  ReferenceAxis = -> Sketch075 [N_Axis]
  Suppressed = false
  Type = 0
FEATURE [PartDesign::Pad] Pad045
  BaseFeature = -> Pad044
  Direction = (0,0,1)
  Length = 16.75
  Length2 = 10
  Profile = -> Sketch076
  ReferenceAxis = -> Sketch076 [N_Axis]
  Suppressed = false
  Type = 0
FEATURE [PartDesign::Body] Body_2  label="проставка_корпуса_с_шестернями"
  AllowCompound = false
  Group = -> [LCS_Origin007,Sketch075,Pad044,Sketch076,Pad045]
  Origin = -> Origin095
  Tip = -> Pad045
FEATURE [App::Link] _________________________________________________________  label="проставка_корпуса_с_шестернями001"
  AttachedBy = #LCS_Origin007
  AttachedTo = Parent Assembly#LCS_Origin
  AttachmentOffset = pos=(0,0,5.25) rot=(0,0,1;0rad)
  LinkPlacement = pos=(0,0,5.25) rot=(0,0,1;0rad)
  LinkedObject = -> Body_2
  Placement = pos=(0,0,5.25) rot=(0,0,1;0rad)
  SolverId = Asm4EE
  expr: Placement = LCS_Origin.Placement * AttachmentOffset * LCS_Origin007.Placement ^ -1
FEATURE [Sketcher::SketchObject] Sketch077
  ArcFitTolerance = 0
  AttachmentSupport = -> [XY_Plane096]
  FullyConstrained = true
  MakeInternals = false
  MapMode = 5
  expr: Constraints[14] = <<Dim_table>>.inter_shaft_len * 2.15
  expr: Constraints[15] = <<Dim_table>>.ecc_dia * 1.2
  expr: Constraints[16] = <<Dim_table>>.inter_shaft_len * 1.85
  expr: Constraints[22] = <<Dim_table>>.inter_shaft_len / 2
  expr: Constraints[37] = <<Dim_table>>.inter_shaft_len * 2.35
  expr: Constraints[38] = <<Dim_table>>.crank_dia2
  expr: Constraints[39] = <<Dim_table>>.inter_shaft_len * 2
  expr: Constraints[45] = <<Dim_table>>.inter_shaft_len / 2
  expr: Constraints[53] = <<Dim_table>>.axle_hole_dia
  sketch-geometry (36):
    g0: LineSegment [constr] StartX=-9.5 StartY=-92.5 StartZ=0 EndX=109.5 EndY=-92.5 EndZ=0
    g1: LineSegment StartX=157.5 StartY=-44.5 StartZ=0 EndX=157.5 EndY=44.5 EndZ=0
    g2: LineSegment [constr] StartX=109.5 StartY=92.5 StartZ=0 EndX=-9.5 EndY=92.5 EndZ=0
    g3: LineSegment StartX=-57.5 StartY=44.5 StartZ=0 EndX=-57.5 EndY=-44.5 EndZ=0
    g4: ArcOfCircle CenterX=-9.5 CenterY=44.5 CenterZ=0 NormalX=0 NormalY=0 NormalZ=1 AngleXU=0 Radius=48 StartAngle=1.5708 EndAngle=3.14159
    g5: ArcOfCircle CenterX=109.5 CenterY=44.5 CenterZ=0 NormalX=0 NormalY=0 NormalZ=1 AngleXU=0 Radius=48 StartAngle=0 EndAngle=1.5708
    g6: ArcOfCircle CenterX=-9.5 CenterY=-44.5 CenterZ=0 NormalX=0 NormalY=0 NormalZ=1 AngleXU=0 Radius=48 StartAngle=3.14159 EndAngle=4.71239
    g7: ArcOfCircle CenterX=109.5 CenterY=-44.5 CenterZ=0 NormalX=0 NormalY=0 NormalZ=1 AngleXU=0 Radius=48 StartAngle=4.71239 EndAngle=6.28319
    g8: LineSegment [constr] StartX=-57.5 StartY=-44.5 StartZ=0 EndX=157.5 EndY=44.5 EndZ=0
    g9: GeomPoint [constr] X=50 Y=0 Z=0
    g10: ArcOfCircle CenterX=-55 CenterY=87.5 CenterZ=0 NormalX=0 NormalY=0 NormalZ=1 AngleXU=0 Radius=12.5 StartAngle=1.5708 EndAngle=3.14159
    g11: LineSegment [constr] StartX=155 StartY=100 StartZ=0 EndX=-55 EndY=100 EndZ=0
    g12: ArcOfCircle CenterX=155 CenterY=87.5 CenterZ=0 NormalX=0 NormalY=0 NormalZ=1 AngleXU=0 Radius=12.5 StartAngle=1.549e-13 EndAngle=1.5708
    g13: LineSegment StartX=167.5 StartY=-87.5 StartZ=0 EndX=167.5 EndY=87.5 EndZ=0
    g14: ArcOfCircle CenterX=155 CenterY=-87.5 CenterZ=0 NormalX=0 NormalY=0 NormalZ=1 AngleXU=0 Radius=12.5 StartAngle=4.71239 EndAngle=6.28319
    g15: LineSegment [constr] StartX=-55 StartY=-100 StartZ=0 EndX=155 EndY=-100 EndZ=0
    g16: ArcOfCircle CenterX=-55 CenterY=-87.5 CenterZ=0 NormalX=0 NormalY=0 NormalZ=1 AngleXU=0 Radius=12.5 StartAngle=3.14159 EndAngle=4.71239
    g17: LineSegment StartX=-67.5 StartY=87.5 StartZ=0 EndX=-67.5 EndY=-87.5 EndZ=0
    g18: LineSegment [constr] StartX=-55 StartY=100 StartZ=0 EndX=155 EndY=-100 EndZ=0
    g19: GeomPoint [constr] X=50 Y=0 Z=0
    g20: Circle CenterX=-55 CenterY=87.5 CenterZ=0 NormalX=0 NormalY=0 NormalZ=1 AngleXU=0 Radius=2.5
    g21: Circle CenterX=155 CenterY=87.5 CenterZ=0 NormalX=0 NormalY=0 NormalZ=1 AngleXU=0 Radius=2.5
    g22: Circle CenterX=-55 CenterY=-87.5 CenterZ=0 NormalX=0 NormalY=0 NormalZ=1 AngleXU=0 Radius=2.5
    g23: Circle CenterX=155 CenterY=-87.5 CenterZ=0 NormalX=0 NormalY=0 NormalZ=1 AngleXU=0 Radius=2.5
    g24: LineSegment StartX=-9.5 StartY=-92.5 StartZ=0 EndX=-2 EndY=-92.5 EndZ=0
    g25: LineSegment StartX=-2 StartY=-92.5 StartZ=0 EndX=-2 EndY=-100 EndZ=0
    g26: LineSegment StartX=-2 StartY=-100 StartZ=0 EndX=-55 EndY=-100 EndZ=0
    g27: LineSegment StartX=102 StartY=-92.5 StartZ=0 EndX=102 EndY=-100 EndZ=0
    g28: LineSegment StartX=102 StartY=-100 StartZ=0 EndX=155 EndY=-100 EndZ=0
    g29: LineSegment StartX=102 StartY=-92.5 StartZ=0 EndX=109.5 EndY=-92.5 EndZ=0
    g30: LineSegment StartX=-9.5 StartY=92.5 StartZ=0 EndX=-2 EndY=92.5 EndZ=0
    g31: LineSegment StartX=-2 StartY=92.5 StartZ=0 EndX=-2 EndY=100 EndZ=0
    g32: LineSegment StartX=-2 StartY=100 StartZ=0 EndX=-55 EndY=100 EndZ=0
    g33: LineSegment StartX=109.5 StartY=92.5 StartZ=0 EndX=102 EndY=92.5 EndZ=0
    g34: LineSegment StartX=102 StartY=92.5 StartZ=0 EndX=102 EndY=100 EndZ=0
    g35: LineSegment StartX=102 StartY=100 StartZ=0 EndX=155 EndY=100 EndZ=0
  constraints (84):
    c: Horizontal(g0)
    c: Horizontal(g2)
    c: Vertical(g1)
    c: Vertical(g3)
    c: Tangent(g2,g4) = -1.5708
    c: Tangent(g3,g4) = -1.5708
    c: Tangent(g2,g5) = -1.5708
    c: Tangent(g1,g5) = -1.5708
    c: Tangent(g3,g6) = -1.5708
    c: Tangent(g0,g6) = -1.5708
    c: Tangent(g0,g7) = -1.5708
    c: Tangent(g1,g7) = -1.5708
    c: Equal(g4,g5)
    c: Equal(g5,g7)
    c: DistanceX(g3,g1) = 215
    c: Diameter(g4) = 96
    c: DistanceY(g0,g2) = 185
    c: Symmetric(g2,g0,g-1)
    c: Coincident(g8,g3)
    c: Coincident(g8,g1)
    c: PointOnObject(g9,g-1)
    c: PointOnObject(g9,g8)
    c: DistanceX(g-1,g9) = 50
    c: Horizontal(g15)
    c: Horizontal(g11)
    c: Vertical(g13)
    c: Vertical(g17)
    c: Tangent(g11,g10) = -1.5708
    c: Tangent(g17,g10) = -1.5708
    c: Tangent(g11,g12) = -1.5708
    c: Tangent(g13,g12) = -1.5708
    c: Tangent(g17,g16) = -1.5708
    c: Tangent(g15,g16) = -1.5708
    c: Tangent(g15,g14) = -1.5708
    c: Tangent(g13,g14) = -1.5708
    c: Equal(g10,g12)
    c: Equal(g12,g14)
    c: DistanceX(g17,g13) = 235
    c: Diameter(g10) = 25
    c: DistanceY(g15,g11) = 200
    c: Symmetric(g10,g16,g-1)
    c: Coincident(g18,g10)
    c: Coincident(g18,g14)
    c: PointOnObject(g19,g-1)
    c: PointOnObject(g19,g18)
    c: DistanceX(g-1,g19) = 50
    c: Coincident(g20,g10)
    c: Coincident(g21,g12)
    c: Coincident(g22,g16)
    c: Coincident(g23,g14)
    c: Equal(g22,g23)
    c: Equal(g23,g21)
    c: Equal(g21,g20)
    c: Diameter(g20) = 5
    c: Coincident(g24,g6)
    c: Coincident(g25,g24)
    c: Coincident(g26,g25)
    c: Coincident(g26,g16)
    c: Coincident(g28,g27)
    c: Coincident(g28,g14)
    c: Coincident(g29,g27)
    c: Coincident(g29,g7)
    c: Coincident(g30,g4)
    c: Coincident(g31,g30)
    c: Coincident(g32,g31)
    c: Coincident(g32,g10)
    c: Coincident(g33,g5)
    c: Coincident(g34,g33)
    c: Coincident(g35,g34)
    c: Coincident(g35,g12)
    c: Vertical(g31)
    c: Vertical(g34)
    c: Horizontal(g32)
    c: Horizontal(g35)
    c: Horizontal(g33)
    c: Horizontal(g30)
    c: Horizontal(g28)
    c: Horizontal(g26)
    c: Vertical(g25)
    c: Vertical(g27)
    c: Symmetric(g24,g33,g9)
    c: Symmetric(g30,g27,g9)
    c: Equal(g26,g28)
    c: Equal(g34,g33)
FEATURE [Part::Extrusion] Extrude001  label="проставка_корпуса_штока"
  Base = -> Sketch077
  Dir = (0,0,1)
  DirMode = 2
  FaceMakerClass = Part::FaceMakerBullseye
  FaceMakerMode = 3
  LengthFwd = 10.5
  LengthRev = 0
  Solid = true
  Symmetric = false
FEATURE [PartDesign::FeatureBase] BaseFeature003
  BaseFeature = -> Extrude001
  Suppressed = false
FEATURE [PartDesign::CoordinateSystem] LCS_3
  AttacherType = Attacher::AttachEngine3D
  AttachmentSupport = -> [BaseFeature003]
  MapMode = 2
FEATURE [PartDesign::Body] Body092  label="проставка_корпуса_штока1"
  AllowCompound = false
  BaseFeature = -> Extrude001
  Group = -> [BaseFeature003,LCS_3]
  Origin = -> Origin096
  Tip = -> BaseFeature003
FEATURE [App::Link] ____________________________________________1  label="проставка_корпуса_штока002"
  AttachedBy = #LCS_3
  AttachedTo = Parent Assembly#LCS_Origin
  AttachmentOffset = pos=(0,0,-5.25) rot=(0,0,1;0rad)
  LinkPlacement = pos=(0,0,-5.25) rot=(0,0,1;0rad)
  LinkedObject = -> Body092
  Placement = pos=(0,0,-5.25) rot=(0,0,1;0rad)
  SolverId = Asm4EE
  expr: Placement = LCS_Origin.Placement * AttachmentOffset * LCS_3.Placement ^ -1
FEATURE [Mesh::Feature] Mesh006  label="polzun"
FEATURE [Mesh::Feature] Mesh011  label="crank_pad_rear001"
FEATURE [Mesh::Feature] Mesh012  label="crank_pad_rear002"
FEATURE [Mesh::Feature] Mesh013  label="case_btm"
FEATURE [Mesh::Feature] Mesh014  label="case_top"
FEATURE [Mesh::Feature] Mesh016  label="case_shtok"
FEATURE [Mesh::Feature] Mesh017  label="ecc1"
FEATURE [Mesh::Feature] Mesh018  label="ecc2"
FEATURE [Mesh::Feature] Mesh019  label="case_gear1"
FEATURE [Mesh::Feature] Mesh  label="crank1"
FEATURE [Mesh::Feature] Mesh020  label="crank2"
FEATURE [Mesh::Feature] Mesh021  label="ruchka"
FEATURE [App::DocumentObjectGroup] Group001  label="Meshes"
  Group = -> [Mesh006,Mesh011,Mesh012,Mesh013,Mesh014,Mesh016,Mesh017,Mesh018,Mesh019,Mesh,Mesh020,Mesh021]
FEATURE [PartDesign::CoordinateSystem] shtok2
  AttacherType = Attacher::AttachEngine3D
  AttachmentSupport = -> [Main]
  MapMode = 7
  Placement = pos=(18.403,10.625,0) rot=(0.774597,-0.447214,-0.447214;1.82348rad)
FEATURE [PartDesign::AdditiveCylinder] Cylinder
  Angle = 360
  AttacherType = Attacher::AttachEngine3D
  AttachmentOffset = pos=(41.5,0,6.9) rot=(0,0,1;0rad)
  AttachmentSupport = -> [XY_Plane099]
  FirstAngle = 0
  Height = 13.8
  MapMode = 5
  Placement = pos=(41.5,0,6.9) rot=(0,0,1;0rad)
  Radius = 1.5
  Refine = true
  SecondAngle = 0
  Suppressed = false
  expr: .AttachmentOffset.Base.x = <<Dim_table>>.ecc_dia / 2 + 3 / 2
  expr: .AttachmentOffset.Base.z = 13.8 / 2
FEATURE [App::Link] crank_gear_002  label="crank_gear_003"
  AttachedBy = #Local_CS005
  AttachedTo = Parent Assembly#crank2_axle
  AttachmentOffset = pos=(0,-25.25,0) rot=(1,0,0;1.5708rad)
  LinkPlacement = pos=(-2.74918e-11,21.25,-25.25) rot=(0.990268,0.139173,0;3.14159rad)
  LinkedObject = -> Body087
  Placement = pos=(-2.74918e-11,21.25,-25.25) rot=(0.990268,0.139173,0;3.14159rad)
  SolverId = Asm4EE
  expr: Placement = crank2_axle.Placement * AttachmentOffset * Local_CS005.Placement ^ -1
FEATURE [App::Link] crank_int_gear_01  label="crank_int_gear_003"
  AttachedBy = #Local_CS004
  AttachedTo = Parent Assembly#LCS_Origin
  AttachmentOffset = pos=(0,0,-35.25) rot=(0,0,1;0rad)
  LinkPlacement = pos=(0,0,-35.25) rot=(0,0,1;0rad)
  LinkedObject = -> Body088
  Placement = pos=(0,0,-35.25) rot=(0,0,1;0rad)
  SolverId = Asm4EE
  expr: Placement = LCS_Origin.Placement * AttachmentOffset * Local_CS004.Placement ^ -1
FEATURE [App::Link] crank_int_gear_002
  AttachedBy = #Local_CS004
  AttachedTo = Parent Assembly#LCS_Origin
  AttachmentOffset = pos=(0,0,25.25) rot=(0,0,1;0rad)
  LinkPlacement = pos=(0,0,25.25) rot=(0,0,1;0rad)
  LinkedObject = -> Body088
  Placement = pos=(0,0,25.25) rot=(0,0,1;0rad)
  SolverId = Asm4EE
  expr: Placement = LCS_Origin.Placement * AttachmentOffset * Local_CS004.Placement ^ -1
FEATURE [App::Link] ____________________001  label="Эксцентрик002"
  AttachedBy = #Eccentr
  AttachedTo = Parent Assembly#crank2_axle
  AttachmentOffset = pos=(0,-8.25,0) rot=(1,0,0;4.71239rad)
  LinkPlacement = pos=(-2.74918e-11,21.25,-8.25) rot=(0,0,1;3.14159rad)
  LinkedObject = -> Body001
  Placement = pos=(-2.74918e-11,21.25,-8.25) rot=(0,0,1;3.14159rad)
  SolverId = Asm4EE
  expr: Placement = crank2_axle.Placement * AttachmentOffset * Eccentr.Placement ^ -1
FEATURE [App::Link] crank_gear_01  label="crank_gear_004"
  AttachedBy = #Local_CS005
  AttachedTo = Parent Assembly#crank2_axle
  AttachmentOffset = pos=(0,35.25,0) rot=(1,0,0;1.5708rad)
  LinkPlacement = pos=(-2.74918e-11,21.25,35.25) rot=(0.990268,0.139173,0;3.14159rad)
  LinkedObject = -> Body087
  Placement = pos=(-2.74918e-11,21.25,35.25) rot=(0.990268,0.139173,0;3.14159rad)
  SolverId = Asm4EE
  expr: Placement = crank2_axle.Placement * AttachmentOffset * Local_CS005.Placement ^ -1
FEATURE [PartDesign::CoordinateSystem] LCS_Origin008
  AttacherType = Attacher::AttachEngine3D
  AttachmentSupport = -> [X_Axis098]
  MapMode = 2
FEATURE [PartDesign::AdditiveCylinder] Cylinder001
  Angle = 360
  AttacherType = Attacher::AttachEngine3D
  FirstAngle = 0
  Height = 21.8
  MapMode = 1
  Radius = 1.5
  Refine = true
  SecondAngle = 0
  Suppressed = false
FEATURE [PartDesign::Body] ___________3__21_8  label="ролик 3х21.8"
  AllowCompound = false
  Group = -> [LCS_Origin008,Cylinder001]
  Origin = -> Origin099
  Tip = -> Cylinder001
FEATURE [Sketcher::SketchObject] Sketch
  ArcFitTolerance = 1e-06
  AttachmentSupport = -> [Pad002]
  FullyConstrained = true
  MakeInternals = false
  MapMode = 5
  Placement = pos=(0,-64,0) rot=(1,0,0;1.5708rad)
  sketch-geometry (1):
    g0: Circle CenterX=0 CenterY=0 CenterZ=0 NormalX=0 NormalY=0 NormalZ=1 AngleXU=0 Radius=0.5
  constraints (2):
    c: Coincident(g0,g-1)
    c: Diameter(g0) = 1
FEATURE [PartDesign::Hole] Hole001
  BaseFeature = -> Pad002
  CustomThreadClearance = 0
  Depth = 15
  DepthType = 0
  Diameter = 11
  DrillForDepth = false
  DrillPoint = 1
  DrillPointAngle = 118
  HoleCutCountersinkAngle = 90
  HoleCutCustomValues = false
  HoleCutDepth = 0
  HoleCutDiameter = 6.1
  HoleCutType = 0
  ModelThread = false
  Profile = -> Sketch
  Refine = true
  Suppressed = false
  Tapered = false
  TaperedAngle = 90
  ThreadClass = 0
  ThreadDepth = 15
  ThreadDepthType = 0
  ThreadDirection = 0
  ThreadFit = 0
  ThreadSize = 22
  ThreadType = 2
  Threaded = false
  UseCustomThreadClearance = false
FEATURE [Sketcher::SketchObject] Sketch083
  ArcFitTolerance = 1e-06
  AttachmentSupport = -> [Hole001]
  FullyConstrained = true
  MakeInternals = false
  MapMode = 5
  Placement = pos=(0,64,0) rot=(0,0.707107,0.707107;3.14159rad)
  sketch-geometry (1):
    g0: Circle CenterX=0 CenterY=0 CenterZ=0 NormalX=0 NormalY=0 NormalZ=1 AngleXU=0 Radius=0.5
  constraints (2):
    c: Coincident(g0,g-1)
    c: Diameter(g0) = 1
FEATURE [PartDesign::Hole] Hole002
  BaseFeature = -> Hole001
  CustomThreadClearance = 0
  Depth = 15
  DepthType = 0
  Diameter = 11
  DrillForDepth = false
  DrillPoint = 1
  DrillPointAngle = 118
  HoleCutCountersinkAngle = 90
  HoleCutCustomValues = false
  HoleCutDepth = 0
  HoleCutDiameter = 6.1
  HoleCutType = 0
  ModelThread = false
  Profile = -> Sketch083
  Refine = true
  Suppressed = false
  Tapered = false
  TaperedAngle = 90
  ThreadClass = 0
  ThreadDepth = 15
  ThreadDepthType = 0
  ThreadDirection = 0
  ThreadFit = 0
  ThreadSize = 22
  ThreadType = 2
  Threaded = false
  UseCustomThreadClearance = false
FEATURE [PartDesign::Body] Body002  label="Ползун_рабочий"
  AllowCompound = false
  Group = -> [Sketch007,Pad002,Shtok,Sketch,Hole001,Sketch083,Hole002]
  Origin = -> Origin003
  Tip = -> Hole002
FEATURE [App::Link] ___________________________004  label="Ползун_рабочий003"
  AttachedBy = #Shtok
  AttachedTo = Parent Assembly#shtok2
  AttachmentOffset = pos=(0,0,0) rot=(1,0,0;1.5708rad)
  LinkPlacement = pos=(18.4031,10.625,-3e-16) rot=(0.866025,-0.5,0;3.14159rad)
  LinkedObject = -> Body002
  Placement = pos=(18.4031,10.625,-3e-16) rot=(0.866025,-0.5,0;3.14159rad)
  SolverId = Asm4EE
  expr: Placement = shtok2.Placement * AttachmentOffset * Shtok.Placement ^ -1
FEATURE [PartDesign::SubtractiveCylinder] Cylinder003
  Angle = 360
  AttacherType = Attacher::AttachEngine3D
  AttachmentOffset = pos=(0,0,-14) rot=(0,0,1;0rad)
  AttachmentSupport = -> [Pad001]
  BaseFeature = -> Pad001
  FirstAngle = 0
  Height = 25.2
  MapMode = 2
  Placement = pos=(0,0,-14) rot=(0,0,1;0rad)
  Radius = 16
  Refine = true
  SecondAngle = 0
  Suppressed = false
FEATURE [PartDesign::AdditiveCylinder] Cylinder004
  Angle = 360
  AttacherType = Attacher::AttachEngine3D
  AttachmentOffset = pos=(0,0,-0.5) rot=(0,0,1;0rad)
  AttachmentSupport = -> [BaseFeature]
  BaseFeature = -> BaseFeature
  FirstAngle = 0
  Height = 11
  MapMode = 2
  Placement = pos=(0,0,-0.5) rot=(0,0,1;0rad)
  Radius = 17
  Refine = true
  SecondAngle = 0
  Suppressed = false
FEATURE [PartDesign::SubtractiveCylinder] Cylinder005
  Angle = 360
  AttacherType = Attacher::AttachEngine3D
  AttachmentOffset = pos=(0,0,-3) rot=(0,0,1;0rad)
  AttachmentSupport = -> [BaseFeature]
  BaseFeature = -> Cylinder004
  FirstAngle = 0
  Height = 15
  MapMode = 2
  Placement = pos=(0,0,-3) rot=(0,0,1;0rad)
  Radius = 12.75
  Refine = true
  SecondAngle = 0
  Suppressed = false
FEATURE [PartDesign::Body] Body087  label="crank_gear_01"
  AllowCompound = false
  BaseFeature = -> InvoluteGear006
  Group = -> [BaseFeature,Local_CS005,Cylinder004,Cylinder005]
  Origin = -> Origin090
  Tip = -> Cylinder005
FEATURE [PartDesign::AdditiveCylinder] Cylinder006
  Angle = 360
  AttacherType = Attacher::AttachEngine3D
  FirstAngle = 0
  Height = 22
  MapMode = 2
  Radius = 16
  Refine = true
  SecondAngle = 0
  Suppressed = false
FEATURE [PartDesign::SubtractiveCylinder] Cylinder007
  Angle = 360
  AttacherType = Attacher::AttachEngine3D
  AttachmentSupport = -> [XY_Plane101]
  BaseFeature = -> Cylinder006
  FirstAngle = 0
  Height = 25
  MapMode = 5
  Radius = 12.5
  Refine = true
  SecondAngle = 0
  Suppressed = false
FEATURE [PartDesign::CoordinateSystem] LCS_1
  AttacherType = Attacher::AttachEngine3D
FEATURE [PartDesign::Body] Body095  label="Подшипник 942/25"
  AllowCompound = false
  Group = -> [Cylinder006,Cylinder007,LCS_1]
  Origin = -> Origin100
  Tip = -> Cylinder007
FEATURE [PartDesign::Fillet] Fillet
  Base = -> Clone007 [Edge52,Edge1]
  BaseFeature = -> Clone007
  Radius = 0.25
  Refine = true
  SupportTransform = false
  Suppressed = false
  UseAllEdges = false
FEATURE [PartDesign::Body] Body057  label="Колевал (секция)"
  AllowCompound = false
  Group = -> [Clone007,Crank_shaft,Fillet]
  Origin = -> Origin058
  Tip = -> Fillet
FEATURE [PartDesign::Fillet] Fillet001
  Base = -> Clone [Edge12]
  BaseFeature = -> Clone
  Radius = 0.25
  Refine = true
  SupportTransform = false
  Suppressed = false
  UseAllEdges = false
FEATURE [PartDesign::Body] Body091  label="Шейка_и_щека_задняя_cl"
  AllowCompound = false
  Group = -> [Clone,LCS_2,Fillet001]
  Origin = -> Origin094
  Tip = -> Fillet001
FEATURE [PartDesign::SubtractiveCylinder] Cylinder008
  Angle = 360
  AttacherType = Attacher::AttachEngine3D
  AttachmentOffset = pos=(23,0,-13) rot=(0,0,1;0rad)
  AttachmentSupport = -> [XY_Plane002]
  BaseFeature = -> Cylinder003
  FirstAngle = 0
  Height = 25
  MapMode = 5
  Placement = pos=(23,0,-13) rot=(0,0,1;0rad)
  Radius = 4
  Refine = true
  SecondAngle = 0
  Suppressed = false
FEATURE [PartDesign::SubtractiveCylinder] Cylinder009
  Angle = 360
  AttacherType = Attacher::AttachEngine3D
  AttachmentOffset = pos=(-23,0,-13) rot=(0,0,1;0rad)
  AttachmentSupport = -> [XY_Plane002]
  BaseFeature = -> Cylinder008
  FirstAngle = 0
  Height = 25
  MapMode = 5
  Placement = pos=(-23,0,-13) rot=(0,0,1;0rad)
  Radius = 4
  Refine = true
  SecondAngle = 0
  Suppressed = false
FEATURE [App::Link] ___________________943_027  label="Подшипник 942/025 -003"
  AttachedBy = #LCS_1
  AttachedTo = Parent Assembly#crank2_axle
  AttachmentOffset = pos=(0,-0.1,0) rot=(1,0,0;1.5708rad)
  LinkPlacement = pos=(-2.74918e-11,21.25,-0.1) rot=(1,0,0;3.14159rad)
  LinkedObject = -> Body095
  Placement = pos=(-2.74918e-11,21.25,-0.1) rot=(1,0,0;3.14159rad)
  SolverId = Asm4EE
  expr: Placement = crank2_axle.Placement * AttachmentOffset * LCS_1.Placement ^ -1
FEATURE [PartDesign::PolarPattern] PolarPattern
  Angle = 360
  Axis = -> Z_Axis097
  BaseFeature = -> Cylinder
  Mode = 0
  Occurrences = 87
  Offset = 120
  Originals = -> [Cylinder]
  Placement = pos=(41.5,0,6.9) rot=(0,0,1;0rad)
  Refine = true
  Suppressed = false
  TransformMode = 1
FEATURE [PartDesign::CoordinateSystem] LCS_4
  AttacherType = Attacher::AttachEngine3D
  AttachmentSupport = -> [Z_Axis097]
  MapMode = 7
  Placement = pos=(0,0,0) rot=(0,1,0;3.14159rad)
FEATURE [PartDesign::Body] Body094  label="ролик_3*13,8  - 87шт."
  AllowCompound = false
  Group = -> [Cylinder,PolarPattern,LCS_4]
  Origin = -> Origin098
  Tip = -> PolarPattern
FEATURE [App::Link] ___________3_13_8____87_____  label="ролик_3*13,8  - 87шт. 001"
  AttachedBy = #LCS_4
  AttachedTo = Parent Assembly#shtok2
  AttachmentOffset = pos=(0,-13.8,0) rot=(1,0,0;1.5708rad)
  LinkPlacement = pos=(18.403,10.625,-13.8) rot=(0,0,-1;4.18879rad)
  LinkedObject = -> Body094
  Placement = pos=(18.403,10.625,-13.8) rot=(0,0,-1;4.18879rad)
  SolverId = Asm4EE
  expr: Placement = shtok2.Placement * AttachmentOffset * LCS_4.Placement ^ -1
FEATURE [Sketcher::SketchObject] Sketch084
  ArcFitTolerance = 1e-06
  AttachmentSupport = -> [XY_Plane002]
  FullyConstrained = true
  MakeInternals = false
  MapMode = 5
  expr: Constraints[2] = <<Dim_table>>.crank_len
  expr: Constraints[3] = <<Dim_table>>.ecc_dia
  expr: Constraints[4] = <<Dim_table>>.ecc_dia * 1.2
  sketch-geometry (2):
    g0: Circle CenterX=0 CenterY=-21.25 CenterZ=0 NormalX=0 NormalY=0 NormalZ=1 AngleXU=0 Radius=40
    g1: Circle CenterX=0 CenterY=-21.25 CenterZ=0 NormalX=0 NormalY=0 NormalZ=1 AngleXU=0 Radius=48
  constraints (5):
    c: PointOnObject(g0,g-2)
    c: Coincident(g1,g0)
    c: Distance(g0,g-1) = 21.25
    c: Diameter(g0) = 80
    c: Diameter(g1) = 96
FEATURE [PartDesign::Pocket] Pocket
  BaseFeature = -> Cylinder009
  Direction = (0,0,-1)
  Length = 15.25
  Length2 = -1.25
  Placement = pos=(-23,0,-13) rot=(0,0,1;0rad)
  Profile = -> Sketch084
  ReferenceAxis = -> Sketch084 [N_Axis]
  Refine = true
  Suppressed = false
  Type = 4
FEATURE [PartDesign::Body] Body001  label="Эксцентрик"
  AllowCompound = false
  Group = -> [Sketch005,Pad001,Eccentr,Cylinder003,Cylinder008,Cylinder009,Sketch084,Pocket]
  Origin = -> Origin002
  Tip = -> Pocket
FEATURE [App::Link] _____________________002  label="Шток_поршня003"
  AttachedBy = #Pin
  AttachedTo = Parent Assembly#shtok2
  AttachmentOffset = pos=(0,0,0) rot=(1,0,0;1.5708rad)
  LinkPlacement = pos=(18.403,10.625,0) rot=(0.866025,-0.5,0;3.14159rad)
  LinkedObject = -> Body
  Placement = pos=(18.403,10.625,0) rot=(0.866025,-0.5,0;3.14159rad)
  SolverId = Asm4EE
  expr: Placement = shtok2.Placement * AttachmentOffset * Pin.Placement ^ -1
FEATURE [App::Link] _____________________003  label="Шток_поршня004"
  AttachedBy = #Pin
  AttachedTo = Parent Assembly#shtok2
  AttachmentOffset = pos=(0,0,0) rot=(0,-0.707107,0.707107;3.14159rad)
  LinkPlacement = pos=(18.403,10.625,0) rot=(-0.5,-0.866025,0;3.14159rad)
  LinkedObject = -> Body
  Placement = pos=(18.403,10.625,0) rot=(-0.5,-0.866025,0;3.14159rad)
  SolverId = Asm4EE
  expr: Placement = shtok2.Placement * AttachmentOffset * Pin.Placement ^ -1
FEATURE [Sketcher::SketchObject] Sketch085
  ArcFitTolerance = 1e-06
  AttachmentOffset = pos=(0,0,-66) rot=(0,0,1;0rad)
  AttachmentSupport = -> [XZ_Plane001]
  ExternalGeometry = -> [Pad026]
  FullyConstrained = true
  MakeInternals = false
  MapMode = 5
  Placement = pos=(0,66,-1.47e-14) rot=(1,0,0;1.5708rad)
  sketch-geometry (7):
    g0: ArcOfCircle CenterX=0 CenterY=0 CenterZ=0 NormalX=0 NormalY=0 NormalZ=1 AngleXU=0 Radius=7.5 StartAngle=2.41186 EndAngle=3.87132
    g1: LineSegment StartX=-5.59017 StartY=5 StartZ=0 EndX=5.59017 EndY=5 EndZ=0
    g2: LineSegment StartX=-5.59017 StartY=-5 StartZ=0 EndX=5.59017 EndY=-5 EndZ=0
    g3: ArcOfCircle CenterX=0 CenterY=0 CenterZ=0 NormalX=0 NormalY=0 NormalZ=1 AngleXU=0 Radius=7.5 StartAngle=5.55346 EndAngle=7.01291
    g4: LineSegment [constr] StartX=0 StartY=5 StartZ=0 EndX=0 EndY=-5 EndZ=0
    g5: LineSegment [constr] StartX=5.59017 StartY=5 StartZ=0 EndX=5.59017 EndY=-5 EndZ=0
    g6: Circle CenterX=0 CenterY=0 CenterZ=0 NormalX=0 NormalY=0 NormalZ=1 AngleXU=0 Radius=2
  constraints (20):
    c: Coincident(g0,g-1)
    c: Horizontal(g1)
    c: Horizontal(g2)
    c: Coincident(g0,g1)
    c: Coincident(g1,g3)
    c: Equal(g0,g3)
    c: Coincident(g0,g2)
    c: Coincident(g0,g3)
    c: Equal(g3,g-3)
    c: PointOnObject(g4,g-5)
    c: PointOnObject(g4,g-5)
    c: Coincident(g5,g1)
    c: Coincident(g5,g2)
    c: Vertical(g5)
    c: Equal(g4,g5)
    c: PointOnObject(g4,g-2)
    c: Coincident(g6,g0)
    c: Equal(g6,g-4)
    c: Coincident(g2,g3)
    c: Vertical(g4)
FEATURE [PartDesign::Pad] Pad046
  BaseFeature = -> Pad026
  Direction = (0,-1,2e-16)
  Length = 2
  Length2 = 10
  Placement = pos=(0,0,0) rot=(1,0,0;1.5708rad)
  Profile = -> Sketch085
  ReferenceAxis = -> Sketch085 [N_Axis]
  Refine = true
  Suppressed = false
  Type = 0
FEATURE [PartDesign::Body] Body  label="Шток_поршня"
  AllowCompound = false
  Group = -> [Pin,Sketch053,Pad,Sketch055,Pad026,Sketch085,Pad046]
  Origin = -> Origin001
  Tip = -> Pad046
FEATURE [App::DocumentObjectGroup] Parts
  Group = -> [Body002,Body003,Body004,Body005,Body057,Body061,Body063,Body064,Body066,Body072,Body071,XY_Plane077,Body077,Body001,Body,___________________________,Extrude,InvoluteGear006,InternalInvoluteGear001,Body087,Body088,Body076,Cut,Body091,Body_2,Sketch077,Extrude001,Body092,Body094,___________3__21_8,Body095]
FEATURE [App::Link] ___________________________005  label="Ползун_рабочий004"
  AttachedBy = #Shtok
  AttachedTo = Parent Assembly#Shtok_rama
  AttachmentOffset = pos=(0,-16.5,0) rot=(1,0,0;1.5708rad)
  LinkPlacement = pos=(6.2993e-12,42.5,-16.5) rot=(0,1,0;3.14159rad)
  LinkedObject = -> Body002
  Placement = pos=(6.2993e-12,42.5,-16.5) rot=(0,1,0;3.14159rad)
  SolverId = Asm4EE
  expr: Placement = Shtok_rama.Placement * AttachmentOffset * Shtok.Placement ^ -1
FEATURE [App::Link] ___________3_13_8____87_____001  label="ролик_3*13,8  - 87шт.001"
  AttachedBy = #LCS_4
  AttachedTo = Parent Assembly#Shtok_rama
  AttachmentOffset = pos=(0,-2.7,0) rot=(1,0,0;4.71239rad)
  LinkPlacement = pos=(6.3065e-12,42.5,-2.7) rot=(-1,0,0;3.14159rad)
  LinkedObject = -> Body094
  Placement = pos=(6.3065e-12,42.5,-2.7) rot=(-1,0,0;3.14159rad)
  SolverId = Asm4EE
  expr: Placement = Shtok_rama.Placement * AttachmentOffset * LCS_4.Placement ^ -1
FEATURE [App::Link] _____________________  label="Шток_поршня005"
  AttachedBy = #Pin
  AttachedTo = Parent Assembly#Shtok_rama
  AttachmentOffset = pos=(0,-16.5,0) rot=(1,0,0;1.5708rad)
  LinkPlacement = pos=(6.3065e-12,42.5,-16.5) rot=(0,1,0;3.14159rad)
  LinkedObject = -> Body
  Placement = pos=(6.3065e-12,42.5,-16.5) rot=(0,1,0;3.14159rad)
  SolverId = Asm4EE
  expr: Placement = Shtok_rama.Placement * AttachmentOffset * Pin.Placement ^ -1
FEATURE [App::Link] _____________________004  label="Шток_поршня006"
  AttachedBy = #Pin
  AttachedTo = Parent Assembly#Shtok_rama
  AttachmentOffset = pos=(0,-16.5,0) rot=(1,0,0;4.71239rad)
  LinkPlacement = pos=(6.3065e-12,42.5,-16.5) rot=(0,0,-1;3.14159rad)
  LinkedObject = -> Body
  Placement = pos=(6.3065e-12,42.5,-16.5) rot=(0,0,-1;3.14159rad)
  SolverId = Asm4EE
  expr: Placement = Shtok_rama.Placement * AttachmentOffset * Pin.Placement ^ -1
FEATURE [PartDesign::CoordinateSystem] shtok3
  AttacherType = Attacher::AttachEngine3D
  AttachmentSupport = -> [Main]
  MapMode = 7
  Placement = pos=(-18.403,10.625,0) rot=(-0.377964,0.654654,0.654654;3.86433rad)
FEATURE [App::Link] ___________________________006  label="Ползун_рабочий005"
  AttachedBy = #Shtok
  AttachedTo = Parent Assembly#shtok3
  AttachmentOffset = pos=(0,16.5,0) rot=(1,0,0;1.5708rad)
  LinkPlacement = pos=(-18.403,10.625,16.5) rot=(-0.5,0.866025,0;3.14159rad)
  LinkedObject = -> Body002
  Placement = pos=(-18.403,10.625,16.5) rot=(-0.5,0.866025,0;3.14159rad)
  SolverId = Asm4EE
  expr: Placement = shtok3.Placement * AttachmentOffset * Shtok.Placement ^ -1
FEATURE [App::Link] _____________________005  label="Шток_поршня007"
  AttachedBy = #Pin
  AttachedTo = Parent Assembly#shtok3
  AttachmentOffset = pos=(0,16.5,0) rot=(1,0,0;1.5708rad)
  LinkPlacement = pos=(-18.403,10.625,16.5) rot=(-0.5,0.866025,0;3.14159rad)
  LinkedObject = -> Body
  Placement = pos=(-18.403,10.625,16.5) rot=(-0.5,0.866025,0;3.14159rad)
  SolverId = Asm4EE
  expr: Placement = shtok3.Placement * AttachmentOffset * Pin.Placement ^ -1
FEATURE [App::Link] _____________________006  label="Шток_поршня008"
  AttachedBy = #Pin
  AttachedTo = Parent Assembly#shtok3
  AttachmentOffset = pos=(0,16.5,0) rot=(1,0,0;4.71239rad)
  LinkPlacement = pos=(-18.403,10.625,16.5) rot=(0,0,-1;2.0944rad)
  LinkedObject = -> Body
  Placement = pos=(-18.403,10.625,16.5) rot=(0,0,-1;2.0944rad)
  SolverId = Asm4EE
  expr: Placement = shtok3.Placement * AttachmentOffset * Pin.Placement ^ -1
FEATURE [App::Link] ___________3_13_8____87_____002  label="ролик_3*13,8  - 87шт.002"
  AttachedBy = #LCS_4
  AttachedTo = Parent Assembly#shtok3
  AttachmentOffset = pos=(0,2.75,0) rot=(1,0,0;1.5708rad)
  LinkPlacement = pos=(-18.403,10.625,2.75) rot=(0,0,1;1.0472rad)
  LinkedObject = -> Body094
  Placement = pos=(-18.403,10.625,2.75) rot=(0,0,1;1.0472rad)
  SolverId = Asm4EE
  expr: Placement = shtok3.Placement * AttachmentOffset * LCS_4.Placement ^ -1
FEATURE [App::Link] ___________________942_25  label="Подшипник 942/026"
  AttachedBy = #LCS_1
  AttachedTo = Parent Assembly#crank2_axle
  AttachmentOffset = pos=(0,0.1,0) rot=(1,0,0;4.71239rad)
  LinkPlacement = pos=(-2.74918e-11,21.25,0.1) rot=(0,0,1;0rad)
  LinkedObject = -> Body095
  Placement = pos=(-2.74918e-11,21.25,0.1) rot=(0,0,1;0rad)
  SolverId = Asm4EE
  expr: Placement = crank2_axle.Placement * AttachmentOffset * LCS_1.Placement ^ -1
FEATURE [App::Part] Assembly  label="Assembly_total"
  AssemblyType = Part::Link
  Group = -> [LCS_Origin,Constraints,Variables,Configurations,Main,LCS_6,crank2_axle,Shtok_rama,_____________________________,____________________________________cl,_________________________,___________________________002,_________________________________________________________,____________________________________________1,shtok2,crank_gear_002,crank_int_gear_01,crank_int_gear_002,____________________001,+16 more]
  Origin = -> Origin
  Type = Assembly
